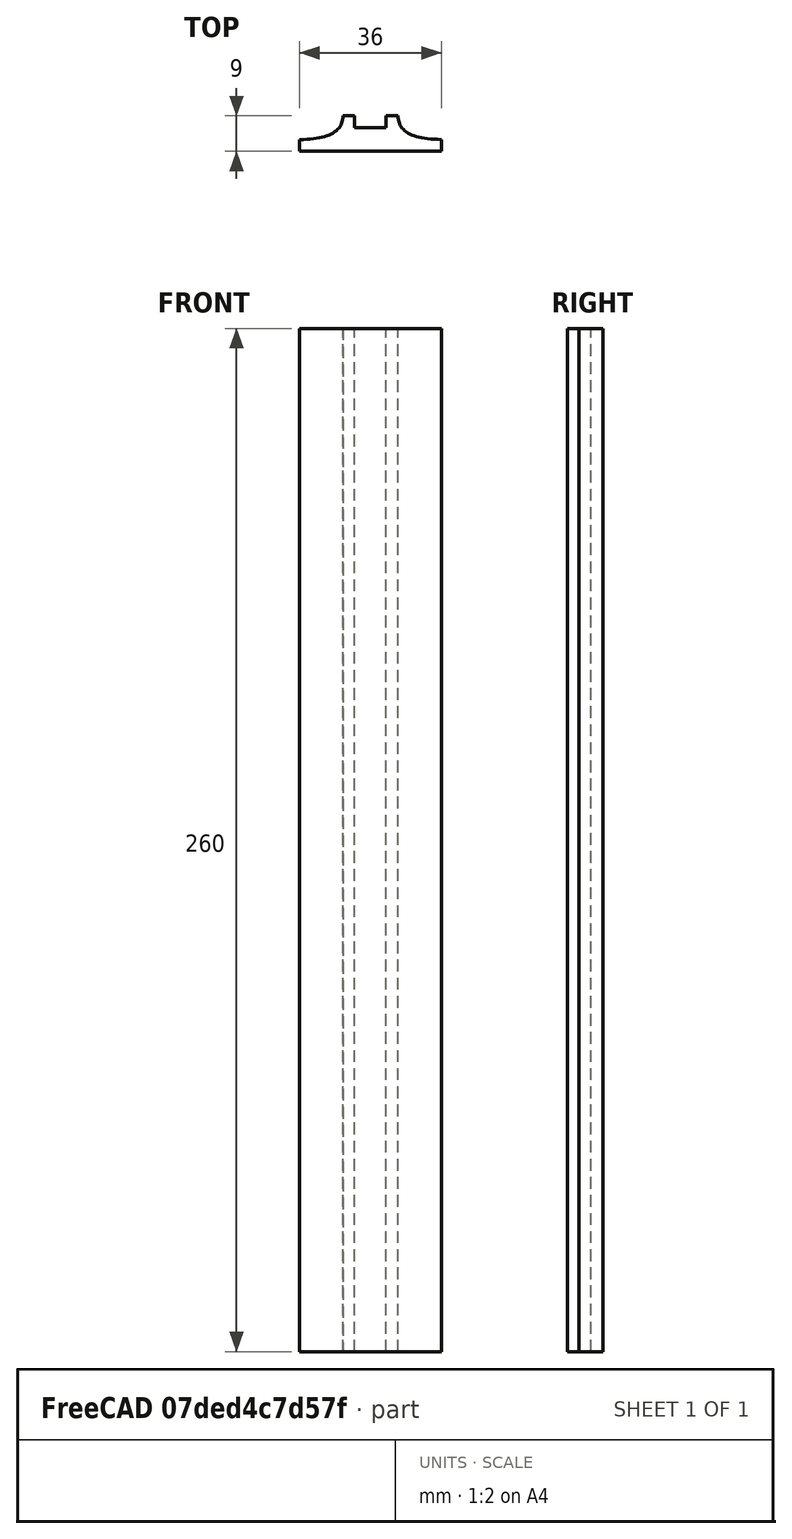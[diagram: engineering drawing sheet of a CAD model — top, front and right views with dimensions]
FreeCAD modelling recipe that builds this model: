
FCSTD DOCUMENT  (FreeCAD 0.19R0.19.2)
Label: laptopStand301.FCStd
License: All rights reserved
LicenseURL: http://en.wikipedia.org/wiki/All_rights_reserved
objects: Sketcher::SketchObject×12, Part::Extrusion×1
note: 13 computed .brp shape members not serialized (recipe doc carries the construction recipe); baked Part::Feature solids carry a one-line shape summary decoded from their .brp

FEATURE [Sketcher::SketchObject] Sketch001  label="legTop"
  FullyConstrained = true
  MapMode = 4
  Placement = pos=(0,0,0) rot=(0.57735,0.57735,0.57735;2.0944rad)
  sketch-geometry (41):
    g0: BSplineCurve PolesCount=3 KnotsCount=2 Degree=2 IsPeriodic=0
    g1: ArcOfCircle CenterX=73.1223 CenterY=-32.291 CenterZ=0 NormalX=0 NormalY=0 NormalZ=1 AngleXU=0 Radius=13 StartAngle=5.92268 EndAngle=9.06428
    g2: ArcOfCircle CenterX=66.7816 CenterY=-49.1439 CenterZ=0 NormalX=0 NormalY=0 NormalZ=1 AngleXU=0 Radius=13 StartAngle=2.78068 EndAngle=5.92131
    g3-g6: Circle x4 (B-spline internal-alignment scaffolding for g7; pole/knot coordinates omitted)
    g7: BSplineCurve PolesCount=4 KnotsCount=2 Degree=3 IsPeriodic=0
    g8: GeomPoint X=28.8094 Y=-19.0875 Z=0
    g9: GeomPoint X=47.0443 Y=-50.4712 Z=0
    g10: Circle CenterX=53.5586 CenterY=-23.2695 CenterZ=0 NormalX=0 NormalY=0 NormalZ=1 AngleXU=0 Radius=3.24518
    g11: LineSegment StartX=17.2232 StartY=-16.0875 StartZ=0 EndX=17.2232 EndY=-19.0875 EndZ=0
    g12: ArcOfCircle CenterX=17.2475 CenterY=-181.166 CenterZ=0 NormalX=0 NormalY=0 NormalZ=1 AngleXU=0 Radius=13 StartAngle=5.92268 EndAngle=7.49361
    g13: ArcOfCircle CenterX=29.5716 CenterY=-148.408 CenterZ=0 NormalX=0 NormalY=0 NormalZ=1 AngleXU=0 Radius=13 StartAngle=4.35228 EndAngle=5.92131
    g14: ArcOfCircle CenterX=35.8967 CenterY=-131.555 CenterZ=0 NormalX=0 NormalY=0 NormalZ=1 AngleXU=0 Radius=13 StartAngle=5.92268 EndAngle=7.49902
    g15: ArcOfCircle CenterX=48.1805 CenterY=-98.7782 CenterZ=0 NormalX=0 NormalY=0 NormalZ=1 AngleXU=0 Radius=13 StartAngle=4.34921 EndAngle=5.92131
    g16: ArcOfCircle CenterX=54.5183 CenterY=-81.9247 CenterZ=0 NormalX=0 NormalY=0 NormalZ=1 AngleXU=0 Radius=13 StartAngle=5.92268 EndAngle=8.70432
    g17: ArcOfCircle CenterX=20.184 CenterY=-217.506 CenterZ=0 NormalX=0 NormalY=0 NormalZ=1 AngleXU=0 Radius=3.81084 StartAngle=1.88136 EndAngle=6.80465
    g18: ArcOfCircle CenterX=36.3663 CenterY=-113.042 CenterZ=0 NormalX=0 NormalY=0 NormalZ=1 AngleXU=0 Radius=3.60555 StartAngle=0.230024 EndAngle=5.3372
    g19: ArcOfCircle CenterX=17.7945 CenterY=-162.686 CenterZ=0 NormalX=0 NormalY=0 NormalZ=1 AngleXU=0 Radius=3.60555 StartAngle=0.230024 EndAngle=5.3372
    g20: ArcOfCircle CenterX=49.8795 CenterY=-62.6074 CenterZ=0 NormalX=0 NormalY=0 NormalZ=1 AngleXU=0 Radius=3.84187 StartAngle=4.46973 EndAngle=9.40343
    g21: LineSegment StartX=48.9563 StartY=-66.3367 StartZ=0 EndX=44.7488 EndY=-73.3482 EndZ=0
    g22: LineSegment StartX=41.085 StartY=-66.3176 StartZ=0 EndX=46.0385 EndY=-62.5254 EndZ=0
    g23: LineSegment StartX=47.0443 StartY=-50.4712 StartZ=0 EndX=41.085 EndY=-66.3176 EndZ=0
    g24: LineSegment StartX=17.2232 StartY=-16.0875 StartZ=0 EndX=117.223 EndY=-16.0875 EndZ=0
    g25: LineSegment StartX=28.8094 StartY=-19.0875 StartZ=0 EndX=17.2232 EndY=-19.0875 EndZ=0
    g26: LineSegment StartX=117.223 StartY=-16.0875 StartZ=0 EndX=117.223 EndY=-19.0875 EndZ=0
    g27: LineSegment StartX=85.2866 StartY=-36.8766 StartZ=0 EndX=78.9396 EndY=-53.7463 EndZ=0
    g28: LineSegment StartX=60.9579 StartY=-27.7053 StartZ=0 EndX=54.6191 EndY=-44.5532 EndZ=0
    g29: LineSegment StartX=23.4884 StartY=-215.608 StartZ=0 EndX=94.6579 EndY=-26.1359 EndZ=0
    g30: LineSegment StartX=19.0195 StartY=-213.878 StartZ=0 EndX=29.4118 EndY=-185.752 EndZ=0
    g31: LineSegment StartX=22.7134 StartY=-166.661 StartZ=0 EndX=21.8316 EndY=-169.001 EndZ=0
    g32: LineSegment StartX=19.9036 StartY=-165.61 StartZ=0 EndX=22.7134 EndY=-166.661 EndZ=0
    g33: LineSegment StartX=21.3051 StartY=-161.864 StartZ=0 EndX=24.1149 EndY=-162.915 EndZ=0
    g34: LineSegment StartX=24.1149 StartY=-162.915 StartZ=0 EndX=24.9906 EndY=-160.574 EndZ=0
    g35: LineSegment StartX=41.7296 StartY=-153.01 StartZ=0 EndX=48.061 EndY=-136.14 EndZ=0
    g36: LineSegment StartX=41.2852 StartY=-117.017 StartZ=0 EndX=40.4148 EndY=-119.365 EndZ=0
    g37: LineSegment StartX=38.4753 StartY=-115.966 StartZ=0 EndX=41.2852 EndY=-117.017 EndZ=0
    g38: LineSegment StartX=39.8769 StartY=-112.22 StartZ=0 EndX=42.6867 EndY=-113.271 EndZ=0
    g39: LineSegment StartX=42.6867 StartY=-113.271 StartZ=0 EndX=43.5622 EndY=-110.93 EndZ=0
    g40: LineSegment StartX=66.6827 StartY=-86.5104 StartZ=0 EndX=60.3386 EndY=-103.381 EndZ=0
  constraints (65):
    c: Block(g0)
    c: Block(g1)
    c: Block(g2)
    c: Weight(g3) = 1
    c: Equal(g3,g4)
    c: Equal(g3,g5)
    c: Equal(g3,g6)
    c: InternalAlignment(g3-g6 -> g7) x4
    c: InternalAlignment(g8,g7)
    c: InternalAlignment(g9,g7)
    c: Block(g10)
    c: Block(g7)
    c: Vertical(g11)
    c: Block(g12)
    c: Block(g13)
    c: Block(g14)
    c: Block(g15)
    c: Block(g16)
    c: Block(g17)
    c: Block(g18)
    c: Block(g19)
    c: Block(g20)
    c: Coincident(g21,g20)
    c: Coincident(g21,g16)
    c: Coincident(g22,g20)
    c: Block(g22)
    c: Coincident(g23,g7)
    c: Coincident(g23,g22)
    c: Coincident(g24,g11)
    c: Horizontal(g24)
    c: Coincident(g25,g7)
    c: Coincident(g25,g11)
    c: Horizontal(g25)
    c: Coincident(g26,g24)
    c: Coincident(g26,g0)
    c: Vertical(g26)
    c: Block(g24)
    c: Coincident(g27,g1)
    c: Coincident(g27,g2)
    c: Coincident(g28,g1)
    c: Coincident(g28,g2)
    c: Coincident(g29,g17)
    c: Coincident(g29,g0)
    c: Coincident(g30,g17)
    c: Coincident(g30,g12)
    c: Coincident(g31,g12)
    c: Coincident(g32,g19)
    c: Coincident(g32,g31)
    c: Block(g31)
    c: Coincident(g33,g19)
    c: Coincident(g34,g33)
    c: Coincident(g34,g13)
    c: Block(g34)
    c: Coincident(g35,g13)
    c: Coincident(g35,g14)
    c: Coincident(g36,g14)
    c: Coincident(g37,g18)
    c: Coincident(g37,g36)
    c: Block(g36)
    c: Coincident(g38,g18)
    c: Coincident(g39,g38)
    c: Coincident(g39,g15)
    c: Block(g39)
    c: Coincident(g40,g16)
    c: Coincident(g40,g15)
FEATURE [Sketcher::SketchObject] Sketch002
  FullyConstrained = true
  sketch-geometry (20):
    g0: LineSegment StartX=-2.77179 StartY=-200.304 StartZ=0 EndX=5.22821 EndY=-200.304 EndZ=0
    g1: LineSegment StartX=5.22821 StartY=-200.304 StartZ=0 EndX=5.22821 EndY=-197.304 EndZ=0
    g2: LineSegment StartX=-2.77179 StartY=-200.304 StartZ=0 EndX=-2.77179 EndY=-197.304 EndZ=0
    g3: LineSegment StartX=5.22821 StartY=-197.304 StartZ=0 EndX=8.22821 EndY=-197.304 EndZ=0
    g4: LineSegment StartX=-2.77179 StartY=-197.304 StartZ=0 EndX=-5.77179 EndY=-197.304 EndZ=0
    g5: LineSegment StartX=19.2282 StartY=-203.304 StartZ=0 EndX=19.2282 EndY=-206.304 EndZ=0
    g6: LineSegment StartX=-16.7718 StartY=-203.304 StartZ=0 EndX=-16.7718 EndY=-206.304 EndZ=0
    g7: LineSegment StartX=-16.7718 StartY=-206.304 StartZ=0 EndX=19.2282 EndY=-206.304 EndZ=0
    g8: Circle CenterX=-16.7718 CenterY=-203.304 CenterZ=0 NormalX=0 NormalY=0 NormalZ=1 AngleXU=0 Radius=1
    g9: Circle CenterX=-5.77179 CenterY=-203.304 CenterZ=0 NormalX=0 NormalY=0 NormalZ=1 AngleXU=0 Radius=1
    g10: Circle CenterX=-5.77179 CenterY=-197.304 CenterZ=0 NormalX=0 NormalY=0 NormalZ=1 AngleXU=0 Radius=1
    g11: BSplineCurve PolesCount=3 KnotsCount=2 Degree=2 IsPeriodic=0
    g12: GeomPoint X=-16.7718 Y=-203.304 Z=0
    g13: GeomPoint X=-5.77179 Y=-197.304 Z=0
    g14: Circle CenterX=19.2282 CenterY=-203.304 CenterZ=0 NormalX=0 NormalY=0 NormalZ=1 AngleXU=0 Radius=1
    g15: Circle CenterX=8.22821 CenterY=-203.304 CenterZ=0 NormalX=0 NormalY=0 NormalZ=1 AngleXU=0 Radius=1
    g16: Circle CenterX=8.22821 CenterY=-197.304 CenterZ=0 NormalX=0 NormalY=0 NormalZ=1 AngleXU=0 Radius=1
    g17: BSplineCurve PolesCount=3 KnotsCount=2 Degree=2 IsPeriodic=0
    g18: GeomPoint X=19.2282 Y=-203.304 Z=0
    g19: GeomPoint X=8.22821 Y=-197.304 Z=0
  constraints (41):
    c: Horizontal(g0)
    c: Distance(g0) = 8
    c: Coincident(g1,g0)
    c: Vertical(g1)
    c: Distance(g1) = 3
    c: Coincident(g2,g0)
    c: Vertical(g2)
    c: Distance(g2) = 3
    c: Coincident(g3,g1)
    c: Horizontal(g3)
    c: Distance(g3) = 3
    c: Coincident(g4,g2)
    c: Horizontal(g4)
    c: Distance(g4) = 3
    c: Vertical(g5)
    c: Vertical(g6)
    c: Coincident(g7,g6)
    c: Coincident(g7,g5)
    c: Weight(g8) = 1
    c: Equal(g8,g9)
    c: Equal(g8,g10)
    c: Coincident(g11,g4)
    c: InternalAlignment(g8,g11)
    c: InternalAlignment(g9,g11)
    c: InternalAlignment(g10,g11)
    c: InternalAlignment(g12,g11)
    c: InternalAlignment(g13,g11)
    c: Coincident(g17,g5)
    c: Weight(g14) = 1
    c: Equal(g14,g15)
    c: Equal(g14,g16)
    c: Coincident(g17,g3)
    c: InternalAlignment(g14,g17)
    c: InternalAlignment(g15,g17)
    c: InternalAlignment(g16,g17)
    c: InternalAlignment(g18,g17)
    c: InternalAlignment(g19,g17)
    c: Block(g7)
    c: Block(g17)
    c: Block(g11)
    c: Block(g6)
FEATURE [Part::Extrusion] Extrude003
  Base = -> Sketch002
  Dir = (0,0,1)
  DirMode = 2
  FaceMakerClass = Part::FaceMakerBullseye
  LengthFwd = 260
  LengthRev = 0
  Solid = true
  Symmetric = false
FEATURE [Sketcher::SketchObject] Sketch003  label="original"
  FullyConstrained = false
  sketch-geometry (469):
    g0: LineSegment StartX=-42.9272 StartY=136.221 StartZ=0 EndX=-42.9272 EndY=-103.779 EndZ=0
    g1: LineSegment StartX=407.073 StartY=136.221 StartZ=0 EndX=407.073 EndY=-103.779 EndZ=0
    g2: ArcOfCircle CenterX=-26.9272 CenterY=-83.7794 CenterZ=0 NormalX=0 NormalY=0 NormalZ=1 AngleXU=0 Radius=8 StartAngle=3.14159 EndAngle=6.28319
    g3: ArcOfCircle CenterX=391.073 CenterY=-83.7794 CenterZ=0 NormalX=0 NormalY=0 NormalZ=1 AngleXU=0 Radius=8 StartAngle=3.14159 EndAngle=6.28319
    g4: Circle CenterX=175.022 CenterY=27.0628 CenterZ=0 NormalX=0 NormalY=0 NormalZ=1 AngleXU=0 Radius=1
    g5: Circle CenterX=179.022 CenterY=24.8665 CenterZ=0 NormalX=0 NormalY=0 NormalZ=1 AngleXU=0 Radius=1
    g6: Circle CenterX=179.022 CenterY=27.0628 CenterZ=0 NormalX=0 NormalY=0 NormalZ=1 AngleXU=0 Radius=1
    g7: BSplineCurve PolesCount=3 KnotsCount=2 Degree=2 IsPeriodic=0
    g8: GeomPoint X=175.022 Y=27.0628 Z=0
    g9: GeomPoint X=179.022 Y=27.0628 Z=0
    g10: Circle CenterX=189.124 CenterY=27.0628 CenterZ=0 NormalX=0 NormalY=0 NormalZ=1 AngleXU=0 Radius=1
    g11: Circle CenterX=185.124 CenterY=24.8665 CenterZ=0 NormalX=0 NormalY=0 NormalZ=1 AngleXU=0 Radius=1
    g12: Circle CenterX=185.124 CenterY=27.0628 CenterZ=0 NormalX=0 NormalY=0 NormalZ=1 AngleXU=0 Radius=1
    g13: BSplineCurve PolesCount=3 KnotsCount=2 Degree=2 IsPeriodic=0
    g14: GeomPoint X=189.124 Y=27.0628 Z=0
    g15: GeomPoint X=185.124 Y=27.0628 Z=0
    g16: Circle CenterX=175.022 CenterY=5.37834 CenterZ=0 NormalX=0 NormalY=0 NormalZ=1 AngleXU=0 Radius=1
    g17: Circle CenterX=179.022 CenterY=7.57463 CenterZ=0 NormalX=0 NormalY=0 NormalZ=1 AngleXU=0 Radius=1
    g18: Circle CenterX=179.022 CenterY=5.34704 CenterZ=0 NormalX=0 NormalY=0 NormalZ=1 AngleXU=0 Radius=1
    g19: BSplineCurve PolesCount=3 KnotsCount=2 Degree=2 IsPeriodic=0
    g20: GeomPoint X=175.022 Y=5.37834 Z=0
    g21: GeomPoint X=179.022 Y=5.34704 Z=0
    g22: Circle CenterX=189.124 CenterY=5.37834 CenterZ=0 NormalX=0 NormalY=0 NormalZ=1 AngleXU=0 Radius=1
    g23: Circle CenterX=185.124 CenterY=7.57463 CenterZ=0 NormalX=0 NormalY=0 NormalZ=1 AngleXU=0 Radius=1
    g24: Circle CenterX=185.124 CenterY=5.34704 CenterZ=0 NormalX=0 NormalY=0 NormalZ=1 AngleXU=0 Radius=1
    g25: BSplineCurve PolesCount=3 KnotsCount=2 Degree=2 IsPeriodic=0
    g26: GeomPoint X=189.124 Y=5.37834 Z=0
    g27: GeomPoint X=185.124 Y=5.34704 Z=0
    g28: Circle CenterX=165.871 CenterY=18.1458 CenterZ=0 NormalX=0 NormalY=0 NormalZ=1 AngleXU=0 Radius=1
    g29: Circle CenterX=169.377 CenterY=16.2206 CenterZ=0 NormalX=0 NormalY=0 NormalZ=1 AngleXU=0 Radius=1
    g30: Circle CenterX=165.871 CenterY=14.2956 CenterZ=0 NormalX=0 NormalY=0 NormalZ=1 AngleXU=0 Radius=1
    g31: BSplineCurve PolesCount=3 KnotsCount=2 Degree=2 IsPeriodic=0
    g32: GeomPoint X=165.871 Y=18.1458 Z=0
    g33: GeomPoint X=165.871 Y=14.2956 Z=0
    g34: Circle CenterX=198.275 CenterY=18.1318 CenterZ=0 NormalX=0 NormalY=0 NormalZ=1 AngleXU=0 Radius=1
    g35: Circle CenterX=194.768 CenterY=16.2206 CenterZ=0 NormalX=0 NormalY=0 NormalZ=1 AngleXU=0 Radius=1
    g36: Circle CenterX=198.264 CenterY=14.2963 CenterZ=0 NormalX=0 NormalY=0 NormalZ=1 AngleXU=0 Radius=1
    g37: BSplineCurve PolesCount=3 KnotsCount=2 Degree=2 IsPeriodic=0
    g38: GeomPoint X=198.275 Y=18.1318 Z=0
    g39: GeomPoint X=198.264 Y=14.2963 Z=0
    g40: LineSegment StartX=407.073 StartY=-103.779 StartZ=0 EndX=-42.9272 EndY=-103.779 EndZ=0
    g41: Circle CenterX=125.607 CenterY=54.1951 CenterZ=0 NormalX=0 NormalY=0 NormalZ=1 AngleXU=0 Radius=1
    g42: Circle CenterX=139.632 CenterY=46.4944 CenterZ=0 NormalX=0 NormalY=0 NormalZ=1 AngleXU=0 Radius=1
    g43: Circle CenterX=127.326 CenterY=56.7187 CenterZ=0 NormalX=0 NormalY=0 NormalZ=1 AngleXU=0 Radius=1
    g44: BSplineCurve PolesCount=3 KnotsCount=2 Degree=2 IsPeriodic=0
    g45: GeomPoint X=125.607 Y=54.1951 Z=0
    g46: GeomPoint X=127.326 Y=56.7187 Z=0
    g47: Circle CenterX=236.824 CenterY=56.7187 CenterZ=0 NormalX=0 NormalY=0 NormalZ=1 AngleXU=0 Radius=1
    g48: Circle CenterX=224.513 CenterY=46.4944 CenterZ=0 NormalX=0 NormalY=0 NormalZ=1 AngleXU=0 Radius=1
    g49: Circle CenterX=238.538 CenterY=54.1951 CenterZ=0 NormalX=0 NormalY=0 NormalZ=1 AngleXU=0 Radius=1
    g50: BSplineCurve PolesCount=3 KnotsCount=2 Degree=2 IsPeriodic=0
    g51: GeomPoint X=236.824 Y=56.7187 Z=0
    g52: GeomPoint X=238.538 Y=54.1951 Z=0
    g53: Circle CenterX=238.538 CenterY=-21.7516 CenterZ=0 NormalX=0 NormalY=0 NormalZ=1 AngleXU=0 Radius=1
    g54: Circle CenterX=224.513 CenterY=-14.0532 CenterZ=0 NormalX=0 NormalY=0 NormalZ=1 AngleXU=0 Radius=1
    g55: Circle CenterX=236.584 CenterY=-24.2775 CenterZ=0 NormalX=0 NormalY=0 NormalZ=1 AngleXU=0 Radius=1
    g56: BSplineCurve PolesCount=3 KnotsCount=2 Degree=2 IsPeriodic=0
    g57: GeomPoint X=238.538 Y=-21.7516 Z=0
    g58: GeomPoint X=236.584 Y=-24.2775 Z=0
    g59: Circle CenterX=125.607 CenterY=-21.7539 CenterZ=0 NormalX=0 NormalY=0 NormalZ=1 AngleXU=0 Radius=1
    g60: Circle CenterX=139.632 CenterY=-14.0532 CenterZ=0 NormalX=0 NormalY=0 NormalZ=1 AngleXU=0 Radius=1
    g61: Circle CenterX=127.325 CenterY=-24.2775 CenterZ=0 NormalX=0 NormalY=0 NormalZ=1 AngleXU=0 Radius=1
    g62: BSplineCurve PolesCount=3 KnotsCount=2 Degree=2 IsPeriodic=0
    g63: GeomPoint X=125.607 Y=-21.7539 Z=0
    g64: GeomPoint X=127.325 Y=-24.2775 Z=0
    g65: Circle CenterX=302.996 CenterY=111.695 CenterZ=0 NormalX=0 NormalY=0 NormalZ=1 AngleXU=0 Radius=1
    g66: Circle CenterX=306.073 CenterY=114.251 CenterZ=0 NormalX=0 NormalY=0 NormalZ=1 AngleXU=0 Radius=1
    g67: Circle CenterX=306.073 CenterY=110.251 CenterZ=0 NormalX=0 NormalY=0 NormalZ=1 AngleXU=0 Radius=1
    g68: BSplineCurve PolesCount=3 KnotsCount=2 Degree=2 IsPeriodic=0
    g69: GeomPoint X=302.996 Y=111.695 Z=0
    g70: GeomPoint X=306.073 Y=110.251 Z=0
    g71: Circle CenterX=306.073 CenterY=95.2763 CenterZ=0 NormalX=0 NormalY=0 NormalZ=1 AngleXU=0 Radius=1
    g72: Circle CenterX=306.073 CenterY=91.2763 CenterZ=0 NormalX=0 NormalY=0 NormalZ=1 AngleXU=0 Radius=1
    g73: Circle CenterX=302.567 CenterY=89.3511 CenterZ=0 NormalX=0 NormalY=0 NormalZ=1 AngleXU=0 Radius=1
    g74: BSplineCurve PolesCount=3 KnotsCount=2 Degree=2 IsPeriodic=0
    g75: GeomPoint X=306.073 Y=95.2763 Z=0
    g76: GeomPoint X=302.567 Y=89.3511 Z=0
    g77: LineSegment StartX=306.073 StartY=110.251 StartZ=0 EndX=306.073 EndY=95.2763 EndZ=0
    g78: LineSegment StartX=302.996 StartY=111.695 StartZ=0 EndX=236.824 EndY=56.7187 EndZ=0
    g79: LineSegment StartX=238.538 StartY=54.1951 StartZ=0 EndX=302.567 EndY=89.3511 EndZ=0
    g80: Circle CenterX=61.1496 CenterY=111.695 CenterZ=0 NormalX=0 NormalY=0 NormalZ=1 AngleXU=0 Radius=1
    g81: Circle CenterX=58.0728 CenterY=114.251 CenterZ=0 NormalX=0 NormalY=0 NormalZ=1 AngleXU=0 Radius=1
    g82: Circle CenterX=58.0728 CenterY=110.251 CenterZ=0 NormalX=0 NormalY=0 NormalZ=1 AngleXU=0 Radius=1
    g83: BSplineCurve PolesCount=3 KnotsCount=2 Degree=2 IsPeriodic=0
    g84: GeomPoint X=61.1496 Y=111.695 Z=0
    g85: GeomPoint X=58.0728 Y=110.251 Z=0
    g86: Circle CenterX=61.5791 CenterY=89.3511 CenterZ=0 NormalX=0 NormalY=0 NormalZ=1 AngleXU=0 Radius=1
    g87: Circle CenterX=58.0728 CenterY=91.2763 CenterZ=0 NormalX=0 NormalY=0 NormalZ=1 AngleXU=0 Radius=1
    g88: Circle CenterX=58.0728 CenterY=95.2763 CenterZ=0 NormalX=0 NormalY=0 NormalZ=1 AngleXU=0 Radius=1
    g89: BSplineCurve PolesCount=3 KnotsCount=2 Degree=2 IsPeriodic=0
    g90: GeomPoint X=61.5791 Y=89.3511 Z=0
    g91: GeomPoint X=58.0728 Y=95.2763 Z=0
    g92: LineSegment StartX=58.0728 StartY=110.251 StartZ=0 EndX=58.0728 EndY=95.2763 EndZ=0
    g93: LineSegment StartX=61.1496 StartY=111.695 StartZ=0 EndX=127.326 EndY=56.7187 EndZ=0
    g94: LineSegment StartX=125.607 StartY=54.1951 StartZ=0 EndX=61.5791 EndY=89.3511 EndZ=0
    g95: Circle CenterX=61.5791 CenterY=-56.9099 CenterZ=0 NormalX=0 NormalY=0 NormalZ=1 AngleXU=0 Radius=1
    g96: Circle CenterX=58.0728 CenterY=-58.8351 CenterZ=0 NormalX=0 NormalY=0 NormalZ=1 AngleXU=0 Radius=1
    g97: Circle CenterX=58.0728 CenterY=-62.8351 CenterZ=0 NormalX=0 NormalY=0 NormalZ=1 AngleXU=0 Radius=1
    g98: BSplineCurve PolesCount=3 KnotsCount=2 Degree=2 IsPeriodic=0
    g99: GeomPoint X=61.5791 Y=-56.9099 Z=0
    g100: GeomPoint X=58.0728 Y=-62.8351 Z=0
    g101: Circle CenterX=58.0728 CenterY=-77.8102 CenterZ=0 NormalX=0 NormalY=0 NormalZ=1 AngleXU=0 Radius=1
    g102: Circle CenterX=58.0728 CenterY=-81.8102 CenterZ=0 NormalX=0 NormalY=0 NormalZ=1 AngleXU=0 Radius=1
    g103: Circle CenterX=61.1496 CenterY=-79.2541 CenterZ=0 NormalX=0 NormalY=0 NormalZ=1 AngleXU=0 Radius=1
    g104: BSplineCurve PolesCount=3 KnotsCount=2 Degree=2 IsPeriodic=0
    g105: GeomPoint X=58.0728 Y=-77.8102 Z=0
    g106: GeomPoint X=61.1496 Y=-79.2541 Z=0
    g107: LineSegment StartX=58.0728 StartY=-62.8351 StartZ=0 EndX=58.0728 EndY=-77.8102 EndZ=0
    g108: LineSegment StartX=61.1496 StartY=-79.2541 StartZ=0 EndX=127.325 EndY=-24.2775 EndZ=0
    g109: LineSegment StartX=125.607 StartY=-21.7539 StartZ=0 EndX=61.5791 EndY=-56.9099 EndZ=0
    g110: Circle CenterX=302.567 CenterY=-56.9099 CenterZ=0 NormalX=0 NormalY=0 NormalZ=1 AngleXU=0 Radius=1
    g111: Circle CenterX=306.073 CenterY=-58.8351 CenterZ=0 NormalX=0 NormalY=0 NormalZ=1 AngleXU=0 Radius=1
    g112: Circle CenterX=306.073 CenterY=-62.8351 CenterZ=0 NormalX=0 NormalY=0 NormalZ=1 AngleXU=0 Radius=1
    g113: BSplineCurve PolesCount=3 KnotsCount=2 Degree=2 IsPeriodic=0
    g114: GeomPoint X=302.567 Y=-56.9099 Z=0
    g115: GeomPoint X=306.073 Y=-62.8351 Z=0
    g116: Circle CenterX=302.996 CenterY=-79.2541 CenterZ=0 NormalX=0 NormalY=0 NormalZ=1 AngleXU=0 Radius=1
    g117: Circle CenterX=306.073 CenterY=-81.8102 CenterZ=0 NormalX=0 NormalY=0 NormalZ=1 AngleXU=0 Radius=1
    g118: Circle CenterX=306.073 CenterY=-77.8102 CenterZ=0 NormalX=0 NormalY=0 NormalZ=1 AngleXU=0 Radius=1
    g119: BSplineCurve PolesCount=3 KnotsCount=2 Degree=2 IsPeriodic=0
    g120: GeomPoint X=302.996 Y=-79.2541 Z=0
    g121: GeomPoint X=306.073 Y=-77.8102 Z=0
    g122: LineSegment StartX=306.073 StartY=-62.8351 StartZ=0 EndX=306.073 EndY=-77.8102 EndZ=0
    g123: LineSegment StartX=302.996 StartY=-79.2541 StartZ=0 EndX=236.584 EndY=-24.2775 EndZ=0
    g124: LineSegment StartX=238.538 StartY=-21.7516 StartZ=0 EndX=302.567 EndY=-56.9099 EndZ=0
    g125: Circle CenterX=61.6457 CenterY=-88.8112 CenterZ=0 NormalX=0 NormalY=0 NormalZ=1 AngleXU=0 Radius=1
    g126: Circle CenterX=58.0728 CenterY=-91.7794 CenterZ=0 NormalX=0 NormalY=0 NormalZ=1 AngleXU=0 Radius=1
    g127: Circle CenterX=63.9135 CenterY=-91.7791 CenterZ=0 NormalX=0 NormalY=0 NormalZ=1 AngleXU=0 Radius=1
    g128: BSplineCurve PolesCount=3 KnotsCount=2 Degree=2 IsPeriodic=0
    g129: GeomPoint X=61.6457 Y=-88.8112 Z=0
    g130: GeomPoint X=63.9135 Y=-91.7791 Z=0
    g131: Circle CenterX=179.022 CenterY=-85.8163 CenterZ=0 NormalX=0 NormalY=0 NormalZ=1 AngleXU=0 Radius=1
    g132: Circle CenterX=179.022 CenterY=-91.7794 CenterZ=0 NormalX=0 NormalY=0 NormalZ=1 AngleXU=0 Radius=1
    g133: Circle CenterX=171.895 CenterY=-91.7791 CenterZ=0 NormalX=0 NormalY=0 NormalZ=1 AngleXU=0 Radius=1
    g134: BSplineCurve PolesCount=3 KnotsCount=2 Degree=2 IsPeriodic=0
    g135: GeomPoint X=179.022 Y=-85.8163 Z=0
    g136: GeomPoint X=171.895 Y=-91.7791 Z=0
    g137: Circle CenterX=185.124 CenterY=-86.2028 CenterZ=0 NormalX=0 NormalY=0 NormalZ=1 AngleXU=0 Radius=1
    g138: Circle CenterX=185.124 CenterY=-91.7794 CenterZ=0 NormalX=0 NormalY=0 NormalZ=1 AngleXU=0 Radius=1
    g139: Circle CenterX=191.747 CenterY=-91.7794 CenterZ=0 NormalX=0 NormalY=0 NormalZ=1 AngleXU=0 Radius=1
    g140: BSplineCurve PolesCount=3 KnotsCount=2 Degree=2 IsPeriodic=0
    g141: GeomPoint X=185.124 Y=-86.2028 Z=0
    g142: GeomPoint X=191.747 Y=-91.7794 Z=0
    g143: Circle CenterX=299.888 CenterY=-86.6413 CenterZ=0 NormalX=0 NormalY=0 NormalZ=1 AngleXU=0 Radius=1
    g144: Circle CenterX=306.073 CenterY=-91.7794 CenterZ=0 NormalX=0 NormalY=0 NormalZ=1 AngleXU=0 Radius=1
    g145: Circle CenterX=298.776 CenterY=-91.7794 CenterZ=0 NormalX=0 NormalY=0 NormalZ=1 AngleXU=0 Radius=1
    g146: BSplineCurve PolesCount=3 KnotsCount=2 Degree=2 IsPeriodic=0
    g147: GeomPoint X=299.888 Y=-86.6413 Z=0
    g148: GeomPoint X=298.776 Y=-91.7794 Z=0
    g149: LineSegment StartX=189.124 StartY=5.37834 StartZ=0 EndX=299.888 EndY=-86.6413 EndZ=0
    g150: LineSegment StartX=298.776 StartY=-91.7794 StartZ=0 EndX=191.747 EndY=-91.7794 EndZ=0
    g151: LineSegment StartX=185.124 StartY=-86.2028 StartZ=0 EndX=185.124 EndY=5.34704 EndZ=0
    g152: LineSegment StartX=179.022 StartY=5.34704 StartZ=0 EndX=179.022 EndY=-85.8163 EndZ=0
    g153: LineSegment StartX=171.895 StartY=-91.7791 StartZ=0 EndX=63.9135 EndY=-91.7791 EndZ=0
    g154: LineSegment StartX=61.6457 StartY=-88.8112 StartZ=0 EndX=175.022 EndY=5.37834 EndZ=0
    g155: Circle CenterX=302.073 CenterY=124.221 CenterZ=0 NormalX=0 NormalY=0 NormalZ=1 AngleXU=0 Radius=1
    g156: Circle CenterX=306.073 CenterY=124.221 CenterZ=0 NormalX=0 NormalY=0 NormalZ=1 AngleXU=0 Radius=1
    g157: Circle CenterX=302.996 CenterY=121.665 CenterZ=0 NormalX=0 NormalY=0 NormalZ=1 AngleXU=0 Radius=1
    g158: BSplineCurve PolesCount=3 KnotsCount=2 Degree=2 IsPeriodic=0
    g159: GeomPoint X=302.073 Y=124.221 Z=0
    g160: GeomPoint X=302.996 Y=121.665 Z=0
    g161: Circle CenterX=189.124 CenterY=124.221 CenterZ=0 NormalX=0 NormalY=0 NormalZ=1 AngleXU=0 Radius=1
    g162: Circle CenterX=185.124 CenterY=124.221 CenterZ=0 NormalX=0 NormalY=0 NormalZ=1 AngleXU=0 Radius=1
    g163: Circle CenterX=185.124 CenterY=120.221 CenterZ=0 NormalX=0 NormalY=0 NormalZ=1 AngleXU=0 Radius=1
    g164: BSplineCurve PolesCount=3 KnotsCount=2 Degree=2 IsPeriodic=0
    g165: GeomPoint X=189.124 Y=124.221 Z=0
    g166: GeomPoint X=185.124 Y=120.221 Z=0
    g167: Circle CenterX=175.022 CenterY=124.221 CenterZ=0 NormalX=0 NormalY=0 NormalZ=1 AngleXU=0 Radius=1
    g168: Circle CenterX=179.022 CenterY=124.221 CenterZ=0 NormalX=0 NormalY=0 NormalZ=1 AngleXU=0 Radius=1
    g169: Circle CenterX=179.022 CenterY=120.221 CenterZ=0 NormalX=0 NormalY=0 NormalZ=1 AngleXU=0 Radius=1
    g170: BSplineCurve PolesCount=3 KnotsCount=2 Degree=2 IsPeriodic=0
    g171: GeomPoint X=175.022 Y=124.221 Z=0
    g172: GeomPoint X=179.022 Y=120.221 Z=0
    g173: Circle CenterX=62.0728 CenterY=124.221 CenterZ=0 NormalX=0 NormalY=0 NormalZ=1 AngleXU=0 Radius=1
    g174: Circle CenterX=58.0728 CenterY=124.221 CenterZ=0 NormalX=0 NormalY=0 NormalZ=1 AngleXU=0 Radius=1
    g175: Circle CenterX=61.1496 CenterY=121.665 CenterZ=0 NormalX=0 NormalY=0 NormalZ=1 AngleXU=0 Radius=1
    g176: BSplineCurve PolesCount=3 KnotsCount=2 Degree=2 IsPeriodic=0
    g177: GeomPoint X=62.0728 Y=124.221 Z=0
    g178: GeomPoint X=61.1496 Y=121.665 Z=0
    g179: LineSegment StartX=179.022 StartY=120.221 StartZ=0 EndX=179.022 EndY=27.0628 EndZ=0
    g180: LineSegment StartX=185.124 StartY=27.0628 StartZ=0 EndX=185.124 EndY=120.221 EndZ=0
    g181: LineSegment StartX=302.996 StartY=121.665 StartZ=0 EndX=189.124 EndY=27.0628 EndZ=0
    g182: LineSegment StartX=175.022 StartY=27.0628 StartZ=0 EndX=61.1496 EndY=121.665 EndZ=0
    g183: Circle CenterX=61.5791 CenterY=75.4095 CenterZ=0 NormalX=0 NormalY=0 NormalZ=1 AngleXU=0 Radius=1
    g184: Circle CenterX=58.0728 CenterY=77.3346 CenterZ=0 NormalX=0 NormalY=0 NormalZ=1 AngleXU=0 Radius=1
    g185: Circle CenterX=58.0728 CenterY=73.3346 CenterZ=0 NormalX=0 NormalY=0 NormalZ=1 AngleXU=0 Radius=1
    g186: BSplineCurve PolesCount=3 KnotsCount=2 Degree=2 IsPeriodic=0
    g187: GeomPoint X=61.5791 Y=75.4095 Z=0
    g188: GeomPoint X=58.0728 Y=73.3346 Z=0
    g189: Circle CenterX=58.0728 CenterY=-40.8935 CenterZ=0 NormalX=0 NormalY=0 NormalZ=1 AngleXU=0 Radius=1
    g190: Circle CenterX=58.0728 CenterY=-44.8935 CenterZ=0 NormalX=0 NormalY=0 NormalZ=1 AngleXU=0 Radius=1
    g191: Circle CenterX=61.5791 CenterY=-42.9683 CenterZ=0 NormalX=0 NormalY=0 NormalZ=1 AngleXU=0 Radius=1
    g192: BSplineCurve PolesCount=3 KnotsCount=2 Degree=2 IsPeriodic=0
    g193: GeomPoint X=58.0728 Y=-40.8935 Z=0
    g194: GeomPoint X=61.5791 Y=-42.9683 Z=0
    g195: LineSegment StartX=61.5791 StartY=-42.9683 StartZ=0 EndX=165.871 EndY=14.2956 EndZ=0
    g196: LineSegment StartX=165.871 StartY=18.1458 StartZ=0 EndX=61.5791 EndY=75.4095 EndZ=0
    g197: LineSegment StartX=58.0728 StartY=73.3346 StartZ=0 EndX=58.0728 EndY=-40.8935 EndZ=0
    g198: Circle CenterX=302.567 CenterY=-42.9683 CenterZ=0 NormalX=0 NormalY=0 NormalZ=1 AngleXU=0 Radius=1
    g199: Circle CenterX=306.073 CenterY=-44.8935 CenterZ=0 NormalX=0 NormalY=0 NormalZ=1 AngleXU=0 Radius=1
    g200: Circle CenterX=306.073 CenterY=-40.8935 CenterZ=0 NormalX=0 NormalY=0 NormalZ=1 AngleXU=0 Radius=1
    g201: BSplineCurve PolesCount=3 KnotsCount=2 Degree=2 IsPeriodic=0
    g202: GeomPoint X=302.567 Y=-42.9683 Z=0
    g203: GeomPoint X=306.073 Y=-40.8935 Z=0
    g204: Circle CenterX=306.073 CenterY=73.3346 CenterZ=0 NormalX=0 NormalY=0 NormalZ=1 AngleXU=0 Radius=1
    g205: Circle CenterX=306.073 CenterY=77.3346 CenterZ=0 NormalX=0 NormalY=0 NormalZ=1 AngleXU=0 Radius=1
    g206: Circle CenterX=302.535 CenterY=75.4095 CenterZ=0 NormalX=0 NormalY=0 NormalZ=1 AngleXU=0 Radius=1
    g207: BSplineCurve PolesCount=3 KnotsCount=2 Degree=2 IsPeriodic=0
    g208: GeomPoint X=306.073 Y=73.3346 Z=0
    g209: GeomPoint X=302.535 Y=75.4095 Z=0
    g210: LineSegment StartX=302.567 StartY=-42.9683 StartZ=0 EndX=198.264 EndY=14.2963 EndZ=0
    g211: LineSegment StartX=198.275 StartY=18.1318 StartZ=0 EndX=302.535 EndY=75.4095 EndZ=0
    g212: LineSegment StartX=306.073 StartY=73.3346 StartZ=0 EndX=306.073 EndY=-40.8935 EndZ=0
    g213: LineSegment StartX=322.073 StartY=105.865 StartZ=0 EndX=328.643 EndY=105.865 EndZ=0
    g214: LineSegment StartX=318.073 StartY=120.221 StartZ=0 EndX=318.073 EndY=109.865 EndZ=0
    g215: LineSegment StartX=336.157 StartY=107.779 StartZ=0 EndX=362.567 EndY=122.294 EndZ=0
    g216: Circle CenterX=362.073 CenterY=124.221 CenterZ=0 NormalX=0 NormalY=0 NormalZ=1 AngleXU=0 Radius=1
    g217: Circle CenterX=366.073 CenterY=124.221 CenterZ=0 NormalX=0 NormalY=0 NormalZ=1 AngleXU=0 Radius=1
    g218: Circle CenterX=362.567 CenterY=122.294 CenterZ=0 NormalX=0 NormalY=0 NormalZ=1 AngleXU=0 Radius=1
    g219: BSplineCurve PolesCount=3 KnotsCount=2 Degree=2 IsPeriodic=0
    g220: GeomPoint X=362.073 Y=124.221 Z=0
    g221: GeomPoint X=362.567 Y=122.294 Z=0
    g222: Circle CenterX=322.073 CenterY=124.221 CenterZ=0 NormalX=0 NormalY=0 NormalZ=1 AngleXU=0 Radius=1
    g223: Circle CenterX=318.073 CenterY=124.221 CenterZ=0 NormalX=0 NormalY=0 NormalZ=1 AngleXU=0 Radius=1
    g224: Circle CenterX=318.073 CenterY=120.221 CenterZ=0 NormalX=0 NormalY=0 NormalZ=1 AngleXU=0 Radius=1
    g225: BSplineCurve PolesCount=3 KnotsCount=2 Degree=2 IsPeriodic=0
    g226: GeomPoint X=322.073 Y=124.221 Z=0
    g227: GeomPoint X=318.073 Y=120.221 Z=0
    g228: Circle CenterX=322.073 CenterY=105.865 CenterZ=0 NormalX=0 NormalY=0 NormalZ=1 AngleXU=0 Radius=1
    g229: Circle CenterX=318.073 CenterY=105.865 CenterZ=0 NormalX=0 NormalY=0 NormalZ=1 AngleXU=0 Radius=1
    g230: Circle CenterX=318.073 CenterY=109.865 CenterZ=0 NormalX=0 NormalY=0 NormalZ=1 AngleXU=0 Radius=1
    g231: BSplineCurve PolesCount=3 KnotsCount=2 Degree=2 IsPeriodic=0
    g232: GeomPoint X=322.073 Y=105.865 Z=0
    g233: GeomPoint X=318.073 Y=109.865 Z=0
    g234: Circle CenterX=336.157 CenterY=107.779 CenterZ=0 NormalX=0 NormalY=0 NormalZ=1 AngleXU=0 Radius=1
    g235: Circle CenterX=332.651 CenterY=105.853 CenterZ=0 NormalX=0 NormalY=0 NormalZ=1 AngleXU=0 Radius=1
    g236: Circle CenterX=328.643 CenterY=105.865 CenterZ=0 NormalX=0 NormalY=0 NormalZ=1 AngleXU=0 Radius=1
    g237: BSplineCurve PolesCount=3 KnotsCount=2 Degree=2 IsPeriodic=0
    g238: GeomPoint X=336.157 Y=107.779 Z=0
    g239: GeomPoint X=328.643 Y=105.865 Z=0
    g240: LineSegment StartX=322.073 StartY=124.221 StartZ=0 EndX=362.073 EndY=124.221 EndZ=0
    g241: Circle CenterX=371.567 CenterY=-80.8644 CenterZ=0 NormalX=0 NormalY=0 NormalZ=1 AngleXU=0 Radius=1
    g242: Circle CenterX=375.073 CenterY=-82.7896 CenterZ=0 NormalX=0 NormalY=0 NormalZ=1 AngleXU=0 Radius=1
    g243: Circle CenterX=375.073 CenterY=-78.7896 CenterZ=0 NormalX=0 NormalY=0 NormalZ=1 AngleXU=0 Radius=1
    g244: BSplineCurve PolesCount=3 KnotsCount=2 Degree=2 IsPeriodic=0
    g245: GeomPoint X=371.567 Y=-80.8644 Z=0
    g246: GeomPoint X=375.073 Y=-78.7896 Z=0
    g247: Circle CenterX=321.579 CenterY=-53.4075 CenterZ=0 NormalX=0 NormalY=0 NormalZ=1 AngleXU=0 Radius=1
    g248: Circle CenterX=318.073 CenterY=-51.4823 CenterZ=0 NormalX=0 NormalY=0 NormalZ=1 AngleXU=0 Radius=1
    g249: Circle CenterX=318.073 CenterY=-47.4805 CenterZ=0 NormalX=0 NormalY=0 NormalZ=1 AngleXU=0 Radius=1
    g250: BSplineCurve PolesCount=3 KnotsCount=2 Degree=2 IsPeriodic=0
    g251: GeomPoint X=321.579 Y=-53.4075 Z=0
    g252: GeomPoint X=318.073 Y=-47.4805 Z=0
    g253: LineSegment StartX=371.567 StartY=-80.8644 StartZ=0 EndX=321.579 EndY=-53.4075 EndZ=0
    g254: Circle CenterX=321.579 CenterY=-67.3492 CenterZ=0 NormalX=0 NormalY=0 NormalZ=1 AngleXU=0 Radius=1
    g255: Circle CenterX=318.073 CenterY=-65.424 CenterZ=0 NormalX=0 NormalY=0 NormalZ=1 AngleXU=0 Radius=1
    g256: Circle CenterX=318.073 CenterY=-69.424 CenterZ=0 NormalX=0 NormalY=0 NormalZ=1 AngleXU=0 Radius=1
    g257: BSplineCurve PolesCount=3 KnotsCount=2 Degree=2 IsPeriodic=0
    g258: GeomPoint X=321.579 Y=-67.3492 Z=0
    g259: GeomPoint X=318.073 Y=-69.424 Z=0
    g260: Circle CenterX=362.567 CenterY=-89.8542 CenterZ=0 NormalX=0 NormalY=0 NormalZ=1 AngleXU=0 Radius=1
    g261: Circle CenterX=366.073 CenterY=-91.7794 CenterZ=0 NormalX=0 NormalY=0 NormalZ=1 AngleXU=0 Radius=1
    g262: Circle CenterX=362.073 CenterY=-91.7794 CenterZ=0 NormalX=0 NormalY=0 NormalZ=1 AngleXU=0 Radius=1
    g263: BSplineCurve PolesCount=3 KnotsCount=2 Degree=2 IsPeriodic=0
    g264: GeomPoint X=362.567 Y=-89.8542 Z=0
    g265: GeomPoint X=362.073 Y=-91.7794 Z=0
    g266: Circle CenterX=322.073 CenterY=-91.7794 CenterZ=0 NormalX=0 NormalY=0 NormalZ=1 AngleXU=0 Radius=1
    g267: Circle CenterX=318.073 CenterY=-91.7794 CenterZ=0 NormalX=0 NormalY=0 NormalZ=1 AngleXU=0 Radius=1
    g268: Circle CenterX=318.073 CenterY=-87.7794 CenterZ=0 NormalX=0 NormalY=0 NormalZ=1 AngleXU=0 Radius=1
    g269: BSplineCurve PolesCount=3 KnotsCount=2 Degree=2 IsPeriodic=0
    g270: GeomPoint X=322.073 Y=-91.7794 Z=0
    g271: GeomPoint X=318.073 Y=-87.7794 Z=0
    g272: LineSegment StartX=362.567 StartY=-89.8542 StartZ=0 EndX=321.579 EndY=-67.3492 EndZ=0
    g273: LineSegment StartX=318.073 StartY=-69.424 StartZ=0 EndX=318.073 EndY=-87.7794 EndZ=0
    g274: LineSegment StartX=322.073 StartY=-91.7794 StartZ=0 EndX=362.073 EndY=-91.7794 EndZ=0
    g275: Circle CenterX=2.07281 CenterY=124.221 CenterZ=0 NormalX=0 NormalY=0 NormalZ=1 AngleXU=0 Radius=1
    g276: Circle CenterX=1.57905 CenterY=122.295 CenterZ=0 NormalX=0 NormalY=0 NormalZ=1 AngleXU=0 Radius=1
    g277: BSplineCurve PolesCount=3 KnotsCount=2 Degree=2 IsPeriodic=0
    g278: GeomPoint X=2.07281 Y=124.221 Z=0
    g279: GeomPoint X=1.57905 Y=122.295 Z=0
    g280: Circle CenterX=42.0728 CenterY=124.221 CenterZ=0 NormalX=0 NormalY=0 NormalZ=1 AngleXU=0 Radius=1
    g281: Circle CenterX=46.0728 CenterY=124.221 CenterZ=0 NormalX=0 NormalY=0 NormalZ=1 AngleXU=0 Radius=1
    g282: Circle CenterX=46.0728 CenterY=120.221 CenterZ=0 NormalX=0 NormalY=0 NormalZ=1 AngleXU=0 Radius=1
    g283: BSplineCurve PolesCount=3 KnotsCount=2 Degree=2 IsPeriodic=0
    g284: GeomPoint X=42.0728 Y=124.221 Z=0
    g285: GeomPoint X=46.0728 Y=120.221 Z=0
    g286: Circle CenterX=46.0728 CenterY=109.865 CenterZ=0 NormalX=0 NormalY=0 NormalZ=1 AngleXU=0 Radius=1
    g287: Circle CenterX=46.0728 CenterY=105.865 CenterZ=0 NormalX=0 NormalY=0 NormalZ=1 AngleXU=0 Radius=1
    g288: Circle CenterX=42.0728 CenterY=105.865 CenterZ=0 NormalX=0 NormalY=0 NormalZ=1 AngleXU=0 Radius=1
    g289: BSplineCurve PolesCount=3 KnotsCount=2 Degree=2 IsPeriodic=0
    g290: GeomPoint X=46.0728 Y=109.865 Z=0
    g291: GeomPoint X=42.0728 Y=105.865 Z=0
    g292: Circle CenterX=35.5028 CenterY=105.865 CenterZ=0 NormalX=0 NormalY=0 NormalZ=1 AngleXU=0 Radius=1
    g293: Circle CenterX=31.5028 CenterY=105.865 CenterZ=0 NormalX=0 NormalY=0 NormalZ=1 AngleXU=0 Radius=1
    g294: Circle CenterX=27.9965 CenterY=107.79 CenterZ=0 NormalX=0 NormalY=0 NormalZ=1 AngleXU=0 Radius=1
    g295: BSplineCurve PolesCount=3 KnotsCount=2 Degree=2 IsPeriodic=0
    g296: GeomPoint X=35.5028 Y=105.865 Z=0
    g297: GeomPoint X=27.9965 Y=107.79 Z=0
    g298: LineSegment StartX=2.07281 StartY=124.221 StartZ=0 EndX=42.0728 EndY=124.221 EndZ=0
    g299: LineSegment StartX=46.0728 StartY=120.221 StartZ=0 EndX=46.0728 EndY=109.865 EndZ=0
    g300: LineSegment StartX=42.0728 StartY=105.865 StartZ=0 EndX=35.5028 EndY=105.865 EndZ=0
    g301: LineSegment StartX=27.9965 StartY=107.79 StartZ=0 EndX=1.57905 EndY=122.295 EndZ=0
    g302: Circle CenterX=42.5666 CenterY=-67.3492 CenterZ=0 NormalX=0 NormalY=0 NormalZ=1 AngleXU=0 Radius=1
    g303: Circle CenterX=46.0728 CenterY=-65.424 CenterZ=0 NormalX=0 NormalY=0 NormalZ=1 AngleXU=0 Radius=1
    g304: Circle CenterX=46.0728 CenterY=-69.424 CenterZ=0 NormalX=0 NormalY=0 NormalZ=1 AngleXU=0 Radius=1
    g305: BSplineCurve PolesCount=3 KnotsCount=2 Degree=2 IsPeriodic=0
    g306: GeomPoint X=42.5666 Y=-67.3492 Z=0
    g307: GeomPoint X=46.0728 Y=-69.424 Z=0
    g308: Circle CenterX=46.0728 CenterY=-87.7794 CenterZ=0 NormalX=0 NormalY=0 NormalZ=1 AngleXU=0 Radius=1
    g309: Circle CenterX=46.0728 CenterY=-91.7794 CenterZ=0 NormalX=0 NormalY=0 NormalZ=1 AngleXU=0 Radius=1
    g310: Circle CenterX=42.0728 CenterY=-91.7794 CenterZ=0 NormalX=0 NormalY=0 NormalZ=1 AngleXU=0 Radius=1
    g311: BSplineCurve PolesCount=3 KnotsCount=2 Degree=2 IsPeriodic=0
    g312: GeomPoint X=46.0728 Y=-87.7794 Z=0
    g313: GeomPoint X=42.0728 Y=-91.7794 Z=0
    g314: Circle CenterX=2.07281 CenterY=-91.7794 CenterZ=0 NormalX=0 NormalY=0 NormalZ=1 AngleXU=0 Radius=1
    g315: Circle CenterX=-1.92719 CenterY=-91.7794 CenterZ=0 NormalX=0 NormalY=0 NormalZ=1 AngleXU=0 Radius=1
    g316: Circle CenterX=1.57905 CenterY=-89.8542 CenterZ=0 NormalX=0 NormalY=0 NormalZ=1 AngleXU=0 Radius=1
    g317: BSplineCurve PolesCount=3 KnotsCount=2 Degree=2 IsPeriodic=0
    g318: GeomPoint X=2.07281 Y=-91.7794 Z=0
    g319: GeomPoint X=1.57905 Y=-89.8542 Z=0
    g320: LineSegment StartX=2.07281 StartY=-91.7794 StartZ=0 EndX=42.0728 EndY=-91.7794 EndZ=0
    g321: LineSegment StartX=46.0728 StartY=-87.7794 StartZ=0 EndX=46.0728 EndY=-69.424 EndZ=0
    g322: LineSegment StartX=42.5666 StartY=-67.3492 StartZ=0 EndX=1.57905 EndY=-89.8542 EndZ=0
    g323: Circle CenterX=322.073 CenterY=76.4095 CenterZ=0 NormalX=0 NormalY=0 NormalZ=1 AngleXU=0 Radius=4
    g324: BSplineCurve PolesCount=3 KnotsCount=2 Degree=2 IsPeriodic=0
    g325: GeomPoint X=318.073 Y=72.4095 Z=0
    g326: GeomPoint X=322.073 Y=76.4095 Z=0
    g327: Circle CenterX=375.073 CenterY=72.4095 CenterZ=0 NormalX=0 NormalY=0 NormalZ=1 AngleXU=0 Radius=1
    g328: Circle CenterX=375.073 CenterY=76.4095 CenterZ=0 NormalX=0 NormalY=0 NormalZ=1 AngleXU=0 Radius=1
    g329: Circle CenterX=371.073 CenterY=76.4095 CenterZ=0 NormalX=0 NormalY=0 NormalZ=1 AngleXU=0 Radius=1
    g330: BSplineCurve PolesCount=3 KnotsCount=2 Degree=2 IsPeriodic=0
    g331: GeomPoint X=375.073 Y=72.4095 Z=0
    g332: GeomPoint X=371.073 Y=76.4095 Z=0
    g333: LineSegment StartX=322.073 StartY=76.4095 StartZ=0 EndX=371.073 EndY=76.4095 EndZ=0
    g334: LineSegment StartX=318.073 StartY=72.4095 StartZ=0 EndX=318.073 EndY=-47.4805 EndZ=0
    g335: LineSegment StartX=375.073 StartY=72.4095 StartZ=0 EndX=375.073 EndY=-78.7896 EndZ=0
    g336: ArcOfCircle CenterX=-26.9272 CenterY=22.1087 CenterZ=0 NormalX=0 NormalY=0 NormalZ=1 AngleXU=0 Radius=4 StartAngle=5e-16 EndAngle=3.14159
    g337: LineSegment StartX=-22.9272 StartY=22.1087 StartZ=0 EndX=-18.9272 EndY=-83.7794 EndZ=0
    g338: LineSegment StartX=-34.9272 StartY=-83.7794 StartZ=0 EndX=-30.9272 EndY=22.1087 EndZ=0
    g339: ArcOfCircle CenterX=391.073 CenterY=22.1087 CenterZ=0 NormalX=0 NormalY=0 NormalZ=1 AngleXU=0 Radius=4 StartAngle=0 EndAngle=3.14159
    g340: LineSegment StartX=387.073 StartY=22.1087 StartZ=0 EndX=383.073 EndY=-83.7794 EndZ=0
    g341: LineSegment StartX=395.073 StartY=22.1087 StartZ=0 EndX=399.073 EndY=-83.7794 EndZ=0
    g342: Circle CenterX=-10.9272 CenterY=-78.7794 CenterZ=0 NormalX=0 NormalY=0 NormalZ=1 AngleXU=0 Radius=1
    g343: Circle CenterX=-10.9272 CenterY=-82.7794 CenterZ=0 NormalX=0 NormalY=0 NormalZ=1 AngleXU=0 Radius=1
    g344: Circle CenterX=-7.42095 CenterY=-80.8542 CenterZ=0 NormalX=0 NormalY=0 NormalZ=1 AngleXU=0 Radius=1
    g345: BSplineCurve PolesCount=3 KnotsCount=2 Degree=2 IsPeriodic=0
    g346: GeomPoint X=-10.9272 Y=-78.7794 Z=0
    g347: GeomPoint X=-7.42095 Y=-80.8542 Z=0
    g348: Circle CenterX=42.5666 CenterY=-53.4075 CenterZ=0 NormalX=0 NormalY=0 NormalZ=1 AngleXU=0 Radius=1
    g349: Circle CenterX=46.0728 CenterY=-51.4823 CenterZ=0 NormalX=0 NormalY=0 NormalZ=1 AngleXU=0 Radius=1
    g350: Circle CenterX=46.0728 CenterY=-47.4823 CenterZ=0 NormalX=0 NormalY=0 NormalZ=1 AngleXU=0 Radius=1
    g351: BSplineCurve PolesCount=3 KnotsCount=2 Degree=2 IsPeriodic=0
    g352: GeomPoint X=42.5666 Y=-53.4075 Z=0
    g353: GeomPoint X=46.0728 Y=-47.4823 Z=0
    g354: Circle CenterX=46.0728 CenterY=72.4095 CenterZ=0 NormalX=0 NormalY=0 NormalZ=1 AngleXU=0 Radius=1
    g355: Circle CenterX=46.0728 CenterY=76.4095 CenterZ=0 NormalX=0 NormalY=0 NormalZ=1 AngleXU=0 Radius=1
    g356: Circle CenterX=42.0728 CenterY=76.4095 CenterZ=0 NormalX=0 NormalY=0 NormalZ=1 AngleXU=0 Radius=1
    g357: BSplineCurve PolesCount=3 KnotsCount=2 Degree=2 IsPeriodic=0
    g358: GeomPoint X=46.0728 Y=72.4095 Z=0
    g359: GeomPoint X=42.0728 Y=76.4095 Z=0
    g360: Circle CenterX=-6.92719 CenterY=76.4095 CenterZ=0 NormalX=0 NormalY=0 NormalZ=1 AngleXU=0 Radius=1
    g361: Circle CenterX=-10.9272 CenterY=76.4095 CenterZ=0 NormalX=0 NormalY=0 NormalZ=1 AngleXU=0 Radius=1
    g362: Circle CenterX=-10.9272 CenterY=72.4095 CenterZ=0 NormalX=0 NormalY=0 NormalZ=1 AngleXU=0 Radius=1
    g363: BSplineCurve PolesCount=3 KnotsCount=2 Degree=2 IsPeriodic=0
    g364: GeomPoint X=-6.92719 Y=76.4095 Z=0
    g365: GeomPoint X=-10.9272 Y=72.4095 Z=0
    g366: LineSegment StartX=-10.9272 StartY=72.4095 StartZ=0 EndX=-10.9272 EndY=-78.7794 EndZ=0
    g367: LineSegment StartX=-7.42095 StartY=-80.8542 StartZ=0 EndX=42.5666 EndY=-53.4075 EndZ=0
    g368: LineSegment StartX=46.0728 StartY=-47.4823 StartZ=0 EndX=46.0728 EndY=72.4095 EndZ=0
    g369: LineSegment StartX=42.0728 StartY=76.4095 StartZ=0 EndX=-6.92719 EndY=76.4095 EndZ=0
    g370: LineSegment StartX=-42.9272 StartY=136.221 StartZ=0 EndX=407.073 EndY=136.221 EndZ=0
    g371: LineSegment StartX=232.072 StartY=136.221 StartZ=0 EndX=220.072 EndY=136.221 EndZ=0
    g372: LineSegment StartX=232.072 StartY=136.221 StartZ=0 EndX=232.072 EndY=124.221 EndZ=0
    g373: LineSegment StartX=220.072 StartY=136.221 StartZ=0 EndX=220.072 EndY=124.221 EndZ=0
    g374: LineSegment StartX=220.072 StartY=136.221 StartZ=0 EndX=226.072 EndY=136.221 EndZ=0
    g375: LineSegment StartX=220.072 StartY=136.221 StartZ=0 EndX=220.072 EndY=130.221 EndZ=0
    g376: LineSegment StartX=220.072 StartY=124.221 StartZ=0 EndX=226.072 EndY=124.221 EndZ=0
    g377: LineSegment StartX=232.072 StartY=124.221 StartZ=0 EndX=232.072 EndY=127.221 EndZ=0
    g378: LineSegment StartX=232.072 StartY=136.221 StartZ=0 EndX=232.072 EndY=133.221 EndZ=0
    g379-g383: Circle x5 (B-spline internal-alignment scaffolding for g384; pole/knot coordinates omitted)
    g384: BSplineCurve PolesCount=5 KnotsCount=3 Degree=3 IsPeriodic=0
    g385: GeomPoint X=232.072 Y=133.221 Z=0
    g386: GeomPoint X=223.072 Y=130.221 Z=0
    g387: GeomPoint X=232.072 Y=127.221 Z=0
    g388: LineSegment StartX=189.124 StartY=124.221 StartZ=0 EndX=302.073 EndY=124.221 EndZ=0
    g389: LineSegment StartX=132.072 StartY=136.221 StartZ=0 EndX=132.072 EndY=124.221 EndZ=0
    g390: LineSegment StartX=132.072 StartY=136.221 StartZ=0 EndX=144.072 EndY=136.221 EndZ=0
    g391: LineSegment StartX=144.072 StartY=136.221 StartZ=0 EndX=144.072 EndY=124.221 EndZ=0
    g392: LineSegment StartX=144.072 StartY=136.221 StartZ=0 EndX=138.072 EndY=136.221 EndZ=0
    g393: LineSegment StartX=144.072 StartY=136.221 StartZ=0 EndX=144.072 EndY=130.221 EndZ=0
    g394: LineSegment StartX=132.072 StartY=136.221 StartZ=0 EndX=132.072 EndY=133.221 EndZ=0
    g395: LineSegment StartX=132.072 StartY=133.221 StartZ=0 EndX=132.072 EndY=127.221 EndZ=0
    g396-g400: Circle x5 (B-spline internal-alignment scaffolding for g401; pole/knot coordinates omitted)
    g401: BSplineCurve PolesCount=5 KnotsCount=3 Degree=3 IsPeriodic=0
    g402: GeomPoint X=132.072 Y=133.221 Z=0
    g403: GeomPoint X=141.072 Y=130.221 Z=0
    g404: GeomPoint X=132.072 Y=127.221 Z=0
    g405: LineSegment StartX=132.072 StartY=124.221 StartZ=0 EndX=175.022 EndY=124.221 EndZ=0
    g406: LineSegment StartX=62.0728 StartY=124.221 StartZ=0 EndX=132.072 EndY=124.221 EndZ=0
    g407: LineSegment StartX=132.072 StartY=136.221 StartZ=0 EndX=131.457 EndY=138.832 EndZ=0
    ... +61 more geometry lines
  constraints (808):
    c: Vertical(g0)
    c: Vertical(g1)
    c: Block(g1)
    c: Block(g0)
    c: Weight(g4) = 1
    c: Equal(g4,g5)
    c: Equal(g4,g6)
    c: InternalAlignment(g4,g7)
    c: InternalAlignment(g5,g7)
    c: InternalAlignment(g6,g7)
    c: InternalAlignment(g8,g7)
    c: InternalAlignment(g9,g7)
    c: Weight(g10) = 1
    c: Equal(g10,g11)
    c: Equal(g10,g12)
    c: InternalAlignment(g10,g13)
    c: InternalAlignment(g11,g13)
    c: InternalAlignment(g12,g13)
    c: InternalAlignment(g14,g13)
    c: InternalAlignment(g15,g13)
    c: Block(g13)
    c: Block(g7)
    c: Weight(g16) = 1
    c: Equal(g16,g17)
    c: Equal(g16,g18)
    c: InternalAlignment(g16,g19)
    c: InternalAlignment(g17,g19)
    c: InternalAlignment(g18,g19)
    c: InternalAlignment(g20,g19)
    c: InternalAlignment(g21,g19)
    c: Weight(g22) = 1
    c: Equal(g22,g23)
    c: Equal(g22,g24)
    c: InternalAlignment(g22,g25)
    c: InternalAlignment(g23,g25)
    c: InternalAlignment(g24,g25)
    c: InternalAlignment(g26,g25)
    c: InternalAlignment(g27,g25)
    c: Block(g25)
    c: Block(g19)
    c: Weight(g28) = 1
    c: Equal(g28,g29)
    c: Equal(g28,g30)
    c: InternalAlignment(g28,g31)
    c: InternalAlignment(g29,g31)
    c: InternalAlignment(g30,g31)
    c: InternalAlignment(g32,g31)
    c: InternalAlignment(g33,g31)
    c: Weight(g34) = 1
    c: Equal(g34,g35)
    c: Equal(g34,g36)
    c: InternalAlignment(g34,g37)
    c: InternalAlignment(g35,g37)
    c: InternalAlignment(g36,g37)
    c: InternalAlignment(g38,g37)
    c: InternalAlignment(g39,g37)
    c: Block(g31)
    c: Block(g37)
    c: Coincident(g40,g1)
    c: Coincident(g40,g0)
    c: Horizontal(g40)
    c: Distance(g40) = 450
    c: Weight(g41) = 1
    c: Equal(g41,g42)
    c: Equal(g41,g43)
    c: InternalAlignment(g41,g44)
    c: InternalAlignment(g42,g44)
    c: InternalAlignment(g43,g44)
    c: InternalAlignment(g45,g44)
    c: InternalAlignment(g46,g44)
    c: Block(g44)
    c: Weight(g47) = 1
    c: Equal(g47,g48)
    c: Equal(g47,g49)
    c: InternalAlignment(g47,g50)
    c: InternalAlignment(g48,g50)
    c: InternalAlignment(g49,g50)
    c: InternalAlignment(g51,g50)
    c: InternalAlignment(g52,g50)
    c: Block(g50)
    c: Weight(g53) = 1
    c: Equal(g53,g54)
    c: Equal(g53,g55)
    c: InternalAlignment(g53,g56)
    c: InternalAlignment(g54,g56)
    c: InternalAlignment(g55,g56)
    c: InternalAlignment(g57,g56)
    c: InternalAlignment(g58,g56)
    c: Block(g56)
    c: Weight(g59) = 1
    c: Equal(g59,g60)
    c: Equal(g59,g61)
    c: InternalAlignment(g59,g62)
    c: InternalAlignment(g60,g62)
    c: InternalAlignment(g61,g62)
    c: InternalAlignment(g63,g62)
    c: InternalAlignment(g64,g62)
    c: Block(g62)
    c: Weight(g65) = 1
    c: Equal(g65,g66)
    c: Equal(g65,g67)
    c: InternalAlignment(g65,g68)
    c: InternalAlignment(g66,g68)
    c: InternalAlignment(g67,g68)
    c: InternalAlignment(g69,g68)
    c: InternalAlignment(g70,g68)
    c: Weight(g71) = 1
    c: Equal(g71,g72)
    c: Equal(g71,g73)
    c: InternalAlignment(g71,g74)
    c: InternalAlignment(g72,g74)
    c: InternalAlignment(g73,g74)
    c: InternalAlignment(g75,g74)
    c: InternalAlignment(g76,g74)
    c: Block(g68)
    c: Block(g74)
    c: Coincident(g77,g68)
    c: Coincident(g77,g74)
    c: Vertical(g77)
    c: Coincident(g78,g68)
    c: Coincident(g78,g50)
    c: Coincident(g79,g50)
    c: Coincident(g79,g74)
    c: Weight(g80) = 1
    c: Equal(g80,g81)
    c: Equal(g80,g82)
    c: InternalAlignment(g80,g83)
    c: InternalAlignment(g81,g83)
    c: InternalAlignment(g82,g83)
    c: InternalAlignment(g84,g83)
    c: InternalAlignment(g85,g83)
    c: Weight(g86) = 1
    c: Equal(g86,g87)
    c: Equal(g86,g88)
    c: InternalAlignment(g86,g89)
    c: InternalAlignment(g87,g89)
    c: InternalAlignment(g88,g89)
    c: InternalAlignment(g90,g89)
    c: InternalAlignment(g91,g89)
    c: Block(g83)
    c: Block(g89)
    c: Coincident(g92,g83)
    c: Coincident(g92,g89)
    c: Vertical(g92)
    c: Coincident(g93,g83)
    c: Coincident(g93,g44)
    c: Coincident(g94,g44)
    c: Coincident(g94,g89)
    c: Weight(g95) = 1
    c: Equal(g95,g96)
    c: Equal(g95,g97)
    c: InternalAlignment(g95,g98)
    c: InternalAlignment(g96,g98)
    c: InternalAlignment(g97,g98)
    c: InternalAlignment(g99,g98)
    c: InternalAlignment(g100,g98)
    c: Weight(g101) = 1
    c: Equal(g101,g102)
    c: Equal(g101,g103)
    c: InternalAlignment(g101,g104)
    c: InternalAlignment(g102,g104)
    c: InternalAlignment(g103,g104)
    c: InternalAlignment(g105,g104)
    c: InternalAlignment(g106,g104)
    c: Block(g98)
    c: Block(g104)
    c: Coincident(g107,g98)
    c: Coincident(g107,g104)
    c: Vertical(g107)
    c: Coincident(g108,g104)
    c: Coincident(g108,g62)
    c: Coincident(g109,g62)
    c: Coincident(g109,g98)
    c: Weight(g110) = 1
    c: Equal(g110,g111)
    c: Equal(g110,g112)
    c: InternalAlignment(g110,g113)
    c: InternalAlignment(g111,g113)
    c: InternalAlignment(g112,g113)
    c: InternalAlignment(g114,g113)
    c: InternalAlignment(g115,g113)
    c: Weight(g116) = 1
    c: Equal(g116,g117)
    c: Equal(g116,g118)
    c: InternalAlignment(g116,g119)
    c: InternalAlignment(g117,g119)
    c: InternalAlignment(g118,g119)
    c: InternalAlignment(g120,g119)
    c: InternalAlignment(g121,g119)
    c: Block(g113)
    c: Block(g119)
    c: Coincident(g122,g113)
    c: Coincident(g122,g119)
    c: Vertical(g122)
    c: Coincident(g123,g119)
    c: Coincident(g123,g56)
    c: Coincident(g124,g56)
    c: Coincident(g124,g113)
    c: Weight(g125) = 1
    c: Equal(g125,g126)
    c: Equal(g125,g127)
    c: InternalAlignment(g125,g128)
    c: InternalAlignment(g126,g128)
    c: InternalAlignment(g127,g128)
    c: InternalAlignment(g129,g128)
    c: InternalAlignment(g130,g128)
    c: Weight(g131) = 1
    c: Equal(g131,g132)
    c: Equal(g131,g133)
    c: InternalAlignment(g131,g134)
    c: InternalAlignment(g132,g134)
    c: InternalAlignment(g133,g134)
    c: InternalAlignment(g135,g134)
    c: InternalAlignment(g136,g134)
    c: Weight(g137) = 1
    c: Equal(g137,g138)
    c: Equal(g137,g139)
    c: InternalAlignment(g137,g140)
    c: InternalAlignment(g138,g140)
    c: InternalAlignment(g139,g140)
    c: InternalAlignment(g141,g140)
    c: InternalAlignment(g142,g140)
    c: Weight(g143) = 1
    c: Equal(g143,g144)
    c: Equal(g143,g145)
    c: InternalAlignment(g143,g146)
    c: InternalAlignment(g144,g146)
    c: InternalAlignment(g145,g146)
    c: InternalAlignment(g147,g146)
    c: InternalAlignment(g148,g146)
    c: Block(g146)
    c: Block(g140)
    c: Block(g134)
    c: Block(g128)
    c: Coincident(g149,g25)
    c: Coincident(g149,g146)
    c: Coincident(g150,g146)
    c: Coincident(g150,g140)
    c: Horizontal(g150)
    c: Coincident(g151,g140)
    c: Coincident(g151,g25)
    c: Vertical(g151)
    c: Coincident(g152,g19)
    c: Coincident(g152,g134)
    c: Vertical(g152)
    c: Coincident(g153,g134)
    c: Coincident(g153,g128)
    c: Horizontal(g153)
    c: Coincident(g154,g128)
    c: Coincident(g154,g19)
    c: Weight(g155) = 1
    c: Equal(g155,g156)
    c: Equal(g155,g157)
    c: InternalAlignment(g155,g158)
    c: InternalAlignment(g156,g158)
    c: InternalAlignment(g157,g158)
    c: InternalAlignment(g159,g158)
    c: InternalAlignment(g160,g158)
    c: Weight(g161) = 1
    c: Equal(g161,g162)
    c: Equal(g161,g163)
    c: InternalAlignment(g161,g164)
    c: InternalAlignment(g162,g164)
    c: InternalAlignment(g163,g164)
    c: InternalAlignment(g165,g164)
    c: InternalAlignment(g166,g164)
    c: Weight(g167) = 1
    c: Equal(g167,g168)
    c: Equal(g167,g169)
    c: InternalAlignment(g167,g170)
    c: InternalAlignment(g168,g170)
    c: InternalAlignment(g169,g170)
    c: InternalAlignment(g171,g170)
    c: InternalAlignment(g172,g170)
    c: Weight(g173) = 1
    c: Equal(g173,g174)
    c: Equal(g173,g175)
    c: InternalAlignment(g173,g176)
    c: InternalAlignment(g174,g176)
    c: InternalAlignment(g175,g176)
    c: InternalAlignment(g177,g176)
    c: InternalAlignment(g178,g176)
    c: Block(g176)
    c: Block(g170)
    c: Block(g164)
    c: Block(g158)
    c: Coincident(g179,g170)
    c: Coincident(g179,g7)
    c: Vertical(g179)
    c: Coincident(g180,g13)
    c: Coincident(g180,g164)
    c: Vertical(g180)
    c: Coincident(g181,g158)
    c: Coincident(g181,g13)
    c: Coincident(g182,g7)
    c: Weight(g183) = 1
    c: Equal(g183,g184)
    c: Equal(g183,g185)
    c: InternalAlignment(g183,g186)
    c: InternalAlignment(g184,g186)
    c: InternalAlignment(g185,g186)
    c: InternalAlignment(g187,g186)
    c: InternalAlignment(g188,g186)
    c: Weight(g189) = 1
    c: Equal(g189,g190)
    c: Equal(g189,g191)
    c: InternalAlignment(g189,g192)
    c: InternalAlignment(g190,g192)
    c: InternalAlignment(g191,g192)
    c: InternalAlignment(g193,g192)
    c: InternalAlignment(g194,g192)
    c: Block(g192)
    c: Block(g186)
    c: Coincident(g195,g192)
    c: Coincident(g195,g31)
    c: Coincident(g196,g31)
    c: Coincident(g196,g186)
    c: Coincident(g197,g186)
    c: Coincident(g197,g192)
    c: Vertical(g197)
    c: Weight(g198) = 1
    c: Equal(g198,g199)
    c: Equal(g198,g200)
    c: InternalAlignment(g198,g201)
    c: InternalAlignment(g199,g201)
    c: InternalAlignment(g200,g201)
    c: InternalAlignment(g202,g201)
    c: InternalAlignment(g203,g201)
    c: Weight(g204) = 1
    c: Equal(g204,g205)
    c: Equal(g204,g206)
    c: InternalAlignment(g204,g207)
    c: InternalAlignment(g205,g207)
    c: InternalAlignment(g206,g207)
    c: InternalAlignment(g208,g207)
    c: InternalAlignment(g209,g207)
    c: Block(g207)
    c: Block(g201)
    c: Coincident(g210,g201)
    c: Coincident(g210,g37)
    c: Coincident(g211,g37)
    c: Coincident(g211,g207)
    c: Coincident(g212,g207)
    c: Coincident(g212,g201)
    c: Vertical(g212)
    c: Horizontal(g213)
    c: Block(g213)
    c: Vertical(g214)
    c: Block(g214)
    c: Block(g215)
    c: Weight(g216) = 1
    c: Equal(g216,g217)
    c: Equal(g216,g218)
    c: InternalAlignment(g216,g219)
    c: InternalAlignment(g217,g219)
    c: InternalAlignment(g218,g219)
    c: InternalAlignment(g220,g219)
    c: InternalAlignment(g221,g219)
    c: Weight(g222) = 1
    c: Equal(g222,g223)
    c: Equal(g222,g224)
    c: InternalAlignment(g222,g225)
    c: InternalAlignment(g223,g225)
    c: InternalAlignment(g224,g225)
    c: InternalAlignment(g226,g225)
    c: InternalAlignment(g227,g225)
    c: Weight(g228) = 1
    c: Equal(g228,g229)
    c: Equal(g228,g230)
    c: InternalAlignment(g228,g231)
    c: InternalAlignment(g229,g231)
    c: InternalAlignment(g230,g231)
    c: InternalAlignment(g232,g231)
    c: InternalAlignment(g233,g231)
    c: Weight(g234) = 1
    c: Equal(g234,g235)
    c: Equal(g234,g236)
    c: InternalAlignment(g234,g237)
    c: InternalAlignment(g235,g237)
    c: InternalAlignment(g236,g237)
    c: InternalAlignment(g238,g237)
    c: InternalAlignment(g239,g237)
    c: Block(g219)
    c: Block(g225)
    c: Block(g231)
    c: Block(g237)
    c: Coincident(g240,g225)
    c: Coincident(g240,g219)
    c: Horizontal(g240)
    c: Block(g182)
    c: Weight(g241) = 1
    c: Equal(g241,g242)
    c: Equal(g241,g243)
    c: InternalAlignment(g241,g244)
    c: InternalAlignment(g242,g244)
    c: InternalAlignment(g243,g244)
    c: InternalAlignment(g245,g244)
    c: InternalAlignment(g246,g244)
    c: Weight(g247) = 1
    c: Equal(g247,g248)
    c: Equal(g247,g249)
    c: InternalAlignment(g247,g250)
    c: InternalAlignment(g248,g250)
    c: InternalAlignment(g249,g250)
    c: InternalAlignment(g251,g250)
    c: InternalAlignment(g252,g250)
    c: Block(g244)
    c: Block(g250)
    c: Coincident(g253,g244)
    c: Coincident(g253,g250)
    c: Weight(g254) = 1
    c: Equal(g254,g255)
    c: Equal(g254,g256)
    c: InternalAlignment(g254,g257)
    c: InternalAlignment(g255,g257)
    c: InternalAlignment(g256,g257)
    c: InternalAlignment(g258,g257)
    c: InternalAlignment(g259,g257)
    c: Weight(g260) = 1
    c: Equal(g260,g261)
    c: Equal(g260,g262)
    c: InternalAlignment(g260,g263)
    c: InternalAlignment(g261,g263)
    c: InternalAlignment(g262,g263)
    c: InternalAlignment(g264,g263)
    c: InternalAlignment(g265,g263)
    c: Weight(g266) = 1
    c: Equal(g266,g267)
    c: Equal(g266,g268)
    c: InternalAlignment(g266,g269)
    c: InternalAlignment(g267,g269)
    c: InternalAlignment(g268,g269)
    c: InternalAlignment(g270,g269)
    c: InternalAlignment(g271,g269)
    c: Block(g269)
    c: Block(g263)
    c: Block(g257)
    c: Coincident(g272,g263)
    c: Coincident(g272,g257)
    c: Coincident(g273,g257)
    c: Coincident(g273,g269)
    c: Vertical(g273)
    c: Coincident(g274,g269)
    c: Coincident(g274,g263)
    c: Horizontal(g274)
    c: Weight(g275) = 1
    c: Equal(g275,g276)
    c: InternalAlignment(g275,g277)
    c: InternalAlignment(g276,g277)
    c: InternalAlignment(g278,g277)
    c: InternalAlignment(g279,g277)
    c: Weight(g280) = 1
    c: InternalAlignment(g281,g283)
    c: InternalAlignment(g282,g283)
    c: InternalAlignment(g284,g283)
    c: InternalAlignment(g285,g283)
    c: Weight(g286) = 1
    c: Equal(g286,g287)
    c: Equal(g286,g288)
    c: InternalAlignment(g286,g289)
    c: InternalAlignment(g287,g289)
    c: InternalAlignment(g288,g289)
    c: InternalAlignment(g290,g289)
    c: InternalAlignment(g291,g289)
    c: Equal(g292,g293)
    c: Equal(g292,g294)
    c: InternalAlignment(g292,g295)
    c: InternalAlignment(g293,g295)
    c: InternalAlignment(g294,g295)
    c: InternalAlignment(g296,g295)
    c: InternalAlignment(g297,g295)
    c: Block(g283)
    c: Block(g289)
    c: Block(g295)
    c: Block(g277)
    c: Coincident(g298,g277)
    c: Coincident(g298,g283)
    c: Horizontal(g298)
    c: Coincident(g299,g283)
    c: Coincident(g299,g289)
    c: Vertical(g299)
    c: Coincident(g300,g289)
    c: Coincident(g300,g295)
    c: Horizontal(g300)
    c: Coincident(g301,g295)
    c: Coincident(g301,g277)
    c: Weight(g302) = 1
    c: Equal(g302,g303)
    c: Equal(g302,g304)
    c: InternalAlignment(g302,g305)
    c: InternalAlignment(g303,g305)
    c: InternalAlignment(g304,g305)
    c: InternalAlignment(g306,g305)
    c: InternalAlignment(g307,g305)
    c: Weight(g308) = 1
    c: Equal(g308,g309)
    c: Equal(g308,g310)
    c: InternalAlignment(g308,g311)
    c: InternalAlignment(g309,g311)
    c: InternalAlignment(g310,g311)
    c: InternalAlignment(g312,g311)
    c: Weight(g314) = 1
    c: Equal(g314,g315)
    c: Equal(g314,g316)
    c: InternalAlignment(g314,g317)
    c: InternalAlignment(g315,g317)
    c: InternalAlignment(g316,g317)
    c: InternalAlignment(g318,g317)
    c: InternalAlignment(g319,g317)
    c: Block(g317)
    c: Block(g311)
    c: Block(g305)
    c: Coincident(g320,g317)
    c: Coincident(g320,g311)
    c: Horizontal(g320)
    c: Coincident(g321,g311)
    c: Coincident(g321,g305)
    c: Vertical(g321)
    c: Coincident(g322,g305)
    c: Coincident(g322,g317)
    c: InternalAlignment(g323,g324)
    c: InternalAlignment(g325,g324)
    c: InternalAlignment(g326,g324)
    c: Block(g324)
    c: Equal(g327,g328)
    c: Equal(g327,g329)
    c: InternalAlignment(g327,g330)
    c: InternalAlignment(g328,g330)
    c: InternalAlignment(g329,g330)
    c: InternalAlignment(g331,g330)
    c: InternalAlignment(g332,g330)
    c: Block(g330)
    c: Coincident(g333,g324)
    c: Horizontal(g333)
    c: Block(g333)
    c: Coincident(g334,g324)
    c: Coincident(g334,g250)
    c: Vertical(g334)
    c: Coincident(g335,g330)
    c: Coincident(g335,g244)
    c: Vertical(g335)
    c: Block(g336)
    c: Block(g2)
    c: Distance(g334) = 119.89
    c: Coincident(g337,g336)
    c: Coincident(g337,g2)
    c: Coincident(g338,g2)
    c: Coincident(g338,g336)
    c: Block(g3)
    c: Block(g339)
    c: Coincident(g340,g339)
    c: Coincident(g340,g3)
    c: Coincident(g341,g339)
    c: Coincident(g341,g3)
    c: Block(g341)
    c: Block(g340)
    c: Weight(g342) = 1
    c: Equal(g342,g344)
    c: InternalAlignment(g342,g345)
    c: InternalAlignment(g343,g345)
    c: InternalAlignment(g344,g345)
    c: InternalAlignment(g346,g345)
    c: InternalAlignment(g347,g345)
    c: InternalAlignment(g352,g351)
    c: InternalAlignment(g353,g351)
    c: InternalAlignment(g355,g357)
    c: Horizontal(g369)
    c: Coincident(g370,g0)
    c: Horizontal(g370)
    c: Block(g370)
    c: Distance(g370) = 450
    c: Horizontal(g371)
    c: Distance(g371) = 12
    c: Coincident(g373,g371)
    c: Vertical(g373)
    c: Horizontal(g374)
    c: Vertical(g375)
    c: Distance(g375) = 6
    c: Coincident(g375,g371)
    c: Coincident(g374,g371)
    c: Block(g373)
    c: Coincident(g376,g373)
    c: Horizontal(g376)
    c: Distance(g376) = 6
    c: Vertical(g377)
    c: Distance(g377) = 3
    c: Vertical(g378)
    c: Distance(g378) = 3
    c: Coincident(g372,g377)
    c: Coincident(g384,g378)
    c: Weight(g379) = 1
    c: Equal(g379,g380)
    c: Coincident(g380,g374)
    c: Equal(g379,g381)
    c: Coincident(g381,g375)
    c: Equal(g379,g382)
    c: Coincident(g382,g376)
    c: Equal(g379,g383)
    c: Coincident(g384,g377)
    c: InternalAlignment(g379-g383 -> g384) x5
    c: InternalAlignment(g385,g384)
    c: InternalAlignment(g386,g384)
    c: InternalAlignment(g387,g384)
    c: Coincident(g388,g164)
    c: Coincident(g388,g158)
    c: Coincident(g392,g390)
    c: Vertical(g393)
    c: Distance(g393) = 6
    c: Coincident(g393,g390)
    c: Vertical(g394)
    c: Distance(g394) = 3
    c: Vertical(g395)
    c: Distance(g395) = 6
    c: Coincident(g395,g394)
    c: Coincident(g401,g394)
    c: Weight(g396) = 1
    c: Equal(g396,g397)
    c: Coincident(g397,g392)
    c: Equal(g396,g398)
    c: Coincident(g398,g393)
    c: Equal(g396,g399)
    c: Equal(g396,g400)
    c: Coincident(g401,g395)
    c: InternalAlignment(g396-g400 -> g401) x5
    c: InternalAlignment(g402,g401)
    c: InternalAlignment(g403,g401)
    c: InternalAlignment(g404,g401)
    c: Coincident(g405,g389)
    c: Coincident(g405,g170)
    c: Horizontal(g405)
    c: Block(g401)
    c: Coincident(g406,g176)
    c: Coincident(g406,g389)
    c: Horizontal(g406)
    c: Block(g405)
    c: Coincident(g408,g389)
    c: PointOnObject(g408,g153)
    c: Vertical(g408)
    c: Block(g409)
    c: Coincident(g410,g409)
    c: Vertical(g410)
    c: PointOnObject(g410,g40)
    c: Block(g410)
    c: Coincident(g411,g409)
    c: Vertical(g411)
    c: Block(g411)
    c: Vertical(g412)
    c: Distance(g412) = 3
    c: Equal(g379,g415) = 1
    c: Equal(g415,g416)
    c: InternalAlignment(g415,g417)
    c: InternalAlignment(g416,g417)
    c: InternalAlignment(g413,g417)
    c: InternalAlignment(g414,g417)
    c: InternalAlignment(g418,g417)
    c: Block(g417)
    c: Coincident(g418,g412)
    c: Coincident(g419,g417)
    c: PointOnObject(g419,g150)
    c: Vertical(g419)
    c: Distance(g420) = 3
    c: Block(g420)
    c: Distance(g421) = 3
    c: Parallel(g421,g420)
    c: Coincident(g421,g420)
    c: Coincident(g422,g420)
    c: Perpendicular(g422,g420)
    c: Distance(g422) = 3
    c: Coincident(g423,g421)
    c: Perpendicular(g423,g421)
    c: Distance(g423) = 3
    c: Coincident(g424,g420)
    c: Perpendicular(g424,g421)
    c: Distance(g424) = 6
    c: Coincident(g425,g424)
    c: PointOnObject(g423,g425)
    c: Coincident(g426,g420)
    c: PointOnObject(g426,g79)
    c: Block(g426)
    c: Distance(g427) = 2.76
    c: Coincident(g428,g427)
    c: Parallel(g427,g428)
    c: PointOnObject(g428,g181)
    c: Distance(g428) = 2.41
    c: Block(g428)
    c: Coincident(g429,g427)
    c: Distance(g429) = 6.6
    c: Perpendicular(g429,g428)
    c: Distance(g430) = 6.6
    c: Coincident(g431,g429)
    c: Coincident(g431,g430)
    c: Block(g432)
    c: Coincident(g433,g432)
    c: Vertical(g433)
    c: Distance(g433) = 3.6
    c: Coincident(g434,g427)
    c: Parallel(g427,g434)
    c: PointOnObject(g434,g78)
    c: Block(g434)
    c: Coincident(g435,g421)
    c: Parallel(g435,g421)
    c: PointOnObject(g435,g211)
    c: Block(g435)
    c: Coincident(g436,g435)
    c: Vertical(g436)
    c: PointOnObject(g436,g210)
    c: Coincident(g437,g436)
    c: Perpendicular(g437,g210)
    c: Distance(g437) = 3
    c: Coincident(g438,g437)
    c: Block(g437)
    c: Distance(g438) = 3
    c: Parallel(g437,g438)
    c: Coincident(g439,g438)
    c: Distance(g439) = 3
    c: Parallel(g438,g439)
    c: Coincident(g440,g439)
    c: Parallel(g440,g437)
    c: PointOnObject(g440,g124)
    c: PointOnObject(g441,g53)
    c: Tangent(g440,g441)
    c: Coincident(g442,g439)
    c: Perpendicular(g442,g439)
    c: Coincident(g443,g437)
    c: Parallel(g443,g442)
    c: Distance(g443) = 3
    c: Distance(g442) = 3
    c: PointOnObject(g442,g444)
    c: Block(g444)
    c: PointOnObject(g445,g123)
    c: Perpendicular(g123,g445)
    c: Distance(g445) = 2.41
    c: Block(g445)
    c: Coincident(g446,g445)
    c: Perpendicular(g123,g446)
    c: Distance(g446) = 2.76
    c: Coincident(g447,g446)
    c: Perpendicular(g123,g447)
    c: PointOnObject(g447,g149)
    c: Coincident(g448,g445)
    c: Parallel(g123,g448)
    c: Distance(g448) = 6.6
    c: Coincident(g449,g446)
    c: Parallel(g123,g449)
    c: Coincident(g450,g448)
    c: Distance(g449) = 6.6
    c: Coincident(g449,g450)
    c: Block(g149)
    c: Block(g124)
    c: Block(g211)
    c: Block(g181)
    c: Block(g78)
    c: Block(g79)
    c: Block(g430)
    c: Coincident(g451,g447)
    c: Distance(g451) = 46
    c: Parallel(g149,g451)
    c: Coincident(g452,g451)
    c: Horizontal(g452)
    c: PointOnObject(g452,g154)
    c: Coincident(g453,g451)
    c: Vertical(g453)
    c: Distance(g453) = 9
    c: Block(g452)
    c: PointOnObject(g454,g93)
    c: Distance(g455) = 6.6
    c: Distance(g456) = 6.6
    c: Block(g454)
    c: Coincident(g457,g456)
    c: Coincident(g457,g455)
    c: Perpendicular(g457,g182)
    c: Coincident(g458,g455)
    c: Perpendicular(g458,g182)
    c: PointOnObject(g458,g182)
    c: Block(g458)
    c: Block(g457)
    c: Block(g456)
    c: PointOnObject(g459,g196)
    c: Perpendicular(g196,g459)
    c: Distance(g459) = 3
    c: Coincident(g460,g459)
    c: Perpendicular(g196,g460)
    c: Distance(g460) = 3
    c: Coincident(g461,g460)
    c: Perpendicular(g196,g461)
    c: Distance(g461) = 3
    c: Coincident(g462,g461)
    c: Tangent(g462,g41)
    c: PointOnObject(g462,g94)
    c: Block(g462)
    c: Block(g459)
    c: Coincident(g463,g459)
    c: Parallel(g196,g463)
    c: Distance(g463) = 3
    c: Coincident(g464,g461)
    c: Distance(g464) = 3
    c: Parallel(g196,g464)
    c: Coincident(g465,g460)
    c: Distance(g465) = 6
    c: Parallel(g465,g196)
    c: Coincident(g466,g465)
    c: PointOnObject(g464,g466)
    c: Block(g466)
    c: Coincident(g467,g458)
    c: Vertical(g467)
    c: PointOnObject(g467,g195)
    c: Coincident(g468,g467)
    c: Perpendicular(g195,g468)
FEATURE [Sketcher::SketchObject] Sketch004  label="rightSideBottom"
  FullyConstrained = false
  sketch-geometry (91):
    g0: ArcOfCircle CenterX=391.073 CenterY=-83.7794 CenterZ=0 NormalX=0 NormalY=0 NormalZ=1 AngleXU=0 Radius=8 StartAngle=3.14159 EndAngle=6.28319
    g1: Circle CenterX=306.073 CenterY=-81.8102 CenterZ=0 NormalX=0 NormalY=0 NormalZ=1 AngleXU=0 Radius=1
    g2: Circle CenterX=306.073 CenterY=-77.8102 CenterZ=0 NormalX=0 NormalY=0 NormalZ=1 AngleXU=0 Radius=1
    g3: Circle CenterX=302.567 CenterY=-42.9683 CenterZ=0 NormalX=0 NormalY=0 NormalZ=1 AngleXU=0 Radius=1
    g4: Circle CenterX=306.073 CenterY=-44.8935 CenterZ=0 NormalX=0 NormalY=0 NormalZ=1 AngleXU=0 Radius=1
    g5: Circle CenterX=306.073 CenterY=-40.8935 CenterZ=0 NormalX=0 NormalY=0 NormalZ=1 AngleXU=0 Radius=1
    g6: BSplineCurve PolesCount=3 KnotsCount=2 Degree=2 IsPeriodic=0
    g7: GeomPoint X=302.567 Y=-42.9683 Z=0
    g8: GeomPoint X=306.073 Y=-40.8935 Z=0
    g9: Circle CenterX=371.567 CenterY=-80.8644 CenterZ=0 NormalX=0 NormalY=0 NormalZ=1 AngleXU=0 Radius=1
    g10: Circle CenterX=375.073 CenterY=-82.7896 CenterZ=0 NormalX=0 NormalY=0 NormalZ=1 AngleXU=0 Radius=1
    g11: Circle CenterX=375.073 CenterY=-78.7896 CenterZ=0 NormalX=0 NormalY=0 NormalZ=1 AngleXU=0 Radius=1
    g12: GeomPoint X=371.567 Y=-80.8644 Z=0
    g13: GeomPoint X=375.073 Y=-78.7896 Z=0
    g14: Circle CenterX=318.073 CenterY=-51.4823 CenterZ=0 NormalX=0 NormalY=0 NormalZ=1 AngleXU=0 Radius=1
    g15: Circle CenterX=318.073 CenterY=-47.4805 CenterZ=0 NormalX=0 NormalY=0 NormalZ=1 AngleXU=0 Radius=1
    g16: GeomPoint X=321.579 Y=-53.4075 Z=0
    g17: GeomPoint X=318.073 Y=-47.4805 Z=0
    g18: Circle CenterX=321.579 CenterY=-67.3492 CenterZ=0 NormalX=0 NormalY=0 NormalZ=1 AngleXU=0 Radius=1
    g19: Circle CenterX=318.073 CenterY=-65.424 CenterZ=0 NormalX=0 NormalY=0 NormalZ=1 AngleXU=0 Radius=1
    g20: Circle CenterX=318.073 CenterY=-69.424 CenterZ=0 NormalX=0 NormalY=0 NormalZ=1 AngleXU=0 Radius=1
    g21: GeomPoint X=321.579 Y=-67.3492 Z=0
    g22: GeomPoint X=318.073 Y=-69.424 Z=0
    g23: Circle CenterX=362.567 CenterY=-89.8542 CenterZ=0 NormalX=0 NormalY=0 NormalZ=1 AngleXU=0 Radius=1
    g24: Circle CenterX=366.073 CenterY=-91.7794 CenterZ=0 NormalX=0 NormalY=0 NormalZ=1 AngleXU=0 Radius=1
    g25: Circle CenterX=362.073 CenterY=-91.7794 CenterZ=0 NormalX=0 NormalY=0 NormalZ=1 AngleXU=0 Radius=1
    g26: GeomPoint X=362.567 Y=-89.8542 Z=0
    g27: GeomPoint X=362.073 Y=-91.7794 Z=0
    g28: Circle CenterX=322.073 CenterY=-91.7794 CenterZ=0 NormalX=0 NormalY=0 NormalZ=1 AngleXU=0 Radius=1
    g29: Circle CenterX=318.073 CenterY=-91.7794 CenterZ=0 NormalX=0 NormalY=0 NormalZ=1 AngleXU=0 Radius=1
    g30: Circle CenterX=318.073 CenterY=-87.7794 CenterZ=0 NormalX=0 NormalY=0 NormalZ=1 AngleXU=0 Radius=1
    g31: GeomPoint X=322.073 Y=-91.7794 Z=0
    g32: GeomPoint X=318.073 Y=-87.7794 Z=0
    g33: ArcOfCircle CenterX=391.073 CenterY=22.1087 CenterZ=0 NormalX=0 NormalY=0 NormalZ=1 AngleXU=0 Radius=4 StartAngle=0 EndAngle=3.14159
    g34: LineSegment StartX=387.073 StartY=22.1087 StartZ=0 EndX=383.073 EndY=-83.7794 EndZ=0
    g35: LineSegment StartX=395.073 StartY=22.1087 StartZ=0 EndX=399.073 EndY=-83.7794 EndZ=0
    g36: LineSegment StartX=232.072 StartY=-103.779 StartZ=0 EndX=232.072 EndY=-100.779 EndZ=0
    g37: GeomPoint X=232.072 Y=-94.7794 Z=0
    g38: GeomPoint X=223.072 Y=-97.7794 Z=0
    g39: Circle CenterX=232.072 CenterY=-94.7794 CenterZ=0 NormalX=0 NormalY=0 NormalZ=1 AngleXU=0 Radius=1
    g40: Circle CenterX=232.072 CenterY=-100.779 CenterZ=0 NormalX=0 NormalY=0 NormalZ=1 AngleXU=0 Radius=1
    g41: BSplineCurve PolesCount=5 KnotsCount=3 Degree=3 IsPeriodic=0
    g42: GeomPoint X=232.072 Y=-100.779 Z=0
    g43: LineSegment StartX=232.072 StartY=-94.7794 StartZ=0 EndX=232.072 EndY=-91.7794 EndZ=0
    g44: LineSegment StartX=245.072 StartY=-31.3037 StartZ=0 EndX=243.535 EndY=-33.1602 EndZ=0
    g45: LineSegment StartX=241.775 StartY=-35.2862 StartZ=0 EndX=240.266 EndY=-37.1092 EndZ=0
    g46: LineSegment StartX=243.535 StartY=-33.1602 StartZ=0 EndX=248.619 EndY=-37.3688 EndZ=0
    g47: LineSegment StartX=241.775 StartY=-35.2862 StartZ=0 EndX=246.859 EndY=-39.4949 EndZ=0
    g48: LineSegment StartX=248.619 StartY=-37.3688 StartZ=0 EndX=246.859 EndY=-39.4949 EndZ=0
    g49: LineSegment StartX=232.072 StartY=-103.779 StartZ=0 EndX=407.073 EndY=-103.779 EndZ=0
    g50: LineSegment StartX=299.888 StartY=-86.6413 StartZ=0 EndX=240.266 EndY=-37.1092 EndZ=0
    g51: LineSegment StartX=245.072 StartY=-11.4025 StartZ=0 EndX=302.567 EndY=-42.9683 EndZ=0
    g52: BSplineCurve PolesCount=3 KnotsCount=2 Degree=2 IsPeriodic=0
    g53: BSplineCurve PolesCount=3 KnotsCount=2 Degree=2 IsPeriodic=0
    g54: LineSegment StartX=321.579 StartY=-53.4075 StartZ=0 EndX=371.567 EndY=-80.8644 EndZ=0
    g55: BSplineCurve PolesCount=3 KnotsCount=2 Degree=2 IsPeriodic=0
    g56: BSplineCurve PolesCount=3 KnotsCount=2 Degree=2 IsPeriodic=0
    g57: BSplineCurve PolesCount=3 KnotsCount=2 Degree=2 IsPeriodic=0
    g58: LineSegment StartX=318.073 StartY=-69.424 StartZ=0 EndX=318.073 EndY=-87.7794 EndZ=0
    g59: LineSegment StartX=321.579 StartY=-67.3492 StartZ=0 EndX=362.567 EndY=-89.8542 EndZ=0
    g60: LineSegment StartX=362.073 StartY=-91.7794 StartZ=0 EndX=322.073 EndY=-91.7794 EndZ=0
    g61: BSplineCurve PolesCount=3 KnotsCount=2 Degree=2 IsPeriodic=0
    g62: BSplineCurve PolesCount=3 KnotsCount=2 Degree=2 IsPeriodic=0
    g63: LineSegment StartX=245.072 StartY=-31.3037 StartZ=0 EndX=302.996 EndY=-79.2541 EndZ=0
    g64: LineSegment StartX=302.567 StartY=-56.9099 StartZ=0 EndX=239.193 EndY=-22.1109 EndZ=0
    g65: LineSegment StartX=306.073 StartY=-62.8351 StartZ=0 EndX=306.073 EndY=-77.8102 EndZ=0
    g66: BSplineCurve PolesCount=3 KnotsCount=2 Degree=2 IsPeriodic=0
    g67: LineSegment StartX=298.776 StartY=-91.7794 StartZ=0 EndX=232.072 EndY=-91.7794 EndZ=0
    g68: LineSegment StartX=245.072 StartY=-11.4025 StartZ=0 EndX=243.628 EndY=-14.0323 EndZ=0
    g69: LineSegment StartX=240.741 StartY=-19.2917 StartZ=0 EndX=239.193 EndY=-22.1109 EndZ=0
    g70: LineSegment StartX=243.628 StartY=-14.0323 StartZ=0 EndX=246.258 EndY=-15.476 EndZ=0
    g71: LineSegment StartX=240.741 StartY=-19.2917 StartZ=0 EndX=243.37 EndY=-20.7355 EndZ=0
    g72: ArcOfCircle CenterX=247.444 CenterY=-19.5495 CenterZ=0 NormalX=0 NormalY=0 NormalZ=1 AngleXU=0 Radius=4.24264 StartAngle=3.4249 EndAngle=8.13729
    g73: LineSegment StartX=407.073 StartY=-103.779 StartZ=0 EndX=407.073 EndY=48.2206 EndZ=0
    g74: LineSegment StartX=375.073 StartY=48.2206 StartZ=0 EndX=375.073 EndY=-78.7896 EndZ=0
    g75: LineSegment StartX=375.073 StartY=48.2206 StartZ=0 EndX=382.073 EndY=48.2206 EndZ=0
    g76: LineSegment StartX=407.073 StartY=48.2206 StartZ=0 EndX=400.073 EndY=48.2206 EndZ=0
    g77: LineSegment StartX=394.073 StartY=48.2206 StartZ=0 EndX=394.073 EndY=52.2206 EndZ=0
    g78: LineSegment StartX=388.073 StartY=48.2206 StartZ=0 EndX=388.073 EndY=58.2206 EndZ=0
    g79: ArcOfCircle CenterX=385.073 CenterY=61.2206 CenterZ=0 NormalX=0 NormalY=0 NormalZ=1 AngleXU=0 Radius=4.24264 StartAngle=5.49779 EndAngle=10.2102
    g80: ArcOfCircle CenterX=397.073 CenterY=55.2206 CenterZ=0 NormalX=0 NormalY=0 NormalZ=1 AngleXU=0 Radius=4.24264 StartAngle=5.49779 EndAngle=10.2102
    g81: LineSegment StartX=382.073 StartY=58.2206 StartZ=0 EndX=382.073 EndY=48.2206 EndZ=0
    g82: LineSegment StartX=400.073 StartY=52.2206 StartZ=0 EndX=400.073 EndY=48.2206 EndZ=0
    g83: LineSegment StartX=394.073 StartY=48.2206 StartZ=0 EndX=388.073 EndY=48.2206 EndZ=0
    g84: LineSegment StartX=306.073 StartY=-40.8935 StartZ=0 EndX=306.073 EndY=-27.5935 EndZ=0
    g85: LineSegment StartX=318.073 StartY=-27.5935 StartZ=0 EndX=318.073 EndY=-47.4805 EndZ=0
    g86: LineSegment StartX=306.073 StartY=-27.5935 StartZ=0 EndX=310.073 EndY=-27.5935 EndZ=0
    g87: LineSegment StartX=318.073 StartY=-27.5935 StartZ=0 EndX=314.073 EndY=-27.5935 EndZ=0
    g88: LineSegment StartX=310.073 StartY=-27.5935 StartZ=0 EndX=310.073 EndY=-31.5935 EndZ=0
    g89: LineSegment StartX=314.073 StartY=-27.5935 StartZ=0 EndX=314.073 EndY=-31.5935 EndZ=0
    g90: ArcOfCircle CenterX=312.073 CenterY=-33.5935 CenterZ=0 NormalX=0 NormalY=0 NormalZ=1 AngleXU=0 Radius=2.82843 StartAngle=2.35619 EndAngle=7.06858
  constraints (121):
    c: Distance(g44) = 2.41
    c: Block(g44)
    c: Coincident(g46,g44)
    c: Coincident(g49,g36)
    c: Horizontal(g49)
    c: Block(g49)
    c: Coincident(g50,g45)
    c: Block(g50)
    c: Coincident(g51,g6)
    c: Block(g51)
    c: Coincident(g54,g52)
    c: Coincident(g54,g53)
    c: Coincident(g58,g56)
    c: Coincident(g58,g57)
    c: Vertical(g58)
    c: Coincident(g59,g56)
    c: Coincident(g59,g55)
    c: Coincident(g60,g55)
    c: Coincident(g60,g57)
    c: Horizontal(g60)
    c: Block(g61)
    c: Block(g62)
    c: Coincident(g63,g44)
    c: Coincident(g63,g62)
    c: Coincident(g64,g61)
    c: Coincident(g65,g61)
    c: Coincident(g65,g62)
    c: Vertical(g65)
    c: Block(g66)
    c: Coincident(g66,g50)
    c: Coincident(g67,g66)
    c: Coincident(g67,g43)
    c: Horizontal(g67)
    c: Coincident(g68,g51)
    c: Perpendicular(g68,g51)
    c: Coincident(g69,g64)
    c: Coincident(g70,g68)
    c: Distance(g70) = 3
    c: Distance(g71) = 3
    c: Perpendicular(g68,g70)
    c: Coincident(g72,g70)
    c: Coincident(g72,g71)
    c: Block(g72)
    c: Block(g69)
    c: Block(g71)
    c: Block(g54)
    c: Block(g59)
    c: Block(g58)
    c: Block(g60)
    c: Block(g67)
    c: Block(g43)
    c: Block(g36)
    c: Block(g48)
    c: Block(g46)
    c: Block(g47)
    c: Block(g45)
    c: Block(g35)
    c: Block(g34)
    c: Block(g0)
    c: Block(g33)
    c: Block(g52)
    c: Block(g6)
    c: Block(g41)
    c: Block(g57)
    c: Block(g55)
    c: Block(g53)
    c: Block(g68)
    c: Distance(g48) = 2.76
    c: Distance(g47) = 6.6
    c: Distance(g45) = 2.36657
    c: Coincident(g73,g49)
    c: Vertical(g73)
    c: Distance(g73) = 152
    c: Coincident(g74,g53)
    c: Vertical(g74)
    c: Block(g74)
    c: Coincident(g75,g74)
    c: Horizontal(g75)
    c: Distance(g75) = 7
    c: Horizontal(g76)
    c: Distance(g76) = 7
    c: Coincident(g76,g73)
    c: Vertical(g77)
    c: Distance(g77) = 4
    c: Vertical(g78)
    c: Distance(g78) = 10
    c: Coincident(g79,g78)
    c: Coincident(g80,g77)
    c: Block(g80)
    c: Block(g79)
    c: Coincident(g81,g79)
    c: Coincident(g81,g75)
    c: Vertical(g81)
    c: Coincident(g82,g80)
    c: Coincident(g82,g76)
    c: Vertical(g82)
    c: Coincident(g83,g77)
    c: Coincident(g83,g78)
    c: Horizontal(g83)
    c: Coincident(g84,g6)
    c: Vertical(g84)
    c: Distance(g84) = 13.3
    c: Coincident(g85,g52)
    c: Vertical(g85)
    c: Block(g85)
    c: Coincident(g86,g84)
    c: Horizontal(g86)
    c: Distance(g86) = 4
    c: Coincident(g87,g85)
    c: Horizontal(g87)
    c: Distance(g87) = 4
    c: Coincident(g88,g86)
    c: Vertical(g88)
    c: Coincident(g89,g87)
    c: Vertical(g89)
    c: Distance(g88) = 4
    c: Distance(g89) = 4
    c: Coincident(g90,g88)
    c: Coincident(g90,g89)
    c: Block(g90)
    c: Block(g56)
FEATURE [Sketcher::SketchObject] Sketch005  label="middleTop"
  FullyConstrained = true
  sketch-geometry (133):
    g0: Circle CenterX=175.025 CenterY=27.0667 CenterZ=0 NormalX=0 NormalY=0 NormalZ=1 AngleXU=0 Radius=1
    g1: Circle CenterX=179.022 CenterY=24.8665 CenterZ=0 NormalX=0 NormalY=0 NormalZ=1 AngleXU=0 Radius=1
    g2: Circle CenterX=179.022 CenterY=27.0606 CenterZ=0 NormalX=0 NormalY=0 NormalZ=1 AngleXU=0 Radius=1
    g3: BSplineCurve PolesCount=3 KnotsCount=2 Degree=2 IsPeriodic=0
    g4: GeomPoint X=175.025 Y=27.0667 Z=0
    g5: GeomPoint X=179.022 Y=27.0606 Z=0
    g6: Circle CenterX=189.124 CenterY=27.0628 CenterZ=0 NormalX=0 NormalY=0 NormalZ=1 AngleXU=0 Radius=1
    g7: Circle CenterX=185.124 CenterY=24.8665 CenterZ=0 NormalX=0 NormalY=0 NormalZ=1 AngleXU=0 Radius=1
    g8: Circle CenterX=185.124 CenterY=27.0606 CenterZ=0 NormalX=0 NormalY=0 NormalZ=1 AngleXU=0 Radius=1
    g9: BSplineCurve PolesCount=3 KnotsCount=2 Degree=2 IsPeriodic=0
    g10: GeomPoint X=189.124 Y=27.0628 Z=0
    g11: GeomPoint X=185.124 Y=27.0606 Z=0
    g12: Circle CenterX=165.871 CenterY=18.1458 CenterZ=0 NormalX=0 NormalY=0 NormalZ=1 AngleXU=0 Radius=1
    g13: Circle CenterX=169.377 CenterY=16.2206 CenterZ=0 NormalX=0 NormalY=0 NormalZ=1 AngleXU=0 Radius=1
    g14: Circle CenterX=165.871 CenterY=14.2956 CenterZ=0 NormalX=0 NormalY=0 NormalZ=1 AngleXU=0 Radius=1
    g15: BSplineCurve PolesCount=3 KnotsCount=2 Degree=2 IsPeriodic=0
    g16: GeomPoint X=165.871 Y=18.1458 Z=0
    g17: GeomPoint X=165.871 Y=14.2956 Z=0
    g18: Circle CenterX=198.275 CenterY=18.1318 CenterZ=0 NormalX=0 NormalY=0 NormalZ=1 AngleXU=0 Radius=1
    g19: Circle CenterX=194.768 CenterY=16.2206 CenterZ=0 NormalX=0 NormalY=0 NormalZ=1 AngleXU=0 Radius=1
    g20: Circle CenterX=198.264 CenterY=14.2963 CenterZ=0 NormalX=0 NormalY=0 NormalZ=1 AngleXU=0 Radius=1
    g21: BSplineCurve PolesCount=3 KnotsCount=2 Degree=2 IsPeriodic=0
    g22: GeomPoint X=198.275 Y=18.1318 Z=0
    g23: GeomPoint X=198.264 Y=14.2963 Z=0
    g24: Circle CenterX=125.607 CenterY=54.1951 CenterZ=0 NormalX=0 NormalY=0 NormalZ=1 AngleXU=0 Radius=1
    g25: Circle CenterX=139.632 CenterY=46.4944 CenterZ=0 NormalX=0 NormalY=0 NormalZ=1 AngleXU=0 Radius=1
    g26: Circle CenterX=127.326 CenterY=56.7187 CenterZ=0 NormalX=0 NormalY=0 NormalZ=1 AngleXU=0 Radius=1
    g27: BSplineCurve PolesCount=3 KnotsCount=2 Degree=2 IsPeriodic=0
    g28: GeomPoint X=125.607 Y=54.1951 Z=0
    g29: GeomPoint X=127.326 Y=56.7187 Z=0
    g30: Circle CenterX=236.824 CenterY=56.7187 CenterZ=0 NormalX=0 NormalY=0 NormalZ=1 AngleXU=0 Radius=1
    g31: Circle CenterX=224.513 CenterY=46.4944 CenterZ=0 NormalX=0 NormalY=0 NormalZ=1 AngleXU=0 Radius=1
    g32: Circle CenterX=238.538 CenterY=54.1951 CenterZ=0 NormalX=0 NormalY=0 NormalZ=1 AngleXU=0 Radius=1
    g33: BSplineCurve PolesCount=3 KnotsCount=2 Degree=2 IsPeriodic=0
    g34: GeomPoint X=236.824 Y=56.7187 Z=0
    g35: GeomPoint X=238.538 Y=54.1951 Z=0
    g36: Circle CenterX=189.121 CenterY=124.221 CenterZ=0 NormalX=0 NormalY=0 NormalZ=1 AngleXU=0 Radius=1
    g37: Circle CenterX=185.124 CenterY=124.221 CenterZ=0 NormalX=0 NormalY=0 NormalZ=1 AngleXU=0 Radius=1
    g38: Circle CenterX=185.124 CenterY=120.221 CenterZ=0 NormalX=0 NormalY=0 NormalZ=1 AngleXU=0 Radius=1
    g39: BSplineCurve PolesCount=3 KnotsCount=2 Degree=2 IsPeriodic=0
    g40: GeomPoint X=189.121 Y=124.221 Z=0
    g41: GeomPoint X=185.124 Y=120.221 Z=0
    g42: Circle CenterX=175.022 CenterY=124.221 CenterZ=0 NormalX=0 NormalY=0 NormalZ=1 AngleXU=0 Radius=1
    g43: Circle CenterX=179.022 CenterY=124.221 CenterZ=0 NormalX=0 NormalY=0 NormalZ=1 AngleXU=0 Radius=1
    g44: Circle CenterX=179.022 CenterY=120.221 CenterZ=0 NormalX=0 NormalY=0 NormalZ=1 AngleXU=0 Radius=1
    g45: BSplineCurve PolesCount=3 KnotsCount=2 Degree=2 IsPeriodic=0
    g46: GeomPoint X=175.022 Y=124.221 Z=0
    g47: GeomPoint X=179.022 Y=120.221 Z=0
    g48: LineSegment StartX=232.071 StartY=124.221 StartZ=0 EndX=232.071 EndY=127.221 EndZ=0
    g49-g52: Circle x4 (B-spline internal-alignment scaffolding for g53; pole/knot coordinates omitted)
    g53: BSplineCurve PolesCount=5 KnotsCount=3 Degree=3 IsPeriodic=0
    g54: GeomPoint X=232.072 Y=133.221 Z=0
    g55: GeomPoint X=223.072 Y=130.221 Z=0
    g56: GeomPoint X=232.071 Y=127.221 Z=0
    g57-g61: Circle x5 (B-spline internal-alignment scaffolding for g62; pole/knot coordinates omitted)
    g62: BSplineCurve PolesCount=5 KnotsCount=3 Degree=3 IsPeriodic=0
    g63: GeomPoint X=132.072 Y=133.221 Z=0
    g64: GeomPoint X=141.072 Y=130.221 Z=0
    g65: GeomPoint X=132.072 Y=127.221 Z=0
    g66: ArcOfCircle CenterX=247.391 CenterY=52.0843 CenterZ=0 NormalX=0 NormalY=0 NormalZ=1 AngleXU=0 Radius=4.24264 StartAngle=4.42912 EndAngle=9.14151
    g67: LineSegment StartX=240.687 StartY=51.8263 StartZ=0 EndX=239.192 EndY=54.5542 EndZ=0
    g68: LineSegment StartX=243.575 StartY=46.5669 StartZ=0 EndX=245.072 EndY=43.8408 EndZ=0
    g69: LineSegment StartX=240.168 StartY=69.471 StartZ=0 EndX=241.708 EndY=67.6172 EndZ=0
    g70: LineSegment StartX=246.783 StartY=71.8328 StartZ=0 EndX=248.546 EndY=69.7098 EndZ=0
    g71: LineSegment StartX=245.073 StartY=63.5726 StartZ=0 EndX=243.476 EndY=65.4955 EndZ=0
    g72: LineSegment StartX=123.967 StartY=69.4706 StartZ=0 EndX=122.37 EndY=67.5474 EndZ=0
    g73: LineSegment StartX=232.072 StartY=133.221 StartZ=0 EndX=232.072 EndY=136.221 EndZ=0
    g74: LineSegment StartX=232.072 StartY=136.221 StartZ=0 EndX=132.072 EndY=136.221 EndZ=0
    g75: LineSegment StartX=132.072 StartY=136.221 StartZ=0 EndX=132.072 EndY=133.221 EndZ=0
    g76: LineSegment StartX=132.072 StartY=127.221 StartZ=0 EndX=132.072 EndY=124.221 EndZ=0
    g77: LineSegment StartX=132.072 StartY=124.221 StartZ=0 EndX=175.022 EndY=124.221 EndZ=0
    g78: LineSegment StartX=189.121 StartY=124.221 StartZ=0 EndX=232.071 EndY=124.221 EndZ=0
    g79: LineSegment StartX=185.124 StartY=120.221 StartZ=0 EndX=185.124 EndY=27.0606 EndZ=0
    g80: LineSegment StartX=189.124 StartY=27.0628 StartZ=0 EndX=240.168 EndY=69.471 EndZ=0
    g81: LineSegment StartX=241.708 StartY=67.6172 StartZ=0 EndX=246.783 EndY=71.8328 EndZ=0
    g82: LineSegment StartX=248.546 StartY=69.7098 StartZ=0 EndX=243.476 EndY=65.4955 EndZ=0
    g83: LineSegment StartX=245.073 StartY=63.5726 StartZ=0 EndX=236.824 EndY=56.7187 EndZ=0
    g84: LineSegment StartX=238.538 StartY=54.1951 StartZ=0 EndX=239.192 EndY=54.5542 EndZ=0
    g85: LineSegment StartX=240.687 StartY=51.8263 StartZ=0 EndX=243.317 EndY=53.2701 EndZ=0
    g86: LineSegment StartX=246.205 StartY=48.0108 StartZ=0 EndX=243.575 EndY=46.5669 EndZ=0
    g87: LineSegment StartX=245.072 StartY=43.8408 StartZ=0 EndX=198.275 EndY=18.1318 EndZ=0
    g88: LineSegment StartX=165.871 StartY=18.1458 StartZ=0 EndX=118.934 EndY=43.9178 EndZ=0
    g89: LineSegment StartX=118.934 StartY=43.9178 StartZ=0 EndX=120.377 EndY=46.5474 EndZ=0
    g90: LineSegment StartX=117.748 StartY=47.9913 StartZ=0 EndX=120.377 EndY=46.5474 EndZ=0
    g91: LineSegment StartX=120.635 StartY=53.2507 StartZ=0 EndX=123.265 EndY=51.8068 EndZ=0
    g92: LineSegment StartX=123.265 StartY=51.8068 StartZ=0 EndX=124.73 EndY=54.6766 EndZ=0
    g93: ArcOfCircle CenterX=116.562 CenterY=52.0649 CenterZ=0 NormalX=0 NormalY=0 NormalZ=1 AngleXU=0 Radius=4.24264 StartAngle=0.283267 EndAngle=4.99566
    g94: LineSegment StartX=124.73 StartY=54.6766 StartZ=0 EndX=125.607 EndY=54.1951 EndZ=0
    g95: LineSegment StartX=127.326 StartY=56.7187 StartZ=0 EndX=119.072 EndY=63.5741 EndZ=0
    g96: LineSegment StartX=119.072 StartY=63.5741 StartZ=0 EndX=120.669 EndY=65.4973 EndZ=0
    g97: LineSegment StartX=120.669 StartY=65.4973 StartZ=0 EndX=115.591 EndY=69.7147 EndZ=0
    g98: LineSegment StartX=115.591 StartY=69.7147 StartZ=0 EndX=117.293 EndY=71.7641 EndZ=0
    g99: LineSegment StartX=117.293 StartY=71.7641 StartZ=0 EndX=122.37 EndY=67.5474 EndZ=0
    g100: LineSegment StartX=123.967 StartY=69.4706 StartZ=0 EndX=175.025 EndY=27.0667 EndZ=0
    g101: LineSegment StartX=179.022 StartY=27.0606 StartZ=0 EndX=179.022 EndY=120.221 EndZ=0
    g102-g117: Circle x16 (B-spline internal-alignment scaffolding for g118; pole/knot coordinates omitted)
    g118: BSplineCurve PolesCount=16 KnotsCount=14 Degree=3 IsPeriodic=0
    g119-g132: GeomPoint x14 (B-spline internal-alignment scaffolding for g118; pole/knot coordinates omitted)
  constraints (180):
    c: Weight(g0) = 1
    c: Equal(g0,g1)
    c: Equal(g0,g2)
    c: InternalAlignment(g0,g3)
    c: InternalAlignment(g1,g3)
    c: InternalAlignment(g2,g3)
    c: InternalAlignment(g4,g3)
    c: InternalAlignment(g5,g3)
    c: Weight(g6) = 1
    c: Equal(g6,g7)
    c: Equal(g6,g8)
    c: InternalAlignment(g6,g9)
    c: InternalAlignment(g7,g9)
    c: InternalAlignment(g8,g9)
    c: InternalAlignment(g10,g9)
    c: InternalAlignment(g11,g9)
    c: Block(g9)
    c: Block(g3)
    c: Weight(g12) = 1
    c: Equal(g12,g13)
    c: Equal(g12,g14)
    c: InternalAlignment(g12,g15)
    c: InternalAlignment(g13,g15)
    c: InternalAlignment(g14,g15)
    c: InternalAlignment(g16,g15)
    c: InternalAlignment(g17,g15)
    c: Weight(g18) = 1
    c: Equal(g18,g19)
    c: Equal(g18,g20)
    c: InternalAlignment(g18,g21)
    c: InternalAlignment(g19,g21)
    c: InternalAlignment(g20,g21)
    c: InternalAlignment(g22,g21)
    c: InternalAlignment(g23,g21)
    c: Block(g15)
    c: Block(g21)
    c: Weight(g24) = 1
    c: Equal(g24,g25)
    c: Equal(g24,g26)
    c: InternalAlignment(g24,g27)
    c: InternalAlignment(g25,g27)
    c: InternalAlignment(g26,g27)
    c: InternalAlignment(g28,g27)
    c: InternalAlignment(g29,g27)
    c: Block(g27)
    c: Weight(g30) = 1
    c: Equal(g30,g31)
    c: Equal(g30,g32)
    c: InternalAlignment(g30,g33)
    c: InternalAlignment(g31,g33)
    c: InternalAlignment(g32,g33)
    c: InternalAlignment(g34,g33)
    c: InternalAlignment(g35,g33)
    c: Block(g33)
    c: Weight(g36) = 1
    c: Equal(g36,g37)
    c: Equal(g36,g38)
    c: InternalAlignment(g36,g39)
    c: InternalAlignment(g37,g39)
    c: InternalAlignment(g38,g39)
    c: InternalAlignment(g40,g39)
    c: InternalAlignment(g41,g39)
    c: Weight(g42) = 1
    c: Equal(g42,g43)
    c: Equal(g42,g44)
    c: InternalAlignment(g42,g45)
    c: InternalAlignment(g43,g45)
    c: InternalAlignment(g44,g45)
    c: InternalAlignment(g46,g45)
    c: InternalAlignment(g47,g45)
    c: Block(g45)
    c: Block(g39)
    c: Vertical(g48)
    c: Distance(g48) = 3
    c: Weight(g49) = 1
    c: Equal(g49,g50)
    c: Equal(g49,g51)
    c: Equal(g49,g52)
    c: Coincident(g53,g48)
    c: InternalAlignment(g49-g52 -> g53) x4
    c: InternalAlignment(g54,g53)
    c: InternalAlignment(g55,g53)
    c: InternalAlignment(g56,g53)
    c: Weight(g57) = 1
    c: Equal(g57, g58-g61) x4
    c: InternalAlignment(g57-g61 -> g62) x5
    c: InternalAlignment(g63,g62)
    c: InternalAlignment(g64,g62)
    c: InternalAlignment(g65,g62)
    c: Block(g62)
    c: Block(g67)
    c: Block(g68)
    c: Distance(g69) = 2.41
    c: Distance(g70) = 2.76
    c: Distance(g71) = 2.5
    c: Distance(g72) = 2.5
    c: Block(g66)
    c: Block(g48)
    c: Block(g53)
    c: Coincident(g73,g53)
    c: Vertical(g73)
    c: Distance(g73) = 3
    c: Coincident(g74,g73)
    c: Horizontal(g74)
    c: Distance(g74) = 100
    c: Coincident(g75,g74)
    c: Coincident(g75,g62)
    c: Vertical(g75)
    c: Distance(g75) = 3
    c: Coincident(g76,g62)
    c: Vertical(g76)
    c: Distance(g76) = 3
    c: Coincident(g77,g76)
    c: Coincident(g77,g45)
    c: Horizontal(g77)
    c: Distance(g77) = 42.95
    c: Coincident(g78,g39)
    c: Coincident(g78,g48)
    c: Horizontal(g78)
    c: Distance(g78) = 42.95
    c: Coincident(g79,g39)
    c: Coincident(g79,g9)
    c: Vertical(g79)
    c: Distance(g79) = 93.16
    c: Coincident(g80,g9)
    c: Coincident(g80,g69)
    c: Angle(g80) = 0.693245
    c: Block(g80)
    c: Coincident(g81,g69)
    c: Coincident(g81,g70)
    c: Block(g81)
    c: Coincident(g82,g70)
    c: Coincident(g82,g71)
    c: Block(g82)
    c: Coincident(g83,g71)
    c: Coincident(g83,g33)
    c: Block(g71)
    c: Coincident(g84,g33)
    c: Coincident(g84,g67)
    c: Coincident(g85,g67)
    c: Coincident(g85,g66)
    c: Coincident(g86,g66)
    c: Coincident(g86,g68)
    c: Coincident(g87,g68)
    c: Coincident(g87,g21)
    c: Coincident(g88,g15)
    c: Coincident(g89,g88)
    c: Block(g89)
    c: Coincident(g90,g89)
    c: Block(g90)
    c: Block(g91)
    c: Coincident(g92,g91)
    c: Block(g92)
    c: Coincident(g93,g91)
    c: Coincident(g93,g90)
    c: Block(g93)
    c: Coincident(g94,g92)
    c: Coincident(g94,g27)
    c: Coincident(g95,g27)
    c: Block(g95)
    c: Coincident(g96,g95)
    c: Coincident(g97,g96)
    c: Coincident(g98,g97)
    c: Coincident(g99,g98)
    c: Coincident(g99,g72)
    c: Block(g98)
    c: Block(g96)
    c: Block(g72)
    c: Coincident(g100,g72)
    c: Coincident(g100,g3)
    c: Coincident(g101,g3)
    c: Coincident(g101,g45)
    c: Vertical(g101)
    c: Coincident(g118,g21)
    c: Weight(g102) = 1
    c: Equal(g102, g103-g117) x15
    c: Coincident(g118,g15)
    c: InternalAlignment(g102-g117 -> g118) x16
    c: InternalAlignment(g119-g132 -> g118) x14
    c: Block(g118)
FEATURE [Sketcher::SketchObject] Sketch006  label="leftSideTop"
  FullyConstrained = true
  sketch-geometry (99):
    g0: Circle CenterX=61.1495 CenterY=111.695 CenterZ=0 NormalX=0 NormalY=0 NormalZ=1 AngleXU=0 Radius=1
    g1: Circle CenterX=58.0728 CenterY=114.251 CenterZ=0 NormalX=0 NormalY=0 NormalZ=1 AngleXU=0 Radius=1
    g2: Circle CenterX=58.0728 CenterY=110.251 CenterZ=0 NormalX=0 NormalY=0 NormalZ=1 AngleXU=0 Radius=1
    g3: BSplineCurve PolesCount=3 KnotsCount=2 Degree=2 IsPeriodic=0
    g4: GeomPoint X=61.1495 Y=111.695 Z=0
    g5: GeomPoint X=58.0728 Y=110.251 Z=0
    g6: Circle CenterX=61.5791 CenterY=89.3511 CenterZ=0 NormalX=0 NormalY=0 NormalZ=1 AngleXU=0 Radius=1
    g7: Circle CenterX=58.0728 CenterY=91.2763 CenterZ=0 NormalX=0 NormalY=0 NormalZ=1 AngleXU=0 Radius=1
    g8: Circle CenterX=58.0728 CenterY=95.2763 CenterZ=0 NormalX=0 NormalY=0 NormalZ=1 AngleXU=0 Radius=1
    g9: BSplineCurve PolesCount=3 KnotsCount=2 Degree=2 IsPeriodic=0
    g10: GeomPoint X=61.5791 Y=89.3511 Z=0
    g11: GeomPoint X=58.0728 Y=95.2763 Z=0
    g12: Circle CenterX=62.0728 CenterY=124.221 CenterZ=0 NormalX=0 NormalY=0 NormalZ=1 AngleXU=0 Radius=1
    g13: Circle CenterX=58.0728 CenterY=124.221 CenterZ=0 NormalX=0 NormalY=0 NormalZ=1 AngleXU=0 Radius=1
    g14: Circle CenterX=61.1496 CenterY=121.665 CenterZ=0 NormalX=0 NormalY=0 NormalZ=1 AngleXU=0 Radius=1
    g15: BSplineCurve PolesCount=3 KnotsCount=2 Degree=2 IsPeriodic=0
    g16: GeomPoint X=62.0728 Y=124.221 Z=0
    g17: GeomPoint X=61.1496 Y=121.665 Z=0
    g18: Circle CenterX=61.5791 CenterY=75.4095 CenterZ=0 NormalX=0 NormalY=0 NormalZ=1 AngleXU=0 Radius=1
    g19: Circle CenterX=58.0728 CenterY=77.3346 CenterZ=0 NormalX=0 NormalY=0 NormalZ=1 AngleXU=0 Radius=1
    g20: Circle CenterX=58.0728 CenterY=73.3346 CenterZ=0 NormalX=0 NormalY=0 NormalZ=1 AngleXU=0 Radius=1
    g21: BSplineCurve PolesCount=3 KnotsCount=2 Degree=2 IsPeriodic=0
    g22: GeomPoint X=61.5791 Y=75.4095 Z=0
    g23: GeomPoint X=58.0728 Y=73.3346 Z=0
    g24: Circle CenterX=2.07281 CenterY=124.221 CenterZ=0 NormalX=0 NormalY=0 NormalZ=1 AngleXU=0 Radius=1
    g25: Circle CenterX=1.57905 CenterY=122.295 CenterZ=0 NormalX=0 NormalY=0 NormalZ=1 AngleXU=0 Radius=1
    g26: BSplineCurve PolesCount=3 KnotsCount=2 Degree=2 IsPeriodic=0
    g27: GeomPoint X=2.07281 Y=124.221 Z=0
    g28: GeomPoint X=1.57905 Y=122.295 Z=0
    g29: Circle CenterX=46.0728 CenterY=124.221 CenterZ=0 NormalX=0 NormalY=0 NormalZ=1 AngleXU=0 Radius=1
    g30: Circle CenterX=46.0728 CenterY=120.221 CenterZ=0 NormalX=0 NormalY=0 NormalZ=1 AngleXU=0 Radius=1
    g31: BSplineCurve PolesCount=3 KnotsCount=2 Degree=2 IsPeriodic=0
    g32: GeomPoint X=42.0728 Y=124.221 Z=0
    g33: GeomPoint X=46.0728 Y=120.221 Z=0
    g34: Circle CenterX=46.0728 CenterY=109.865 CenterZ=0 NormalX=0 NormalY=0 NormalZ=1 AngleXU=0 Radius=1
    g35: Circle CenterX=46.0728 CenterY=105.865 CenterZ=0 NormalX=0 NormalY=0 NormalZ=1 AngleXU=0 Radius=1
    g36: Circle CenterX=42.0728 CenterY=105.865 CenterZ=0 NormalX=0 NormalY=0 NormalZ=1 AngleXU=0 Radius=1
    g37: BSplineCurve PolesCount=3 KnotsCount=2 Degree=2 IsPeriodic=0
    g38: GeomPoint X=46.0728 Y=109.865 Z=0
    g39: GeomPoint X=42.0728 Y=105.865 Z=0
    g40: Circle CenterX=35.5028 CenterY=105.865 CenterZ=0 NormalX=0 NormalY=0 NormalZ=1 AngleXU=0 Radius=1
    g41: Circle CenterX=31.5028 CenterY=105.865 CenterZ=0 NormalX=0 NormalY=0 NormalZ=1 AngleXU=0 Radius=1
    g42: Circle CenterX=27.9965 CenterY=107.79 CenterZ=0 NormalX=0 NormalY=0 NormalZ=1 AngleXU=0 Radius=1
    g43: BSplineCurve PolesCount=3 KnotsCount=2 Degree=2 IsPeriodic=0
    g44: GeomPoint X=35.5028 Y=105.865 Z=0
    g45: GeomPoint X=27.9965 Y=107.79 Z=0
    g46-g50: Circle x5 (B-spline internal-alignment scaffolding for g51; pole/knot coordinates omitted)
    g51: BSplineCurve PolesCount=5 KnotsCount=3 Degree=3 IsPeriodic=0
    g52: GeomPoint X=132.072 Y=133.221 Z=0
    g53: GeomPoint X=141.072 Y=130.221 Z=0
    g54: GeomPoint X=132.072 Y=127.221 Z=0
    g55: ArcOfCircle CenterX=116.562 CenterY=52.0649 CenterZ=0 NormalX=0 NormalY=0 NormalZ=1 AngleXU=0 Radius=4.24264 StartAngle=0.283268 EndAngle=4.99566
    g56: LineSegment StartX=123.967 StartY=69.4706 StartZ=0 EndX=122.37 EndY=67.5474 EndZ=0
    g57: LineSegment StartX=117.293 StartY=71.7641 StartZ=0 EndX=115.591 EndY=69.7147 EndZ=0
    g58: LineSegment StartX=120.669 StartY=65.4973 StartZ=0 EndX=119.072 EndY=63.5741 EndZ=0
    g59: LineSegment StartX=124.73 StartY=54.6766 StartZ=0 EndX=123.265 EndY=51.8068 EndZ=0
    g60: LineSegment StartX=120.377 StartY=46.5474 StartZ=0 EndX=118.934 EndY=43.9178 EndZ=0
    g61: BSplineCurve PolesCount=3 KnotsCount=2 Degree=2 IsPeriodic=0
    g62: BSplineCurve PolesCount=3 KnotsCount=2 Degree=2 IsPeriodic=0
    g63: LineSegment StartX=61.5791 StartY=75.4095 StartZ=0 EndX=118.934 EndY=43.9178 EndZ=0
    g64: LineSegment StartX=117.748 StartY=47.9913 StartZ=0 EndX=120.377 EndY=46.5474 EndZ=0
    g65: LineSegment StartX=120.635 StartY=53.2507 StartZ=0 EndX=123.265 EndY=51.8068 EndZ=0
    g66: LineSegment StartX=124.73 StartY=54.6766 StartZ=0 EndX=61.5791 EndY=89.3511 EndZ=0
    g67: LineSegment StartX=58.0728 StartY=95.2763 StartZ=0 EndX=58.0728 EndY=110.251 EndZ=0
    g68: LineSegment StartX=61.1495 StartY=111.695 StartZ=0 EndX=119.072 EndY=63.5741 EndZ=0
    g69: LineSegment StartX=120.669 StartY=65.4973 StartZ=0 EndX=115.591 EndY=69.7147 EndZ=0
    g70: LineSegment StartX=117.293 StartY=71.7641 StartZ=0 EndX=122.37 EndY=67.5474 EndZ=0
    g71: LineSegment StartX=123.967 StartY=69.4706 StartZ=0 EndX=61.1496 EndY=121.665 EndZ=0
    g72: LineSegment StartX=62.0728 StartY=124.221 StartZ=0 EndX=132.072 EndY=124.221 EndZ=0
    g73: LineSegment StartX=132.072 StartY=127.221 StartZ=0 EndX=132.072 EndY=124.221 EndZ=0
    g74: LineSegment StartX=132.072 StartY=133.221 StartZ=0 EndX=132.072 EndY=136.221 EndZ=0
    g75: LineSegment StartX=132.072 StartY=136.221 StartZ=0 EndX=-42.9272 EndY=136.221 EndZ=0
    g76: LineSegment StartX=2.07281 StartY=124.221 StartZ=0 EndX=42.0728 EndY=124.221 EndZ=0
    g77: LineSegment StartX=46.0728 StartY=120.221 StartZ=0 EndX=46.0728 EndY=109.865 EndZ=0
    g78: LineSegment StartX=42.0728 StartY=105.865 StartZ=0 EndX=35.5028 EndY=105.865 EndZ=0
    g79: LineSegment StartX=27.9965 StartY=107.79 StartZ=0 EndX=1.57905 EndY=122.295 EndZ=0
    g80: LineSegment StartX=-6.92718 StartY=76.4095 StartZ=0 EndX=42.0728 EndY=76.4095 EndZ=0
    g81: LineSegment StartX=-17.9272 StartY=48.2206 StartZ=0 EndX=-17.9272 EndY=58.2206 EndZ=0
    g82: LineSegment StartX=-35.9272 StartY=48.2206 StartZ=0 EndX=-35.9272 EndY=52.2206 EndZ=0
    g83: LineSegment StartX=-29.9272 StartY=48.2206 StartZ=0 EndX=-29.9272 EndY=52.2206 EndZ=0
    g84: LineSegment StartX=-23.9272 StartY=48.2206 StartZ=0 EndX=-23.9272 EndY=58.2206 EndZ=0
    g85: ArcOfCircle CenterX=-32.9272 CenterY=55.2206 CenterZ=0 NormalX=0 NormalY=0 NormalZ=1 AngleXU=0 Radius=4.24264 StartAngle=5.49779 EndAngle=10.2102
    g86: ArcOfCircle CenterX=-20.9272 CenterY=61.2206 CenterZ=0 NormalX=0 NormalY=0 NormalZ=1 AngleXU=0 Radius=4.24264 StartAngle=5.49779 EndAngle=10.2102
    g87: LineSegment StartX=-10.9272 StartY=48.2206 StartZ=0 EndX=-10.9272 EndY=72.4095 EndZ=0
    g88: LineSegment StartX=-42.9272 StartY=48.2206 StartZ=0 EndX=-42.9272 EndY=136.221 EndZ=0
    g89: LineSegment StartX=46.0728 StartY=72.4095 StartZ=0 EndX=46.0728 EndY=-27.5905 EndZ=0
    g90: LineSegment StartX=58.0728 StartY=-27.5905 StartZ=0 EndX=58.0728 EndY=73.3346 EndZ=0
    g91: LineSegment StartX=50.0728 StartY=-27.5905 StartZ=0 EndX=50.0728 EndY=-31.5905 EndZ=0
    g92: LineSegment StartX=54.0728 StartY=-27.5905 StartZ=0 EndX=54.0728 EndY=-31.5905 EndZ=0
    g93: ArcOfCircle CenterX=52.0728 CenterY=-33.5905 CenterZ=0 NormalX=0 NormalY=0 NormalZ=1 AngleXU=0 Radius=2.82843 StartAngle=2.35619 EndAngle=7.06858
    g94: LineSegment StartX=46.0728 StartY=-27.5905 StartZ=0 EndX=50.0728 EndY=-27.5905 EndZ=0
    g95: LineSegment StartX=54.0728 StartY=-27.5905 StartZ=0 EndX=58.0728 EndY=-27.5905 EndZ=0
    g96: LineSegment StartX=-17.9272 StartY=48.2206 StartZ=0 EndX=-10.9272 EndY=48.2206 EndZ=0
    g97: LineSegment StartX=-29.9272 StartY=48.2206 StartZ=0 EndX=-23.9272 EndY=48.2206 EndZ=0
    g98: LineSegment StartX=-42.9272 StartY=48.2206 StartZ=0 EndX=-35.9272 EndY=48.2206 EndZ=0
  constraints (172):
    c: Weight(g0) = 1
    c: Equal(g0,g1)
    c: Equal(g0,g2)
    c: InternalAlignment(g0,g3)
    c: InternalAlignment(g1,g3)
    c: InternalAlignment(g2,g3)
    c: InternalAlignment(g4,g3)
    c: InternalAlignment(g5,g3)
    c: Weight(g6) = 1
    c: Equal(g6,g7)
    c: Equal(g6,g8)
    c: InternalAlignment(g6,g9)
    c: InternalAlignment(g7,g9)
    c: InternalAlignment(g8,g9)
    c: InternalAlignment(g10,g9)
    c: InternalAlignment(g11,g9)
    c: Block(g3)
    c: Block(g9)
    c: Weight(g12) = 1
    c: Equal(g12,g13)
    c: Equal(g12,g14)
    c: InternalAlignment(g12,g15)
    c: InternalAlignment(g13,g15)
    c: InternalAlignment(g14,g15)
    c: InternalAlignment(g16,g15)
    c: InternalAlignment(g17,g15)
    c: Block(g15)
    c: Weight(g18) = 1
    c: Equal(g18,g19)
    c: Equal(g18,g20)
    c: InternalAlignment(g18,g21)
    c: InternalAlignment(g19,g21)
    c: InternalAlignment(g20,g21)
    c: InternalAlignment(g22,g21)
    c: InternalAlignment(g23,g21)
    c: Block(g21)
    c: Weight(g24) = 1
    c: Equal(g24,g25)
    c: InternalAlignment(g24,g26)
    c: InternalAlignment(g25,g26)
    c: InternalAlignment(g27,g26)
    c: InternalAlignment(g28,g26)
    c: InternalAlignment(g29,g31)
    c: InternalAlignment(g30,g31)
    c: InternalAlignment(g32,g31)
    c: InternalAlignment(g33,g31)
    c: Weight(g34) = 1
    c: Equal(g34,g35)
    c: Equal(g34,g36)
    c: InternalAlignment(g34,g37)
    c: InternalAlignment(g35,g37)
    c: InternalAlignment(g36,g37)
    c: InternalAlignment(g38,g37)
    c: InternalAlignment(g39,g37)
    c: Equal(g40,g41)
    c: Equal(g40,g42)
    c: InternalAlignment(g40,g43)
    c: InternalAlignment(g41,g43)
    c: InternalAlignment(g42,g43)
    c: InternalAlignment(g44,g43)
    c: InternalAlignment(g45,g43)
    c: Block(g31)
    c: Block(g37)
    c: Block(g43)
    c: Block(g26)
    c: Weight(g46) = 1
    c: Equal(g46, g47-g50) x4
    c: InternalAlignment(g46-g50 -> g51) x5
    c: InternalAlignment(g52,g51)
    c: InternalAlignment(g53,g51)
    c: InternalAlignment(g54,g51)
    c: Block(g51)
    c: Block(g55)
    c: Block(g56)
    c: Block(g57)
    c: Block(g58)
    c: Block(g59)
    c: Block(g60)
    c: Block(g61)
    c: Block(g62)
    c: Coincident(g90,g21)
    c: Coincident(g63,g21)
    c: Coincident(g63,g60)
    c: Coincident(g64,g55)
    c: Coincident(g64,g60)
    c: Coincident(g65,g55)
    c: Coincident(g65,g59)
    c: Coincident(g66,g59)
    c: Coincident(g66,g9)
    c: Coincident(g67,g9)
    c: Coincident(g67,g3)
    c: Vertical(g67)
    c: Coincident(g68,g3)
    c: Coincident(g68,g58)
    c: Coincident(g69,g58)
    c: Coincident(g69,g57)
    c: Coincident(g70,g57)
    c: Coincident(g70,g56)
    c: Coincident(g71,g56)
    c: Coincident(g71,g15)
    c: Coincident(g72,g15)
    c: Horizontal(g72)
    c: Coincident(g73,g51)
    c: Coincident(g73,g72)
    c: Vertical(g73)
    c: Coincident(g74,g51)
    c: Vertical(g74)
    c: Coincident(g75,g74)
    c: Horizontal(g75)
    c: Coincident(g76,g26)
    c: Coincident(g76,g31)
    c: Horizontal(g76)
    c: Coincident(g77,g31)
    c: Coincident(g77,g37)
    c: Vertical(g77)
    c: Coincident(g78,g37)
    c: Coincident(g78,g43)
    c: Horizontal(g78)
    c: Coincident(g79,g43)
    c: Coincident(g79,g26)
    c: Coincident(g80,g62)
    c: Coincident(g80,g61)
    c: Horizontal(g80)
    c: Vertical(g81)
    c: Distance(g81) = 10
    c: Vertical(g82)
    c: Distance(g82) = 4
    c: Vertical(g83)
    c: Distance(g83) = 4
    c: Vertical(g84)
    c: Distance(g84) = 10
    c: Coincident(g85,g83)
    c: Coincident(g85,g82)
    c: Block(g85)
    c: Coincident(g86,g84)
    c: Coincident(g86,g81)
    c: Block(g86)
    c: Coincident(g87,g62)
    c: Vertical(g87)
    c: Coincident(g88,g75)
    c: Vertical(g88)
    c: Block(g75)
    c: Coincident(g89,g61)
    c: Vertical(g89)
    c: Distance(g89) = 100
    c: Block(g90)
    c: Vertical(g91)
    c: Distance(g91) = 4
    c: Vertical(g92)
    c: Distance(g92) = 4
    c: Coincident(g93,g91)
    c: Coincident(g93,g92)
    c: Block(g93)
    c: Coincident(g94,g89)
    c: Coincident(g94,g91)
    c: Horizontal(g94)
    c: Distance(g94) = 4
    c: Coincident(g95,g92)
    c: Coincident(g95,g90)
    c: Horizontal(g95)
    c: Distance(g95) = 4
    c: Block(g87)
    c: Block(g88)
    c: Coincident(g96,g81)
    c: Coincident(g96,g87)
    c: Horizontal(g96)
    c: Coincident(g97,g83)
    c: Coincident(g97,g84)
    c: Horizontal(g97)
    c: Coincident(g98,g88)
    c: Coincident(g98,g82)
    c: Horizontal(g98)
FEATURE [Sketcher::SketchObject] Sketch007  label="leftSideBottom"
  FullyConstrained = true
  sketch-geometry (92):
    g0: ArcOfCircle CenterX=-26.9272 CenterY=-83.7794 CenterZ=0 NormalX=0 NormalY=0 NormalZ=1 AngleXU=0 Radius=8 StartAngle=3.14159 EndAngle=6.28319
    g1: Circle CenterX=61.5791 CenterY=-56.9099 CenterZ=0 NormalX=0 NormalY=0 NormalZ=1 AngleXU=0 Radius=1
    g2: Circle CenterX=58.0728 CenterY=-58.8351 CenterZ=0 NormalX=0 NormalY=0 NormalZ=1 AngleXU=0 Radius=1
    g3: Circle CenterX=58.0728 CenterY=-62.8351 CenterZ=0 NormalX=0 NormalY=0 NormalZ=1 AngleXU=0 Radius=1
    g4: BSplineCurve PolesCount=3 KnotsCount=2 Degree=2 IsPeriodic=0
    g5: GeomPoint X=61.5791 Y=-56.9099 Z=0
    g6: GeomPoint X=58.0728 Y=-62.8351 Z=0
    g7: Circle CenterX=58.0728 CenterY=-77.8102 CenterZ=0 NormalX=0 NormalY=0 NormalZ=1 AngleXU=0 Radius=1
    g8: Circle CenterX=58.0728 CenterY=-81.8102 CenterZ=0 NormalX=0 NormalY=0 NormalZ=1 AngleXU=0 Radius=1
    g9: Circle CenterX=61.1496 CenterY=-79.2541 CenterZ=0 NormalX=0 NormalY=0 NormalZ=1 AngleXU=0 Radius=1
    g10: BSplineCurve PolesCount=3 KnotsCount=2 Degree=2 IsPeriodic=0
    g11: GeomPoint X=58.0728 Y=-77.8102 Z=0
    g12: GeomPoint X=61.1496 Y=-79.2541 Z=0
    g13: Circle CenterX=61.6457 CenterY=-88.8112 CenterZ=0 NormalX=0 NormalY=0 NormalZ=1 AngleXU=0 Radius=1
    g14: Circle CenterX=58.0728 CenterY=-91.7794 CenterZ=0 NormalX=0 NormalY=0 NormalZ=1 AngleXU=0 Radius=1
    g15: Circle CenterX=63.9135 CenterY=-91.8014 CenterZ=0 NormalX=0 NormalY=0 NormalZ=1 AngleXU=0 Radius=1
    g16: BSplineCurve PolesCount=3 KnotsCount=2 Degree=2 IsPeriodic=0
    g17: GeomPoint X=61.6457 Y=-88.8112 Z=0
    g18: GeomPoint X=63.9135 Y=-91.8014 Z=0
    g19: Circle CenterX=58.0728 CenterY=-40.8935 CenterZ=0 NormalX=0 NormalY=0 NormalZ=1 AngleXU=0 Radius=1
    g20: Circle CenterX=58.0728 CenterY=-44.8935 CenterZ=0 NormalX=0 NormalY=0 NormalZ=1 AngleXU=0 Radius=1
    g21: Circle CenterX=61.5791 CenterY=-42.9683 CenterZ=0 NormalX=0 NormalY=0 NormalZ=1 AngleXU=0 Radius=1
    g22: BSplineCurve PolesCount=3 KnotsCount=2 Degree=2 IsPeriodic=0
    g23: GeomPoint X=58.0728 Y=-40.8935 Z=0
    g24: GeomPoint X=61.5791 Y=-42.9683 Z=0
    g25: Circle CenterX=42.5666 CenterY=-67.3492 CenterZ=0 NormalX=0 NormalY=0 NormalZ=1 AngleXU=0 Radius=1
    g26: Circle CenterX=46.0728 CenterY=-65.424 CenterZ=0 NormalX=0 NormalY=0 NormalZ=1 AngleXU=0 Radius=1
    g27: Circle CenterX=46.0728 CenterY=-69.424 CenterZ=0 NormalX=0 NormalY=0 NormalZ=1 AngleXU=0 Radius=1
    g28: BSplineCurve PolesCount=3 KnotsCount=2 Degree=2 IsPeriodic=0
    g29: GeomPoint X=42.5666 Y=-67.3492 Z=0
    g30: GeomPoint X=46.0728 Y=-69.424 Z=0
    g31: Circle CenterX=2.07281 CenterY=-91.7794 CenterZ=0 NormalX=0 NormalY=0 NormalZ=1 AngleXU=0 Radius=1
    g32: Circle CenterX=-1.92719 CenterY=-91.7794 CenterZ=0 NormalX=0 NormalY=0 NormalZ=1 AngleXU=0 Radius=1
    g33: Circle CenterX=1.57905 CenterY=-89.8542 CenterZ=0 NormalX=0 NormalY=0 NormalZ=1 AngleXU=0 Radius=1
    g34: BSplineCurve PolesCount=3 KnotsCount=2 Degree=2 IsPeriodic=0
    g35: GeomPoint X=2.07281 Y=-91.7794 Z=0
    g36: GeomPoint X=1.57905 Y=-89.8542 Z=0
    g37: ArcOfCircle CenterX=-26.9272 CenterY=22.1087 CenterZ=0 NormalX=0 NormalY=0 NormalZ=1 AngleXU=0 Radius=4 StartAngle=5e-16 EndAngle=3.14159
    g38: Circle CenterX=-10.9272 CenterY=-78.7794 CenterZ=0 NormalX=0 NormalY=0 NormalZ=1 AngleXU=0 Radius=1
    g39: Circle CenterX=-10.9272 CenterY=-82.7794 CenterZ=0 NormalX=0 NormalY=0 NormalZ=1 AngleXU=0 Radius=1
    g40: Circle CenterX=-7.42095 CenterY=-80.8542 CenterZ=0 NormalX=0 NormalY=0 NormalZ=1 AngleXU=0 Radius=1
    g41: BSplineCurve PolesCount=3 KnotsCount=2 Degree=2 IsPeriodic=0
    g42: GeomPoint X=-10.9272 Y=-78.7794 Z=0
    g43: GeomPoint X=-7.42095 Y=-80.8542 Z=0
    g44: BSplineCurve PolesCount=3 KnotsCount=2 Degree=2 IsPeriodic=0
    g45: GeomPoint X=42.5666 Y=-53.4075 Z=0
    g46: GeomPoint X=46.0728 Y=-47.4823 Z=0
    g47: BSplineCurve PolesCount=5 KnotsCount=3 Degree=3 IsPeriodic=0
    g48: LineSegment StartX=124.814 StartY=-22.1885 StartZ=0 EndX=123.265 EndY=-19.3655 EndZ=0
    g49: ArcOfCircle CenterX=116.562 CenterY=-19.6236 CenterZ=0 NormalX=0 NormalY=0 NormalZ=1 AngleXU=0 Radius=4.24264 StartAngle=1.28753 EndAngle=6.00037
    g50: LineSegment StartX=-30.9272 StartY=22.1087 StartZ=0 EndX=-34.9272 EndY=-83.7794 EndZ=0
    g51: LineSegment StartX=-22.9272 StartY=22.1087 StartZ=0 EndX=-18.9272 EndY=-83.7794 EndZ=0
    g52: LineSegment StartX=118.934 StartY=-11.4765 StartZ=0 EndX=120.377 EndY=-14.1062 EndZ=0
    g53: LineSegment StartX=118.86 StartY=-31.3104 StartZ=0 EndX=120.377 EndY=-33.1447 EndZ=0
    g54: LineSegment StartX=115.291 StartY=-37.3514 StartZ=0 EndX=117.05 EndY=-39.4781 EndZ=0
    g55: LineSegment StartX=122.136 StartY=-35.2714 StartZ=0 EndX=123.656 EndY=-37.1092 EndZ=0
    g56: BSplineCurve PolesCount=3 KnotsCount=2 Degree=2 IsPeriodic=0
    g57: LineSegment StartX=132.072 StartY=-100.779 StartZ=0 EndX=132.072 EndY=-103.779 EndZ=0
    g58: LineSegment StartX=132.072 StartY=-91.8014 StartZ=0 EndX=132.072 EndY=-94.7791 EndZ=0
    g59: LineSegment StartX=63.9135 StartY=-91.8014 StartZ=0 EndX=132.072 EndY=-91.8014 EndZ=0
    g60: LineSegment StartX=61.6457 StartY=-88.8112 StartZ=0 EndX=123.656 EndY=-37.1092 EndZ=0
    g61: LineSegment StartX=122.136 StartY=-35.2714 StartZ=0 EndX=117.05 EndY=-39.4781 EndZ=0
    g62: LineSegment StartX=115.291 StartY=-37.3514 StartZ=0 EndX=120.377 EndY=-33.1447 EndZ=0
    g63: LineSegment StartX=118.86 StartY=-31.3104 StartZ=0 EndX=61.1496 EndY=-79.2541 EndZ=0
    g64: LineSegment StartX=58.0728 StartY=-77.8102 StartZ=0 EndX=58.0728 EndY=-62.8351 EndZ=0
    g65: LineSegment StartX=61.5791 StartY=-56.9099 StartZ=0 EndX=124.814 EndY=-22.1885 EndZ=0
    g66: LineSegment StartX=120.636 StartY=-20.8076 StartZ=0 EndX=123.265 EndY=-19.3655 EndZ=0
    g67: LineSegment StartX=117.748 StartY=-15.55 StartZ=0 EndX=120.377 EndY=-14.1062 EndZ=0
    g68: LineSegment StartX=118.934 StartY=-11.4765 StartZ=0 EndX=61.5791 EndY=-42.9683 EndZ=0
    g69: LineSegment StartX=-42.9272 StartY=-103.779 StartZ=0 EndX=132.072 EndY=-103.779 EndZ=0
    g70: LineSegment StartX=42.5666 StartY=-53.4075 StartZ=0 EndX=-7.42095 EndY=-80.8542 EndZ=0
    g71: LineSegment StartX=-10.9272 StartY=-78.7794 StartZ=0 EndX=-10.9272 EndY=48.2206 EndZ=0
    g72: LineSegment StartX=2.07281 StartY=-91.7794 StartZ=0 EndX=42.0728 EndY=-91.7794 EndZ=0
    g73: LineSegment StartX=46.0728 StartY=-87.7794 StartZ=0 EndX=46.0728 EndY=-69.424 EndZ=0
    g74: LineSegment StartX=42.5666 StartY=-67.3492 StartZ=0 EndX=1.57905 EndY=-89.8542 EndZ=0
    g75: LineSegment StartX=-42.9272 StartY=-103.779 StartZ=0 EndX=-42.9272 EndY=48.2206 EndZ=0
    g76: LineSegment StartX=-17.9272 StartY=48.2206 StartZ=0 EndX=-17.9272 EndY=58.2206 EndZ=0
    g77: LineSegment StartX=-35.9272 StartY=48.2206 StartZ=0 EndX=-35.9272 EndY=52.2206 EndZ=0
    g78: LineSegment StartX=-29.9272 StartY=48.2206 StartZ=0 EndX=-29.9272 EndY=52.2206 EndZ=0
    g79: LineSegment StartX=-23.9272 StartY=48.2206 StartZ=0 EndX=-23.9272 EndY=58.2206 EndZ=0
    g80: ArcOfCircle CenterX=-32.9272 CenterY=55.2206 CenterZ=0 NormalX=0 NormalY=0 NormalZ=1 AngleXU=0 Radius=4.24264 StartAngle=5.49779 EndAngle=10.2102
    g81: ArcOfCircle CenterX=-20.9272 CenterY=61.2206 CenterZ=0 NormalX=0 NormalY=0 NormalZ=1 AngleXU=0 Radius=4.24264 StartAngle=5.49779 EndAngle=10.2102
    g82: LineSegment StartX=-17.9272 StartY=48.2206 StartZ=0 EndX=-10.9272 EndY=48.2206 EndZ=0
    g83: LineSegment StartX=-42.9272 StartY=48.2206 StartZ=0 EndX=-35.9272 EndY=48.2206 EndZ=0
    g84: LineSegment StartX=50.0728 StartY=-27.5905 StartZ=0 EndX=50.0728 EndY=-31.5905 EndZ=0
    g85: LineSegment StartX=54.0728 StartY=-27.5905 StartZ=0 EndX=54.0728 EndY=-31.5905 EndZ=0
    g86: ArcOfCircle CenterX=52.0728 CenterY=-33.5905 CenterZ=0 NormalX=0 NormalY=0 NormalZ=1 AngleXU=0 Radius=2.82843 StartAngle=2.35619 EndAngle=7.06858
    g87: LineSegment StartX=46.0728 StartY=-27.5905 StartZ=0 EndX=50.0728 EndY=-27.5905 EndZ=0
    g88: LineSegment StartX=54.0728 StartY=-27.5905 StartZ=0 EndX=58.0728 EndY=-27.5905 EndZ=0
    g89: LineSegment StartX=46.0728 StartY=-27.5905 StartZ=0 EndX=46.0728 EndY=-47.4823 EndZ=0
    g90: LineSegment StartX=58.0728 StartY=-27.5905 StartZ=0 EndX=58.0728 EndY=-40.8935 EndZ=0
    g91: LineSegment StartX=-29.9272 StartY=48.2206 StartZ=0 EndX=-23.9272 EndY=48.2206 EndZ=0
  constraints (170):
    c: Weight(g1) = 1
    c: Equal(g1,g2)
    c: Equal(g1,g3)
    c: InternalAlignment(g1,g4)
    c: InternalAlignment(g2,g4)
    c: InternalAlignment(g3,g4)
    c: InternalAlignment(g5,g4)
    c: InternalAlignment(g6,g4)
    c: Weight(g7) = 1
    c: Equal(g7,g8)
    c: Equal(g7,g9)
    c: InternalAlignment(g7,g10)
    c: InternalAlignment(g8,g10)
    c: InternalAlignment(g9,g10)
    c: InternalAlignment(g11,g10)
    c: InternalAlignment(g12,g10)
    c: Block(g4)
    c: Block(g10)
    c: Weight(g13) = 1
    c: Equal(g13,g14)
    c: Equal(g13,g15)
    c: InternalAlignment(g13,g16)
    c: InternalAlignment(g14,g16)
    c: InternalAlignment(g15,g16)
    c: InternalAlignment(g17,g16)
    c: InternalAlignment(g18,g16)
    c: Block(g16)
    c: Weight(g19) = 1
    c: Equal(g19,g20)
    c: Equal(g19,g21)
    c: InternalAlignment(g19,g22)
    c: InternalAlignment(g20,g22)
    c: InternalAlignment(g21,g22)
    c: InternalAlignment(g23,g22)
    c: InternalAlignment(g24,g22)
    c: Block(g22)
    c: Weight(g25) = 1
    c: Equal(g25,g26)
    c: Equal(g25,g27)
    c: InternalAlignment(g25,g28)
    c: InternalAlignment(g26,g28)
    c: InternalAlignment(g27,g28)
    c: InternalAlignment(g29,g28)
    c: InternalAlignment(g30,g28)
    c: Weight(g31) = 1
    c: Equal(g31,g32)
    c: Equal(g31,g33)
    c: InternalAlignment(g31,g34)
    c: InternalAlignment(g32,g34)
    c: InternalAlignment(g33,g34)
    c: InternalAlignment(g35,g34)
    c: InternalAlignment(g36,g34)
    c: Block(g34)
    c: Block(g28)
    c: Block(g37)
    c: Block(g0)
    c: Weight(g38) = 1
    c: Equal(g38,g40)
    c: InternalAlignment(g38,g41)
    c: InternalAlignment(g39,g41)
    c: InternalAlignment(g40,g41)
    c: InternalAlignment(g42,g41)
    c: InternalAlignment(g43,g41)
    c: InternalAlignment(g45,g44)
    c: InternalAlignment(g46,g44)
    c: Block(g47)
    c: Block(g44)
    c: Block(g41)
    c: Block(g48)
    c: Block(g49)
    c: Coincident(g50,g37)
    c: Coincident(g50,g0)
    c: Coincident(g51,g37)
    c: Coincident(g51,g0)
    c: Block(g51)
    c: Block(g50)
    c: Block(g52)
    c: Block(g53)
    c: Block(g54)
    c: Block(g55)
    c: Block(g56)
    c: Coincident(g57,g47)
    c: Vertical(g57)
    c: Coincident(g58,g47)
    c: Vertical(g58)
    c: Coincident(g59,g16)
    c: Coincident(g59,g58)
    c: Horizontal(g59)
    c: Coincident(g60,g16)
    c: Coincident(g60,g55)
    c: Coincident(g61,g55)
    c: Coincident(g61,g54)
    c: Coincident(g62,g54)
    c: Coincident(g62,g53)
    c: Coincident(g63,g53)
    c: Coincident(g63,g10)
    c: Coincident(g64,g10)
    c: Coincident(g64,g4)
    c: Vertical(g64)
    c: Coincident(g65,g4)
    c: Coincident(g65,g48)
    c: Coincident(g66,g49)
    c: Coincident(g66,g48)
    c: Coincident(g67,g49)
    c: Coincident(g67,g52)
    c: Coincident(g68,g52)
    c: Coincident(g68,g22)
    c: Coincident(g69,g57)
    c: Horizontal(g69)
    c: Coincident(g70,g44)
    c: Coincident(g70,g41)
    c: Coincident(g71,g41)
    c: Vertical(g71)
    c: Coincident(g72,g34)
    c: Coincident(g72,g56)
    c: Horizontal(g72)
    c: Coincident(g73,g56)
    c: Coincident(g73,g28)
    c: Vertical(g73)
    c: Coincident(g74,g28)
    c: Coincident(g74,g34)
    c: Block(g69)
    c: Coincident(g75,g69)
    c: Vertical(g75)
    c: Distance(g75) = 152
    c: Block(g71)
    c: Vertical(g76)
    c: Distance(g76) = 10
    c: Vertical(g77)
    c: Distance(g77) = 4
    c: Vertical(g78)
    c: Distance(g78) = 4
    c: Vertical(g79)
    c: Distance(g79) = 10
    c: Coincident(g80,g78)
    c: Coincident(g80,g77)
    c: Block(g80)
    c: Coincident(g81,g79)
    c: Coincident(g81,g76)
    c: Block(g81)
    c: Coincident(g82,g76)
    c: Coincident(g82,g71)
    c: Horizontal(g82)
    c: Coincident(g83,g75)
    c: Coincident(g83,g77)
    c: Horizontal(g83)
    c: Distance(g83) = 7
    c: Distance(g82) = 7
    c: Vertical(g84)
    c: Distance(g84) = 4
    c: Vertical(g85)
    c: Distance(g85) = 4
    c: Coincident(g86,g84)
    c: Coincident(g86,g85)
    c: Block(g86)
    c: Coincident(g87,g84)
    c: Horizontal(g87)
    c: Distance(g87) = 4
    c: Coincident(g88,g85)
    c: Horizontal(g88)
    c: Distance(g88) = 4
    c: Coincident(g89,g87)
    c: Coincident(g89,g44)
    c: Vertical(g89)
    c: Coincident(g90,g88)
    c: Coincident(g90,g22)
    c: Vertical(g90)
    c: Coincident(g91,g78)
    c: Coincident(g91,g79)
    c: Horizontal(g91)
FEATURE [Sketcher::SketchObject] Sketch008  label="rightSideTop"
  FullyConstrained = false
  sketch-geometry (108):
    g0: Circle CenterX=302.996 CenterY=111.695 CenterZ=0 NormalX=0 NormalY=0 NormalZ=1 AngleXU=0 Radius=1
    g1: Circle CenterX=306.073 CenterY=114.251 CenterZ=0 NormalX=0 NormalY=0 NormalZ=1 AngleXU=0 Radius=1
    g2: Circle CenterX=306.073 CenterY=110.251 CenterZ=0 NormalX=0 NormalY=0 NormalZ=1 AngleXU=0 Radius=1
    g3: BSplineCurve PolesCount=3 KnotsCount=2 Degree=2 IsPeriodic=0
    g4: GeomPoint X=302.996 Y=111.695 Z=0
    g5: GeomPoint X=306.073 Y=110.251 Z=0
    g6: Circle CenterX=306.073 CenterY=95.2763 CenterZ=0 NormalX=0 NormalY=0 NormalZ=1 AngleXU=0 Radius=1
    g7: Circle CenterX=306.073 CenterY=91.2763 CenterZ=0 NormalX=0 NormalY=0 NormalZ=1 AngleXU=0 Radius=1
    g8: Circle CenterX=302.567 CenterY=89.3511 CenterZ=0 NormalX=0 NormalY=0 NormalZ=1 AngleXU=0 Radius=1
    g9: BSplineCurve PolesCount=3 KnotsCount=2 Degree=2 IsPeriodic=0
    g10: GeomPoint X=306.073 Y=95.2763 Z=0
    g11: GeomPoint X=302.567 Y=89.3511 Z=0
    g12: LineSegment StartX=306.073 StartY=110.251 StartZ=0 EndX=306.073 EndY=95.2763 EndZ=0
    g13: Circle CenterX=302.073 CenterY=124.221 CenterZ=0 NormalX=0 NormalY=0 NormalZ=1 AngleXU=0 Radius=1
    g14: Circle CenterX=306.073 CenterY=124.221 CenterZ=0 NormalX=0 NormalY=0 NormalZ=1 AngleXU=0 Radius=1
    g15: Circle CenterX=302.996 CenterY=121.665 CenterZ=0 NormalX=0 NormalY=0 NormalZ=1 AngleXU=0 Radius=1
    g16: BSplineCurve PolesCount=3 KnotsCount=2 Degree=2 IsPeriodic=0
    g17: GeomPoint X=302.073 Y=124.221 Z=0
    g18: GeomPoint X=302.996 Y=121.665 Z=0
    g19: Circle CenterX=306.073 CenterY=73.3346 CenterZ=0 NormalX=0 NormalY=0 NormalZ=1 AngleXU=0 Radius=1
    g20: Circle CenterX=306.073 CenterY=77.3346 CenterZ=0 NormalX=0 NormalY=0 NormalZ=1 AngleXU=0 Radius=1
    g21: Circle CenterX=302.535 CenterY=75.4095 CenterZ=0 NormalX=0 NormalY=0 NormalZ=1 AngleXU=0 Radius=1
    g22: BSplineCurve PolesCount=3 KnotsCount=2 Degree=2 IsPeriodic=0
    g23: GeomPoint X=306.073 Y=73.3346 Z=0
    g24: GeomPoint X=302.535 Y=75.4095 Z=0
    g25: Circle CenterX=362.073 CenterY=124.221 CenterZ=0 NormalX=0 NormalY=0 NormalZ=1 AngleXU=0 Radius=1
    g26: Circle CenterX=366.073 CenterY=124.221 CenterZ=0 NormalX=0 NormalY=0 NormalZ=1 AngleXU=0 Radius=1
    g27: Circle CenterX=362.567 CenterY=122.294 CenterZ=0 NormalX=0 NormalY=0 NormalZ=1 AngleXU=0 Radius=1
    g28: BSplineCurve PolesCount=3 KnotsCount=2 Degree=2 IsPeriodic=0
    g29: GeomPoint X=362.073 Y=124.221 Z=0
    g30: GeomPoint X=362.567 Y=122.294 Z=0
    g31: Circle CenterX=322.073 CenterY=124.221 CenterZ=0 NormalX=0 NormalY=0 NormalZ=1 AngleXU=0 Radius=1
    g32: Circle CenterX=318.073 CenterY=124.221 CenterZ=0 NormalX=0 NormalY=0 NormalZ=1 AngleXU=0 Radius=1
    g33: Circle CenterX=318.073 CenterY=120.221 CenterZ=0 NormalX=0 NormalY=0 NormalZ=1 AngleXU=0 Radius=1
    g34: BSplineCurve PolesCount=3 KnotsCount=2 Degree=2 IsPeriodic=0
    g35: GeomPoint X=322.073 Y=124.221 Z=0
    g36: GeomPoint X=318.073 Y=120.221 Z=0
    g37: Circle CenterX=322.073 CenterY=105.865 CenterZ=0 NormalX=0 NormalY=0 NormalZ=1 AngleXU=0 Radius=1
    g38: Circle CenterX=318.073 CenterY=105.865 CenterZ=0 NormalX=0 NormalY=0 NormalZ=1 AngleXU=0 Radius=1
    g39: Circle CenterX=318.073 CenterY=109.865 CenterZ=0 NormalX=0 NormalY=0 NormalZ=1 AngleXU=0 Radius=1
    g40: BSplineCurve PolesCount=3 KnotsCount=2 Degree=2 IsPeriodic=0
    g41: GeomPoint X=322.073 Y=105.865 Z=0
    g42: GeomPoint X=318.073 Y=109.865 Z=0
    g43: Circle CenterX=336.157 CenterY=107.779 CenterZ=0 NormalX=0 NormalY=0 NormalZ=1 AngleXU=0 Radius=1
    g44: Circle CenterX=332.651 CenterY=105.853 CenterZ=0 NormalX=0 NormalY=0 NormalZ=1 AngleXU=0 Radius=1
    g45: Circle CenterX=328.643 CenterY=105.865 CenterZ=0 NormalX=0 NormalY=0 NormalZ=1 AngleXU=0 Radius=1
    g46: BSplineCurve PolesCount=3 KnotsCount=2 Degree=2 IsPeriodic=0
    g47: GeomPoint X=336.157 Y=107.779 Z=0
    g48: GeomPoint X=328.643 Y=105.865 Z=0
    g49: Circle CenterX=322.073 CenterY=76.4095 CenterZ=0 NormalX=0 NormalY=0 NormalZ=1 AngleXU=0 Radius=4
    g50: BSplineCurve PolesCount=3 KnotsCount=2 Degree=2 IsPeriodic=0
    g51: GeomPoint X=318.073 Y=72.4095 Z=0
    g52: GeomPoint X=322.073 Y=76.4095 Z=0
    g53: Circle CenterX=375.073 CenterY=72.4095 CenterZ=0 NormalX=0 NormalY=0 NormalZ=1 AngleXU=0 Radius=1
    g54: Circle CenterX=375.073 CenterY=76.4095 CenterZ=0 NormalX=0 NormalY=0 NormalZ=1 AngleXU=0 Radius=1
    g55: Circle CenterX=371.073 CenterY=76.4095 CenterZ=0 NormalX=0 NormalY=0 NormalZ=1 AngleXU=0 Radius=1
    g56: BSplineCurve PolesCount=3 KnotsCount=2 Degree=2 IsPeriodic=0
    g57: GeomPoint X=375.073 Y=72.4095 Z=0
    g58: GeomPoint X=371.073 Y=76.4095 Z=0
    g59: LineSegment StartX=322.073 StartY=76.4095 StartZ=0 EndX=371.073 EndY=76.4095 EndZ=0
    g60: Circle CenterX=232.072 CenterY=133.221 CenterZ=0 NormalX=0 NormalY=0 NormalZ=1 AngleXU=0 Radius=1
    g61: Circle CenterX=226.072 CenterY=136.221 CenterZ=0 NormalX=0 NormalY=0 NormalZ=1 AngleXU=0 Radius=1
    g62: Circle CenterX=226.072 CenterY=124.221 CenterZ=0 NormalX=0 NormalY=0 NormalZ=1 AngleXU=0 Radius=1
    g63: Circle CenterX=232.072 CenterY=127.221 CenterZ=0 NormalX=0 NormalY=0 NormalZ=1 AngleXU=0 Radius=1
    g64: BSplineCurve PolesCount=5 KnotsCount=3 Degree=3 IsPeriodic=0
    g65: GeomPoint X=232.072 Y=133.221 Z=0
    g66: GeomPoint X=223.072 Y=130.221 Z=0
    g67: GeomPoint X=232.072 Y=127.221 Z=0
    g68: LineSegment StartX=240.687 StartY=51.8263 StartZ=0 EndX=243.317 EndY=53.2701 EndZ=0
    g69: LineSegment StartX=243.575 StartY=46.5669 StartZ=0 EndX=246.205 EndY=48.0108 EndZ=0
    g70: ArcOfCircle CenterX=247.391 CenterY=52.0843 CenterZ=0 NormalX=0 NormalY=0 NormalZ=1 AngleXU=0 Radius=4.24264 StartAngle=4.42912 EndAngle=9.14151
    g71: LineSegment StartX=243.475 StartY=65.4951 StartZ=0 EndX=245.073 EndY=63.5726 EndZ=0
    g72: LineSegment StartX=243.575 StartY=46.5669 StartZ=0 EndX=245.072 EndY=43.8408 EndZ=0
    g73: LineSegment StartX=245.072 StartY=43.8408 StartZ=0 EndX=302.535 EndY=75.4095 EndZ=0
    g74: LineSegment StartX=239.192 StartY=54.5542 StartZ=0 EndX=302.567 EndY=89.3511 EndZ=0
    g75: LineSegment StartX=232.072 StartY=127.221 StartZ=0 EndX=232.072 EndY=124.221 EndZ=0
    g76: LineSegment StartX=232.072 StartY=136.221 StartZ=0 EndX=232.072 EndY=133.221 EndZ=0
    g77: LineSegment StartX=232.072 StartY=136.221 StartZ=0 EndX=407.073 EndY=136.221 EndZ=0
    g78: LineSegment StartX=322.073 StartY=124.221 StartZ=0 EndX=362.073 EndY=124.221 EndZ=0
    g79: LineSegment StartX=362.567 StartY=122.294 StartZ=0 EndX=336.157 EndY=107.779 EndZ=0
    g80: LineSegment StartX=322.073 StartY=105.865 StartZ=0 EndX=328.643 EndY=105.865 EndZ=0
    g81: LineSegment StartX=318.073 StartY=120.221 StartZ=0 EndX=318.073 EndY=109.865 EndZ=0
    g82: LineSegment StartX=232.072 StartY=124.221 StartZ=0 EndX=302.073 EndY=124.221 EndZ=0
    g83: LineSegment StartX=302.996 StartY=121.665 StartZ=0 EndX=240.171 EndY=69.471 EndZ=0
    g84: LineSegment StartX=240.171 StartY=69.471 StartZ=0 EndX=241.711 EndY=67.6177 EndZ=0
    g85: LineSegment StartX=241.711 StartY=67.6177 StartZ=0 EndX=246.787 EndY=71.8365 EndZ=0
    g86: LineSegment StartX=246.787 StartY=71.8365 StartZ=0 EndX=248.551 EndY=69.712 EndZ=0
    g87: LineSegment StartX=248.551 StartY=69.712 StartZ=0 EndX=243.475 EndY=65.4951 EndZ=0
    g88: LineSegment StartX=245.073 StartY=63.5726 StartZ=0 EndX=302.996 EndY=111.695 EndZ=0
    g89: LineSegment StartX=239.192 StartY=54.5542 StartZ=0 EndX=240.687 EndY=51.8263 EndZ=0
    g90: LineSegment StartX=375.073 StartY=48.2206 StartZ=0 EndX=382.073 EndY=48.2206 EndZ=0
    g91: LineSegment StartX=407.073 StartY=48.2206 StartZ=0 EndX=400.073 EndY=48.2206 EndZ=0
    g92: LineSegment StartX=394.073 StartY=48.2206 StartZ=0 EndX=394.073 EndY=52.2206 EndZ=0
    g93: LineSegment StartX=388.073 StartY=48.2206 StartZ=0 EndX=388.073 EndY=58.2206 EndZ=0
    g94: ArcOfCircle CenterX=385.073 CenterY=61.2206 CenterZ=0 NormalX=0 NormalY=0 NormalZ=1 AngleXU=0 Radius=4.24264 StartAngle=5.49779 EndAngle=10.2102
    g95: ArcOfCircle CenterX=397.073 CenterY=55.2206 CenterZ=0 NormalX=0 NormalY=0 NormalZ=1 AngleXU=0 Radius=4.24264 StartAngle=5.49779 EndAngle=10.2102
    g96: LineSegment StartX=382.073 StartY=58.2206 StartZ=0 EndX=382.073 EndY=48.2206 EndZ=0
    g97: LineSegment StartX=400.073 StartY=52.2206 StartZ=0 EndX=400.073 EndY=48.2206 EndZ=0
    g98: LineSegment StartX=394.073 StartY=48.2206 StartZ=0 EndX=388.073 EndY=48.2206 EndZ=0
    g99: LineSegment StartX=306.073 StartY=-27.5935 StartZ=0 EndX=310.073 EndY=-27.5935 EndZ=0
    g100: LineSegment StartX=318.073 StartY=-27.5935 StartZ=0 EndX=314.073 EndY=-27.5935 EndZ=0
    g101: LineSegment StartX=310.073 StartY=-27.5935 StartZ=0 EndX=310.073 EndY=-31.5935 EndZ=0
    g102: LineSegment StartX=314.073 StartY=-27.5935 StartZ=0 EndX=314.073 EndY=-31.5935 EndZ=0
    g103: ArcOfCircle CenterX=312.073 CenterY=-33.5935 CenterZ=0 NormalX=0 NormalY=0 NormalZ=1 AngleXU=0 Radius=2.82843 StartAngle=2.35619 EndAngle=7.06858
    g104: LineSegment StartX=375.073 StartY=72.4095 StartZ=0 EndX=375.073 EndY=48.2206 EndZ=0
    g105: LineSegment StartX=407.073 StartY=48.2206 StartZ=0 EndX=407.073 EndY=136.221 EndZ=0
    g106: LineSegment StartX=318.073 StartY=-27.5935 StartZ=0 EndX=318.073 EndY=72.4095 EndZ=0
    g107: LineSegment StartX=306.073 StartY=73.3346 StartZ=0 EndX=306.073 EndY=-27.5935 EndZ=0
  constraints (136):
    c: Weight(g0) = 1
    c: Equal(g0,g1)
    c: Equal(g0,g2)
    c: InternalAlignment(g0,g3)
    c: InternalAlignment(g1,g3)
    c: InternalAlignment(g2,g3)
    c: InternalAlignment(g4,g3)
    c: InternalAlignment(g5,g3)
    c: Weight(g6) = 1
    c: Equal(g6,g7)
    c: Equal(g6,g8)
    c: InternalAlignment(g6,g9)
    c: InternalAlignment(g7,g9)
    c: InternalAlignment(g8,g9)
    c: InternalAlignment(g10,g9)
    c: InternalAlignment(g11,g9)
    c: Block(g3)
    c: Block(g9)
    c: Coincident(g12,g3)
    c: Coincident(g12,g9)
    c: Vertical(g12)
    c: Weight(g13) = 1
    c: Equal(g13,g14)
    c: Equal(g13,g15)
    c: InternalAlignment(g14,g16)
    c: InternalAlignment(g15,g16)
    c: InternalAlignment(g17,g16)
    c: InternalAlignment(g18,g16)
    c: Block(g71)
    c: Block(g72)
    c: Coincident(g73,g72)
    c: Coincident(g73,g22)
    c: Block(g73)
    c: Coincident(g70,g69)
    c: Coincident(g70,g68)
    c: Coincident(g74,g9)
    c: Block(g74)
    c: Distance(g71) = 2.5
    c: Block(g64)
    c: Block(g46)
    c: Block(g59)
    c: Coincident(g75,g64)
    c: Vertical(g75)
    c: Coincident(g76,g64)
    c: Vertical(g76)
    c: Coincident(g77,g76)
    c: Horizontal(g77)
    c: Coincident(g78,g34)
    c: Coincident(g78,g28)
    c: Horizontal(g78)
    c: Coincident(g79,g28)
    c: Coincident(g79,g46)
    c: Coincident(g80,g40)
    c: Coincident(g80,g46)
    c: Horizontal(g80)
    c: Coincident(g81,g34)
    c: Coincident(g81,g40)
    c: Vertical(g81)
    c: Block(g34)
    c: Block(g40)
    c: Block(g28)
    c: Coincident(g82,g75)
    c: Coincident(g82,g16)
    c: Horizontal(g82)
    c: Coincident(g83,g16)
    c: Block(g82)
    c: Block(g83)
    c: Block(g16)
    c: Coincident(g84,g83)
    c: Block(g84)
    c: Coincident(g85,g84)
    c: Block(g85)
    c: Coincident(g86,g85)
    c: Coincident(g87,g86)
    c: Coincident(g87,g71)
    c: Block(g87)
    c: Coincident(g88,g71)
    c: Coincident(g88,g3)
    c: Block(g88)
    c: Coincident(g89,g74)
    c: Coincident(g89,g68)
    c: Block(g70)
    c: Block(g68)
    c: Block(g69)
    c: Block(g22)
    c: Block(g50)
    c: Block(g56)
    c: Horizontal(g90)
    c: Distance(g90) = 7
    c: Horizontal(g91)
    c: Distance(g91) = 7
    c: Vertical(g92)
    c: Distance(g92) = 4
    c: Vertical(g93)
    c: Distance(g93) = 10
    c: Coincident(g94,g93)
    c: Coincident(g95,g92)
    c: Block(g95)
    c: Block(g94)
    c: Coincident(g96,g94)
    c: Coincident(g96,g90)
    c: Vertical(g96)
    c: Coincident(g97,g95)
    c: Coincident(g97,g91)
    c: Vertical(g97)
    c: Coincident(g98,g92)
    c: Coincident(g98,g93)
    c: Horizontal(g98)
    c: Horizontal(g99)
    c: Distance(g99) = 4
    c: Horizontal(g100)
    c: Distance(g100) = 4
    c: Coincident(g101,g99)
    c: Vertical(g101)
    c: Coincident(g102,g100)
    c: Vertical(g102)
    c: Distance(g101) = 4
    c: Distance(g102) = 4
    c: Coincident(g103,g101)
    c: Coincident(g103,g102)
    c: Block(g103)
    c: Coincident(g104,g56)
    c: Coincident(g104,g90)
    c: Vertical(g104)
    c: Block(g104)
    c: Coincident(g105,g91)
    c: Coincident(g105,g77)
    c: Vertical(g105)
    c: Block(g77)
    c: Block(g105)
    c: Coincident(g106,g100)
    c: Coincident(g106,g50)
    c: Vertical(g106)
    c: Coincident(g107,g22)
    c: Coincident(g107,g99)
    c: Vertical(g107)
FEATURE [Sketcher::SketchObject] Sketch009  label="middleBottom"
  FullyConstrained = true
  sketch-geometry (109):
    g0: Circle CenterX=175.022 CenterY=5.37834 CenterZ=0 NormalX=0 NormalY=0 NormalZ=1 AngleXU=0 Radius=1
    g1: Circle CenterX=179.022 CenterY=7.57463 CenterZ=0 NormalX=0 NormalY=0 NormalZ=1 AngleXU=0 Radius=1
    g2: Circle CenterX=179.022 CenterY=5.34704 CenterZ=0 NormalX=0 NormalY=0 NormalZ=1 AngleXU=0 Radius=1
    g3: BSplineCurve PolesCount=3 KnotsCount=2 Degree=2 IsPeriodic=0
    g4: GeomPoint X=175.022 Y=5.37834 Z=0
    g5: GeomPoint X=179.022 Y=5.34704 Z=0
    g6: Circle CenterX=189.124 CenterY=5.37834 CenterZ=0 NormalX=0 NormalY=0 NormalZ=1 AngleXU=0 Radius=1
    g7: Circle CenterX=185.124 CenterY=7.57463 CenterZ=0 NormalX=0 NormalY=0 NormalZ=1 AngleXU=0 Radius=1
    g8: Circle CenterX=185.124 CenterY=5.34704 CenterZ=0 NormalX=0 NormalY=0 NormalZ=1 AngleXU=0 Radius=1
    g9: BSplineCurve PolesCount=3 KnotsCount=2 Degree=2 IsPeriodic=0
    g10: GeomPoint X=189.124 Y=5.37834 Z=0
    g11: GeomPoint X=185.124 Y=5.34704 Z=0
    g12: Circle CenterX=224.513 CenterY=-14.0532 CenterZ=0 NormalX=0 NormalY=0 NormalZ=1 AngleXU=0 Radius=1
    g13: Circle CenterX=236.584 CenterY=-24.2775 CenterZ=0 NormalX=0 NormalY=0 NormalZ=1 AngleXU=0 Radius=1
    g14: BSplineCurve PolesCount=3 KnotsCount=2 Degree=2 IsPeriodic=0
    g15: GeomPoint X=236.584 Y=-24.2775 Z=0
    g16: Circle CenterX=125.607 CenterY=-21.7539 CenterZ=0 NormalX=0 NormalY=0 NormalZ=1 AngleXU=0 Radius=1
    g17: Circle CenterX=139.632 CenterY=-14.0532 CenterZ=0 NormalX=0 NormalY=0 NormalZ=1 AngleXU=0 Radius=1
    g18: Circle CenterX=127.325 CenterY=-24.2775 CenterZ=0 NormalX=0 NormalY=0 NormalZ=1 AngleXU=0 Radius=1
    g19: BSplineCurve PolesCount=3 KnotsCount=2 Degree=2 IsPeriodic=0
    g20: GeomPoint X=125.607 Y=-21.7539 Z=0
    g21: GeomPoint X=127.325 Y=-24.2775 Z=0
    g22: Circle CenterX=179.022 CenterY=-85.8163 CenterZ=0 NormalX=0 NormalY=0 NormalZ=1 AngleXU=0 Radius=1
    g23: Circle CenterX=179.022 CenterY=-91.7794 CenterZ=0 NormalX=0 NormalY=0 NormalZ=1 AngleXU=0 Radius=1
    g24: Circle CenterX=171.895 CenterY=-91.8014 CenterZ=0 NormalX=0 NormalY=0 NormalZ=1 AngleXU=0 Radius=1
    g25: BSplineCurve PolesCount=3 KnotsCount=2 Degree=2 IsPeriodic=0
    g26: GeomPoint X=179.022 Y=-85.8163 Z=0
    g27: GeomPoint X=171.895 Y=-91.8014 Z=0
    g28: Circle CenterX=185.124 CenterY=-86.2028 CenterZ=0 NormalX=0 NormalY=0 NormalZ=1 AngleXU=0 Radius=1
    g29: Circle CenterX=185.124 CenterY=-91.7794 CenterZ=0 NormalX=0 NormalY=0 NormalZ=1 AngleXU=0 Radius=1
    g30: Circle CenterX=191.747 CenterY=-91.7794 CenterZ=0 NormalX=0 NormalY=0 NormalZ=1 AngleXU=0 Radius=1
    g31: BSplineCurve PolesCount=3 KnotsCount=2 Degree=2 IsPeriodic=0
    g32: GeomPoint X=185.124 Y=-86.2028 Z=0
    g33: GeomPoint X=191.747 Y=-91.7794 Z=0
    g34: BSplineCurve PolesCount=5 KnotsCount=3 Degree=3 IsPeriodic=0
    g35: LineSegment StartX=132.072 StartY=-100.779 StartZ=0 EndX=132.072 EndY=-103.779 EndZ=0
    g36: GeomPoint X=232.072 Y=-94.7794 Z=0
    g37: GeomPoint X=223.072 Y=-97.7794 Z=0
    g38: Circle CenterX=232.072 CenterY=-94.7794 CenterZ=0 NormalX=0 NormalY=0 NormalZ=1 AngleXU=0 Radius=1
    g39: Circle CenterX=232.072 CenterY=-100.779 CenterZ=0 NormalX=0 NormalY=0 NormalZ=1 AngleXU=0 Radius=1
    g40: BSplineCurve PolesCount=5 KnotsCount=3 Degree=3 IsPeriodic=0
    g41: GeomPoint X=232.072 Y=-100.779 Z=0
    g42: LineSegment StartX=123.656 StartY=-37.1092 StartZ=0 EndX=122.136 EndY=-35.2714 EndZ=0
    g43: LineSegment StartX=117.05 StartY=-39.4781 StartZ=0 EndX=115.291 EndY=-37.3514 EndZ=0
    g44: LineSegment StartX=120.377 StartY=-33.1447 StartZ=0 EndX=118.86 EndY=-31.3104 EndZ=0
    g45: ArcOfCircle CenterX=116.562 CenterY=-19.6236 CenterZ=0 NormalX=0 NormalY=0 NormalZ=1 AngleXU=0 Radius=4.24264 StartAngle=1.28753 EndAngle=5.99992
    g46: LineSegment StartX=240.266 StartY=-37.1092 StartZ=0 EndX=189.124 EndY=5.37834 EndZ=0
    g47: LineSegment StartX=191.747 StartY=-91.7794 StartZ=0 EndX=232.072 EndY=-91.7794 EndZ=0
    g48: LineSegment StartX=232.072 StartY=-91.7794 StartZ=0 EndX=232.072 EndY=-94.7794 EndZ=0
    g49: LineSegment StartX=232.072 StartY=-100.779 StartZ=0 EndX=232.072 EndY=-103.779 EndZ=0
    g50: LineSegment StartX=132.072 StartY=-103.779 StartZ=0 EndX=232.072 EndY=-103.779 EndZ=0
    g51: LineSegment StartX=132.072 StartY=-91.8014 StartZ=0 EndX=132.072 EndY=-94.7791 EndZ=0
    g52: LineSegment StartX=132.072 StartY=-91.8014 StartZ=0 EndX=171.895 EndY=-91.8014 EndZ=0
    g53: LineSegment StartX=179.022 StartY=-85.8163 StartZ=0 EndX=179.022 EndY=5.34704 EndZ=0
    g54: LineSegment StartX=175.022 StartY=5.37834 StartZ=0 EndX=123.656 EndY=-37.1092 EndZ=0
    g55: LineSegment StartX=185.124 StartY=5.34704 StartZ=0 EndX=185.124 EndY=-86.2028 EndZ=0
    g56: LineSegment StartX=122.136 StartY=-35.2714 StartZ=0 EndX=117.05 EndY=-39.4781 EndZ=0
    g57: LineSegment StartX=115.291 StartY=-37.3514 StartZ=0 EndX=120.377 EndY=-33.1447 EndZ=0
    g58: LineSegment StartX=118.86 StartY=-31.3104 StartZ=0 EndX=127.325 EndY=-24.2775 EndZ=0
    g59: LineSegment StartX=125.607 StartY=-21.7539 StartZ=0 EndX=124.815 EndY=-22.1887 EndZ=0
    g60: LineSegment StartX=123.265 StartY=-19.3655 StartZ=0 EndX=124.815 EndY=-22.1887 EndZ=0
    g61: LineSegment StartX=120.636 StartY=-20.8094 StartZ=0 EndX=123.265 EndY=-19.3655 EndZ=0
    g62: LineSegment StartX=117.748 StartY=-15.55 StartZ=0 EndX=120.377 EndY=-14.1062 EndZ=0
    g63: LineSegment StartX=120.377 StartY=-14.1062 StartZ=0 EndX=118.934 EndY=-11.4765 EndZ=0
    g64: LineSegment StartX=236.584 StartY=-24.2775 StartZ=0 EndX=245.072 EndY=-31.3037 EndZ=0
    g65: LineSegment StartX=245.072 StartY=-31.3037 StartZ=0 EndX=243.535 EndY=-33.1602 EndZ=0
    g66: LineSegment StartX=243.535 StartY=-33.1602 StartZ=0 EndX=248.619 EndY=-37.3688 EndZ=0
    g67: LineSegment StartX=248.619 StartY=-37.3688 StartZ=0 EndX=246.855 EndY=-39.5064 EndZ=0
    g68: LineSegment StartX=246.855 StartY=-39.5064 StartZ=0 EndX=241.778 EndY=-35.2889 EndZ=0
    g69: LineSegment StartX=241.778 StartY=-35.2889 StartZ=0 EndX=240.266 EndY=-37.1092 EndZ=0
    g70: LineSegment StartX=243.628 StartY=-14.0323 StartZ=0 EndX=246.258 EndY=-15.476 EndZ=0
    g71: LineSegment StartX=240.741 StartY=-19.2917 StartZ=0 EndX=243.37 EndY=-20.7355 EndZ=0
    g72: ArcOfCircle CenterX=247.444 CenterY=-19.5496 CenterZ=0 NormalX=0 NormalY=0 NormalZ=1 AngleXU=0 Radius=4.24264 StartAngle=3.4249 EndAngle=8.13729
    g73: LineSegment StartX=240.741 StartY=-19.2917 StartZ=0 EndX=239.201 EndY=-22.0968 EndZ=0
    g74: LineSegment StartX=238.538 StartY=-21.7516 StartZ=0 EndX=239.201 EndY=-22.0968 EndZ=0
    g75: LineSegment StartX=245.072 StartY=-11.4025 StartZ=0 EndX=243.628 EndY=-14.0323 EndZ=0
    g76-g91: Circle x16 (B-spline internal-alignment scaffolding for g92; pole/knot coordinates omitted)
    g92: BSplineCurve PolesCount=16 KnotsCount=14 Degree=3 IsPeriodic=0
    g93-g106: GeomPoint x14 (B-spline internal-alignment scaffolding for g92; pole/knot coordinates omitted)
    g107: LineSegment StartX=165.871 StartY=14.2956 StartZ=0 EndX=118.934 EndY=-11.4765 EndZ=0
    g108: LineSegment StartX=198.264 StartY=14.2963 StartZ=0 EndX=245.072 EndY=-11.4025 EndZ=0
  constraints (146):
    c: Weight(g0) = 1
    c: Equal(g0,g1)
    c: Equal(g0,g2)
    c: InternalAlignment(g0,g3)
    c: InternalAlignment(g1,g3)
    c: InternalAlignment(g2,g3)
    c: InternalAlignment(g4,g3)
    c: InternalAlignment(g5,g3)
    c: Weight(g6) = 1
    c: Equal(g6,g7)
    c: Equal(g6,g8)
    c: InternalAlignment(g6,g9)
    c: InternalAlignment(g7,g9)
    c: InternalAlignment(g8,g9)
    c: InternalAlignment(g10,g9)
    c: InternalAlignment(g11,g9)
    c: Block(g9)
    c: Block(g3)
    c: InternalAlignment(g12,g14)
    c: InternalAlignment(g13,g14)
    c: InternalAlignment(g15,g14)
    c: Block(g14)
    c: Weight(g16) = 1
    c: Equal(g16,g17)
    c: Equal(g16,g18)
    c: InternalAlignment(g16,g19)
    c: InternalAlignment(g17,g19)
    c: InternalAlignment(g18,g19)
    c: InternalAlignment(g20,g19)
    c: InternalAlignment(g21,g19)
    c: Block(g19)
    c: Weight(g22) = 1
    c: Equal(g22,g23)
    c: Equal(g22,g24)
    c: InternalAlignment(g22,g25)
    c: InternalAlignment(g23,g25)
    c: InternalAlignment(g24,g25)
    c: InternalAlignment(g26,g25)
    c: InternalAlignment(g27,g25)
    c: Weight(g28) = 1
    c: Equal(g28,g29)
    c: Equal(g28,g30)
    c: InternalAlignment(g28,g31)
    c: InternalAlignment(g29,g31)
    c: InternalAlignment(g30,g31)
    c: InternalAlignment(g32,g31)
    c: InternalAlignment(g33,g31)
    c: Block(g31)
    c: Block(g25)
    c: Block(g34)
    c: Coincident(g35,g34)
    c: Vertical(g35)
    c: Block(g35)
    c: Equal(g38,g39)
    c: InternalAlignment(g38,g40)
    c: InternalAlignment(g39,g40)
    c: InternalAlignment(g36,g40)
    c: InternalAlignment(g37,g40)
    c: InternalAlignment(g41,g40)
    c: Block(g40)
    c: Distance(g42) = 2.385
    c: Distance(g43) = 2.76
    c: Parallel(g42,g44)
    c: Block(g45)
    c: Coincident(g46,g9)
    c: Coincident(g47,g31)
    c: Horizontal(g47)
    c: Block(g47)
    c: Coincident(g48,g47)
    c: Coincident(g48,g40)
    c: Vertical(g48)
    c: Block(g48)
    c: Coincident(g49,g40)
    c: Vertical(g49)
    c: Block(g49)
    c: Coincident(g50,g35)
    c: Coincident(g50,g49)
    c: Horizontal(g50)
    c: Block(g50)
    c: Coincident(g51,g34)
    c: Vertical(g51)
    c: Coincident(g52,g51)
    c: Coincident(g52,g25)
    c: Horizontal(g52)
    c: Coincident(g53,g25)
    c: Coincident(g53,g3)
    c: Vertical(g53)
    c: Coincident(g54,g3)
    c: Coincident(g54,g42)
    c: Coincident(g55,g9)
    c: Coincident(g55,g31)
    c: Vertical(g55)
    c: Block(g42)
    c: Coincident(g56,g42)
    c: Coincident(g56,g43)
    c: Coincident(g57,g43)
    c: Coincident(g57,g44)
    c: Block(g57)
    c: Block(g56)
    c: Coincident(g58,g44)
    c: Coincident(g58,g19)
    c: Block(g58)
    c: Coincident(g59,g19)
    c: Block(g59)
    c: Coincident(g60,g59)
    c: Block(g60)
    c: Coincident(g61,g45)
    c: Coincident(g61,g60)
    c: Coincident(g62,g45)
    c: Coincident(g63,g62)
    c: Block(g63)
    c: Coincident(g64,g14)
    c: Block(g64)
    c: Coincident(g65,g64)
    c: Coincident(g66,g65)
    c: Coincident(g67,g66)
    c: Coincident(g68,g67)
    c: Coincident(g69,g68)
    c: Coincident(g69,g46)
    c: Block(g46)
    c: Block(g68)
    c: Block(g66)
    c: Distance(g70) = 3
    c: Distance(g71) = 3
    c: Coincident(g72,g70)
    c: Coincident(g72,g71)
    c: Block(g72)
    c: Coincident(g73,g71)
    c: Distance(g73) = 3.2
    c: Coincident(g74,g14)
    c: Coincident(g74,g73)
    c: Coincident(g75,g70)
    c: Block(g75)
    c: Block(g73)
    c: Distance(g63) = 3
    c: Distance(g60) = 3.22077
    c: Weight(g76) = 1
    c: Equal(g76, g77-g91) x15
    c: InternalAlignment(g76-g91 -> g92) x16
    c: InternalAlignment(g93-g106 -> g92) x14
    c: Coincident(g107,g92)
    c: Coincident(g107,g63)
    c: Block(g107)
    c: Block(g92)
    c: Coincident(g108,g92)
    c: Coincident(g108,g75)
FEATURE [Sketcher::SketchObject] Sketch010  label="legBottomBack"
  FullyConstrained = true
  MapMode = 4
  Placement = pos=(0,0,0) rot=(0.57735,0.57735,0.57735;2.0944rad)
  sketch-geometry (76):
    g0: Circle CenterX=-17.0256 CenterY=-190.268 CenterZ=0 NormalX=0 NormalY=0 NormalZ=1 AngleXU=0 Radius=10.5072
    g1: Circle CenterX=-37.7758 CenterY=-187.672 CenterZ=0 NormalX=0 NormalY=0 NormalZ=1 AngleXU=0 Radius=5.64388
    g2: Circle CenterX=-51.4606 CenterY=-185.091 CenterZ=0 NormalX=0 NormalY=0 NormalZ=1 AngleXU=0 Radius=3.01653
    g3: Circle CenterX=-60.4835 CenterY=-182.688 CenterZ=0 NormalX=0 NormalY=0 NormalZ=1 AngleXU=0 Radius=2.12826
    g4: Circle CenterX=-3.29005 CenterY=-177.662 CenterZ=0 NormalX=0 NormalY=0 NormalZ=1 AngleXU=0 Radius=3.26661
    g5: ArcOfCircle CenterX=11.0205 CenterY=-198.019 CenterZ=0 NormalX=0 NormalY=0 NormalZ=1 AngleXU=0 Radius=13 StartAngle=2.78068 EndAngle=5.92131
    g6: LineSegment StartX=5.08312 StartY=-176.581 StartZ=0 EndX=-1.14188 EndY=-193.429 EndZ=0
    g7: ArcOfCircle CenterX=17.2475 CenterY=-181.166 CenterZ=0 NormalX=0 NormalY=0 NormalZ=1 AngleXU=0 Radius=13 StartAngle=1.21042 EndAngle=2.78109
    g8: LineSegment StartX=38.8952 StartY=-231.233 StartZ=0 EndX=39.9512 EndY=-228.425 EndZ=0
    g9: ArcOfCircle CenterX=46.9911 CenterY=-209.705 CenterZ=0 NormalX=0 NormalY=0 NormalZ=1 AngleXU=0 Radius=20 StartAngle=2.78766 EndAngle=4.35269
    g10: LineSegment StartX=23.7323 StartY=-126.969 StartZ=0 EndX=17.4091 EndY=-143.817 EndZ=0
    g11: ArcOfCircle CenterX=29.5716 CenterY=-148.408 CenterZ=0 NormalX=0 NormalY=0 NormalZ=1 AngleXU=0 Radius=13 StartAngle=2.78068 EndAngle=4.35262
    g12: ArcOfCircle CenterX=35.8967 CenterY=-131.555 CenterZ=0 NormalX=0 NormalY=0 NormalZ=1 AngleXU=0 Radius=13 StartAngle=1.21584 EndAngle=2.78109
    g13: ArcOfCircle CenterX=48.1805 CenterY=-98.7782 CenterZ=0 NormalX=0 NormalY=0 NormalZ=1 AngleXU=0 Radius=13 StartAngle=2.78068 EndAngle=4.35005
    g14: LineSegment StartX=42.354 StartY=-77.3391 StartZ=0 EndX=36.018 EndY=-94.1875 EndZ=0
    g15: ArcOfCircle CenterX=54.5183 CenterY=-81.9247 CenterZ=0 NormalX=0 NormalY=0 NormalZ=1 AngleXU=0 Radius=13 StartAngle=2.42113 EndAngle=2.78109
    g16: ArcOfCircle CenterX=20.184 CenterY=-217.506 CenterZ=0 NormalX=0 NormalY=0 NormalZ=1 AngleXU=0 Radius=3.81084 StartAngle=1.88136 EndAngle=6.80465
    g17: LineSegment StartX=38.4753 StartY=-115.966 StartZ=0 EndX=41.2852 EndY=-117.017 EndZ=0
    g18: ArcOfCircle CenterX=36.3663 CenterY=-113.042 CenterZ=0 NormalX=0 NormalY=0 NormalZ=1 AngleXU=0 Radius=3.60555 StartAngle=0.230024 EndAngle=5.3372
    g19: LineSegment StartX=39.8769 StartY=-112.22 StartZ=0 EndX=42.6867 EndY=-113.271 EndZ=0
    g20: LineSegment StartX=19.9036 StartY=-165.61 StartZ=0 EndX=22.7134 EndY=-166.661 EndZ=0
    g21: ArcOfCircle CenterX=17.7945 CenterY=-162.686 CenterZ=0 NormalX=0 NormalY=0 NormalZ=1 AngleXU=0 Radius=3.60555 StartAngle=0.230024 EndAngle=5.3372
    g22: LineSegment StartX=21.3051 StartY=-161.864 StartZ=0 EndX=24.1149 EndY=-162.915 EndZ=0
    g23: LineSegment StartX=41.085 StartY=-66.3176 StartZ=0 EndX=46.0385 EndY=-62.5254 EndZ=0
    g24: LineSegment StartX=48.9563 StartY=-66.3367 StartZ=0 EndX=44.7488 EndY=-73.3482 EndZ=0
    g25: ArcOfCircle CenterX=49.8795 CenterY=-62.6074 CenterZ=0 NormalX=0 NormalY=0 NormalZ=1 AngleXU=0 Radius=3.84187 StartAngle=4.46973 EndAngle=9.40343
    g26: LineSegment StartX=43.5724 StartY=-110.934 StartZ=0 EndX=42.6867 EndY=-113.271 EndZ=0
    g27: LineSegment StartX=40.4148 StartY=-119.365 StartZ=0 EndX=41.2852 EndY=-117.017 EndZ=0
    g28: LineSegment StartX=21.8316 StartY=-169.001 StartZ=0 EndX=22.7134 EndY=-166.661 EndZ=0
    g29: LineSegment StartX=24.9948 StartY=-160.575 StartZ=0 EndX=24.1149 EndY=-162.915 EndZ=0
    g30: LineSegment StartX=23.1786 StartY=-202.622 StartZ=0 EndX=19.0195 EndY=-213.878 EndZ=0
    g31: LineSegment StartX=28.2308 StartY=-202.773 StartZ=0 EndX=23.4884 EndY=-215.608 EndZ=0
    g32: LineSegment StartX=-76.2249 StartY=-179.393 StartZ=0 EndX=-72.8553 EndY=-180.66 EndZ=0
    g33: ArcOfCircle CenterX=-71.1257 CenterY=-183.448 CenterZ=0 NormalX=0 NormalY=0 NormalZ=1 AngleXU=0 Radius=3.28025 StartAngle=3.43759 EndAngle=8.40938
    g34: LineSegment StartX=-79.0409 StartY=-186.881 StartZ=0 EndX=38.8952 EndY=-231.233 EndZ=0
    g35-g53: Circle x19 (B-spline internal-alignment scaffolding for g54; pole/knot coordinates omitted)
    g54: BSplineCurve PolesCount=19 KnotsCount=17 Degree=3 IsPeriodic=0
    g55-g71: GeomPoint x17 (B-spline internal-alignment scaffolding for g54; pole/knot coordinates omitted)
    g72: LineSegment StartX=-74.2633 StartY=-184.404 StartZ=0 EndX=-77.6329 EndY=-183.137 EndZ=0
    g73: LineSegment StartX=-79.0409 StartY=-186.881 StartZ=0 EndX=-77.6329 EndY=-183.137 EndZ=0
    g74: LineSegment StartX=8.65492 StartY=-152.553 StartZ=0 EndX=41.085 EndY=-66.3176 EndZ=0
    g75: LineSegment StartX=-74.4658 StartY=-174.715 StartZ=0 EndX=-76.2249 EndY=-179.393 EndZ=0
  constraints (76):
    c: Block(g5)
    c: Block(g7)
    c: Block(g0)
    c: Block(g4)
    c: Block(g1)
    c: Block(g2)
    c: Block(g3)
    c: Block(g9)
    c: Coincident(g8,g9)
    c: Block(g8)
    c: Coincident(g6,g7)
    c: Coincident(g6,g5)
    c: Block(g11)
    c: Block(g12)
    c: Coincident(g10,g12)
    c: Coincident(g10,g11)
    c: Block(g13)
    c: Block(g15)
    c: Coincident(g14,g15)
    c: Coincident(g14,g13)
    c: Block(g16)
    c: Block(g18)
    c: Coincident(g19,g18)
    c: Coincident(g17,g18)
    c: Parallel(g19,g17)
    c: Block(g17)
    c: Block(g19)
    c: Block(g21)
    c: Coincident(g22,g21)
    c: Coincident(g20,g21)
    c: Parallel(g22,g20)
    c: Block(g20)
    c: Block(g22)
    c: Block(g23)
    c: Coincident(g25,g23)
    c: Coincident(g25,g24)
    c: Block(g25)
    c: Block(g24)
    c: Coincident(g26,g19)
    c: Block(g26)
    c: Coincident(g27,g17)
    c: Block(g27)
    c: Coincident(g28,g20)
    c: Coincident(g29,g22)
    c: Block(g29)
    c: Block(g28)
    c: Coincident(g30,g5)
    c: Coincident(g30,g16)
    c: Block(g30)
    c: Coincident(g7,g28)
    c: Coincident(g11,g29)
    c: Coincident(g12,g27)
    c: Coincident(g13,g26)
    c: Coincident(g15,g24)
    c: Coincident(g31,g9)
    c: Coincident(g31,g16)
    c: Distance(g32) = 3.6
    c: Block(g32)
    c: Coincident(g33,g32)
    c: Coincident(g34,g8)
    c: Weight(g35) = 1
    c: Equal(g35, g36-g53) x18
    c: InternalAlignment(g35-g53 -> g54) x19
    c: InternalAlignment(g55-g71 -> g54) x17
    c: Block(g33)
    c: Block(g54)
    c: Coincident(g72,g33)
    c: Coincident(g73,g34)
    c: Block(g34)
    c: Parallel(g72,g34)
    c: Perpendicular(g73,g34)
    c: Coincident(g72,g73)
    c: Coincident(g74,g54)
    c: Coincident(g74,g23)
    c: Coincident(g75,g54)
    c: Coincident(g75,g32)
FEATURE [Sketcher::SketchObject] Sketch011  label="legBottomFront"
  FullyConstrained = true
  MapMode = 4
  Placement = pos=(0,0,0) rot=(0.57735,0.57735,0.57735;2.0944rad)
  sketch-geometry (13):
    g0: LineSegment StartX=-199.665 StartY=-138.314 StartZ=0 EndX=-200.721 EndY=-141.122 EndZ=0
    g1: LineSegment StartX=-200.721 StartY=-141.122 StartZ=0 EndX=-79.0409 EndY=-186.881 EndZ=0
    g2: ArcOfCircle CenterX=-71.1257 CenterY=-183.448 CenterZ=0 NormalX=0 NormalY=0 NormalZ=1 AngleXU=0 Radius=3.28025 StartAngle=3.43759 EndAngle=8.40938
    g3: LineSegment StartX=-74.4626 StartY=-174.707 StartZ=0 EndX=-76.2249 EndY=-179.393 EndZ=0
    g4: LineSegment StartX=-76.2249 StartY=-179.393 StartZ=0 EndX=-72.8553 EndY=-180.66 EndZ=0
    g5: Circle CenterX=-74.4626 CenterY=-174.707 CenterZ=0 NormalX=0 NormalY=0 NormalZ=1 AngleXU=0 Radius=1
    g6: Circle CenterX=-130.185 CenterY=-164.454 CenterZ=0 NormalX=0 NormalY=0 NormalZ=1 AngleXU=0 Radius=1
    g7: Circle CenterX=-199.665 CenterY=-138.314 CenterZ=0 NormalX=0 NormalY=0 NormalZ=1 AngleXU=0 Radius=1
    g8: BSplineCurve PolesCount=3 KnotsCount=2 Degree=2 IsPeriodic=0
    g9: GeomPoint X=-74.4626 Y=-174.707 Z=0
    g10: GeomPoint X=-199.665 Y=-138.314 Z=0
    g11: LineSegment StartX=-77.6329 StartY=-183.137 StartZ=0 EndX=-79.0409 EndY=-186.881 EndZ=0
    g12: LineSegment StartX=-77.6329 StartY=-183.137 StartZ=0 EndX=-74.2633 EndY=-184.404 EndZ=0
  constraints (24):
    c: Coincident(g1,g0)
    c: Block(g0)
    c: Perpendicular(g1,g0)
    c: Distance(g1) = 130
    c: Coincident(g4,g3)
    c: Coincident(g4,g2)
    c: Block(g2)
    c: Block(g4)
    c: Coincident(g8,g3)
    c: Weight(g5) = 1
    c: Equal(g5,g6)
    c: Equal(g5,g7)
    c: Coincident(g8,g0)
    c: InternalAlignment(g5,g8)
    c: InternalAlignment(g6,g8)
    c: InternalAlignment(g7,g8)
    c: InternalAlignment(g9,g8)
    c: InternalAlignment(g10,g8)
    c: Block(g8)
    c: Block(g3)
    c: Coincident(g11,g1)
    c: Coincident(g12,g11)
    c: Coincident(g12,g2)
    c: Block(g12)
FEATURE [Sketcher::SketchObject] Sketch
  FullyConstrained = false
  Placement = pos=(0,0,0) rot=(-1,0,0;4.71239rad)
  sketch-geometry (1):
    g0: LineSegment StartX=22.0563 StartY=-2.3728 StartZ=0 EndX=22.0563 EndY=-112.373 EndZ=0
  constraints (2):
    c: Vertical(g0)
    c: Distance(g0) = 110
